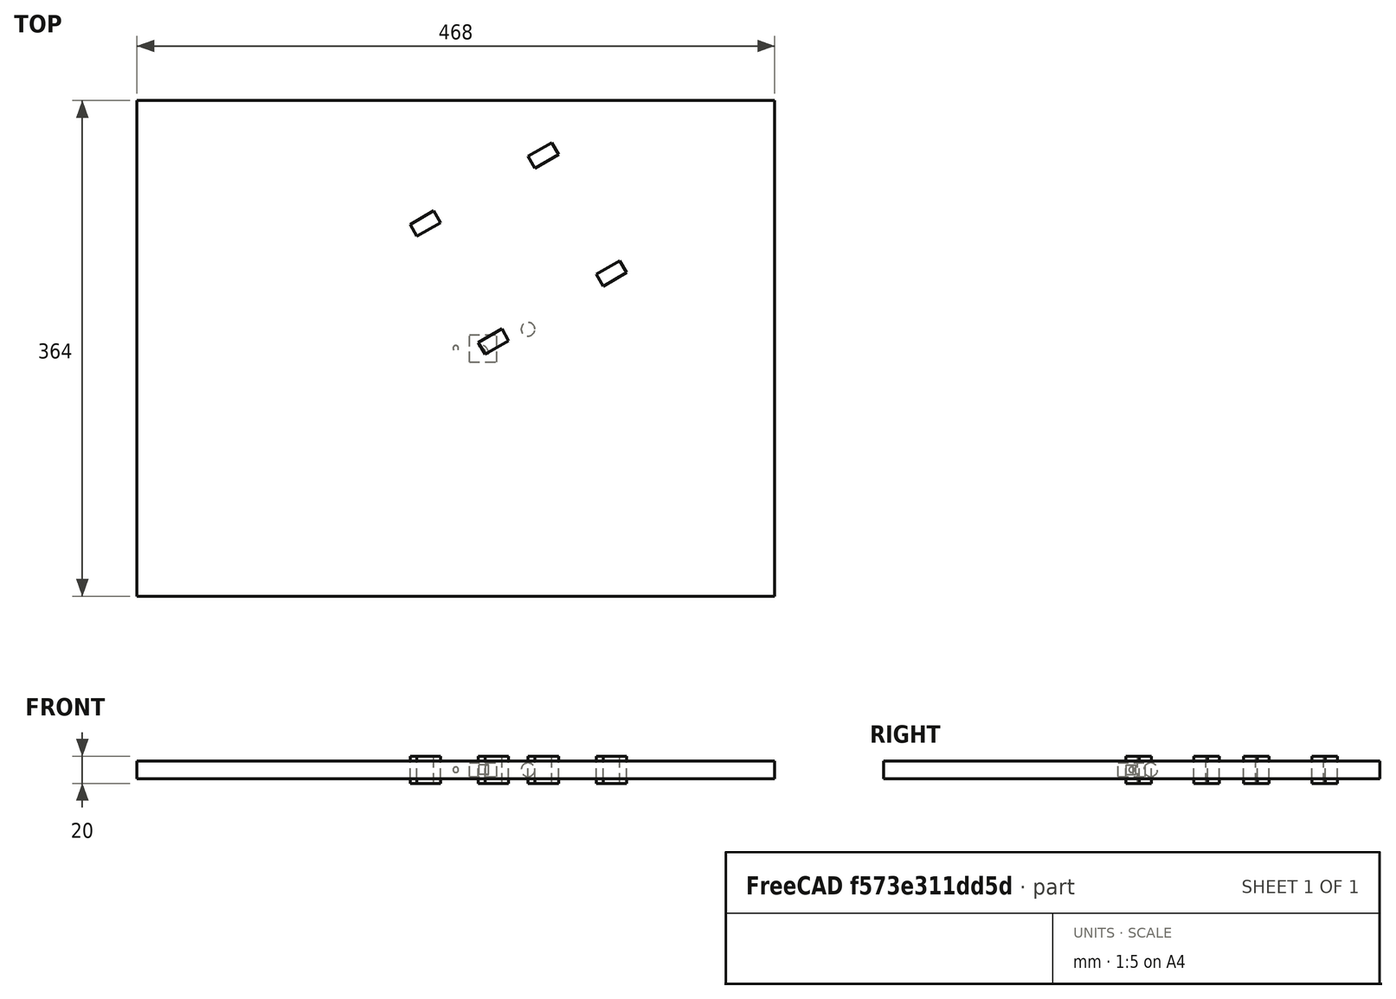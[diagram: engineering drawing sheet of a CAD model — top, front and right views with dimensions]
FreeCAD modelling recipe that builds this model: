
FCSTD DOCUMENT  (FreeCAD 0.21R33694 (Git))
Label: orthoArray-of-Container
License: All rights reserved
LicenseURL: http://en.wikipedia.org/wiki/All_rights_reserved
objects: App::DocumentObjectGroupPython×1251, App::Part×6, Part::FeaturePython×5, Part::Sphere×1
note: 6 computed .brp shape members not serialized (recipe doc carries the construction recipe); baked Part::Feature solids carry a one-line shape summary decoded from their .brp

FEATURE [App::DocumentObjectGroupPython] HALFPI  # scripted group (container) (typed FeaturePython)
  name = HALFPI
  value = pi/2.
FEATURE [App::DocumentObjectGroupPython] PI  # scripted group (container) (typed FeaturePython)
  name = PI
  value = 1.*pi
FEATURE [App::DocumentObjectGroupPython] TWOPI  # scripted group (container) (typed FeaturePython)
  name = TWOPI
  value = 2.*pi
FEATURE [App::DocumentObjectGroupPython] Constants  # scripted group (container) (typed FeaturePython)
  Group = -> [HALFPI,PI,TWOPI]
FEATURE [App::DocumentObjectGroupPython] Variables  # scripted group (container) (typed FeaturePython)
FEATURE [App::DocumentObjectGroupPython] Quantities  # scripted group (container) (typed FeaturePython)
FEATURE [App::DocumentObjectGroupPython] Isotopes  # scripted group (container) (typed FeaturePython)
FEATURE [App::DocumentObjectGroupPython] Elements  # scripted group (container) (typed FeaturePython)
FEATURE [App::DocumentObjectGroupPython] Matrix  # scripted group (container) (typed FeaturePython)
FEATURE [App::DocumentObjectGroupPython] Surfaces  # scripted group (container) (typed FeaturePython)
FEATURE [App::DocumentObjectGroupPython] Opticals  # scripted group (container) (typed FeaturePython)
  Group = -> [Matrix,Surfaces]
FEATURE [App::DocumentObjectGroupPython] G4Isotopes  # scripted group (container) (typed FeaturePython)
FEATURE [App::DocumentObjectGroupPython] H_element  # scripted group (container) (typed FeaturePython)
  Z = 1
  atom_value = 1.008
  formula = H
  name = H_element
FEATURE [App::DocumentObjectGroupPython] He_element  # scripted group (container) (typed FeaturePython)
  Z = 2
  atom_value = 4.0026
  formula = He
  name = He_element
FEATURE [App::DocumentObjectGroupPython] Li_element  # scripted group (container) (typed FeaturePython)
  Z = 3
  atom_value = 6.94
  formula = Li
  name = Li_element
FEATURE [App::DocumentObjectGroupPython] Be_element  # scripted group (container) (typed FeaturePython)
  Z = 4
  atom_value = 9.01218
  formula = Be
  name = Be_element
FEATURE [App::DocumentObjectGroupPython] B_element  # scripted group (container) (typed FeaturePython)
  Z = 5
  atom_value = 10.81
  formula = B
  name = B_element
FEATURE [App::DocumentObjectGroupPython] C_element  # scripted group (container) (typed FeaturePython)
  Z = 6
  atom_value = 12.011
  formula = C
  name = C_element
FEATURE [App::DocumentObjectGroupPython] N_element  # scripted group (container) (typed FeaturePython)
  Z = 7
  atom_value = 14.007
  formula = N
  name = N_element
FEATURE [App::DocumentObjectGroupPython] O_element  # scripted group (container) (typed FeaturePython)
  Z = 8
  atom_value = 15.999
  formula = O
  name = O_element
FEATURE [App::DocumentObjectGroupPython] F_element  # scripted group (container) (typed FeaturePython)
  Z = 9
  atom_value = 18.9984
  formula = F
  name = F_element
FEATURE [App::DocumentObjectGroupPython] Ne_element  # scripted group (container) (typed FeaturePython)
  Z = 10
  atom_value = 20.1797
  formula = Ne
  name = Ne_element
FEATURE [App::DocumentObjectGroupPython] Na_element  # scripted group (container) (typed FeaturePython)
  Z = 11
  atom_value = 22.9898
  formula = Na
  name = Na_element
FEATURE [App::DocumentObjectGroupPython] Mg_element  # scripted group (container) (typed FeaturePython)
  Z = 12
  atom_value = 24.305
  formula = Mg
  name = Mg_element
FEATURE [App::DocumentObjectGroupPython] Al_element  # scripted group (container) (typed FeaturePython)
  Z = 13
  atom_value = 26.9815
  formula = Al
  name = Al_element
FEATURE [App::DocumentObjectGroupPython] Si_element  # scripted group (container) (typed FeaturePython)
  Z = 14
  atom_value = 28.085
  formula = Si
  name = Si_element
FEATURE [App::DocumentObjectGroupPython] P_element  # scripted group (container) (typed FeaturePython)
  Z = 15
  atom_value = 30.9738
  formula = P
  name = P_element
FEATURE [App::DocumentObjectGroupPython] S_element  # scripted group (container) (typed FeaturePython)
  Z = 16
  atom_value = 32.06
  formula = S
  name = S_element
FEATURE [App::DocumentObjectGroupPython] Cl_element  # scripted group (container) (typed FeaturePython)
  Z = 17
  atom_value = 35.45
  formula = Cl
  name = Cl_element
FEATURE [App::DocumentObjectGroupPython] Ar_element  # scripted group (container) (typed FeaturePython)
  Z = 18
  atom_value = 39.95
  formula = Ar
  name = Ar_element
FEATURE [App::DocumentObjectGroupPython] K_element  # scripted group (container) (typed FeaturePython)
  Z = 19
  atom_value = 39.0983
  formula = K
  name = K_element
FEATURE [App::DocumentObjectGroupPython] Ca_element  # scripted group (container) (typed FeaturePython)
  Z = 20
  atom_value = 40.078
  formula = Ca
  name = Ca_element
FEATURE [App::DocumentObjectGroupPython] Sc_element  # scripted group (container) (typed FeaturePython)
  Z = 21
  atom_value = 44.9559
  formula = Sc
  name = Sc_element
FEATURE [App::DocumentObjectGroupPython] Ti_element  # scripted group (container) (typed FeaturePython)
  Z = 22
  atom_value = 47.867
  formula = Ti
  name = Ti_element
FEATURE [App::DocumentObjectGroupPython] V_element  # scripted group (container) (typed FeaturePython)
  Z = 23
  atom_value = 50.9415
  formula = V
  name = V_element
FEATURE [App::DocumentObjectGroupPython] Cr_element  # scripted group (container) (typed FeaturePython)
  Z = 24
  atom_value = 51.9961
  formula = Cr
  name = Cr_element
FEATURE [App::DocumentObjectGroupPython] Mn_element  # scripted group (container) (typed FeaturePython)
  Z = 25
  atom_value = 54.938
  formula = Mn
  name = Mn_element
FEATURE [App::DocumentObjectGroupPython] Fe_element  # scripted group (container) (typed FeaturePython)
  Z = 26
  atom_value = 55.845
  formula = Fe
  name = Fe_element
FEATURE [App::DocumentObjectGroupPython] Co_element  # scripted group (container) (typed FeaturePython)
  Z = 27
  atom_value = 58.9332
  formula = Co
  name = Co_element
FEATURE [App::DocumentObjectGroupPython] Ni_element  # scripted group (container) (typed FeaturePython)
  Z = 28
  atom_value = 58.6934
  formula = Ni
  name = Ni_element
FEATURE [App::DocumentObjectGroupPython] Cu_element  # scripted group (container) (typed FeaturePython)
  Z = 29
  atom_value = 63.546
  formula = Cu
  name = Cu_element
FEATURE [App::DocumentObjectGroupPython] Zn_element  # scripted group (container) (typed FeaturePython)
  Z = 30
  atom_value = 65.38
  formula = Zn
  name = Zn_element
FEATURE [App::DocumentObjectGroupPython] Ga_element  # scripted group (container) (typed FeaturePython)
  Z = 31
  atom_value = 69.723
  formula = Ga
  name = Ga_element
FEATURE [App::DocumentObjectGroupPython] Ge_element  # scripted group (container) (typed FeaturePython)
  Z = 32
  atom_value = 72.63
  formula = Ge
  name = Ge_element
FEATURE [App::DocumentObjectGroupPython] As_element  # scripted group (container) (typed FeaturePython)
  Z = 33
  atom_value = 74.9216
  formula = As
  name = As_element
FEATURE [App::DocumentObjectGroupPython] Se_element  # scripted group (container) (typed FeaturePython)
  Z = 34
  atom_value = 78.971
  formula = Se
  name = Se_element
FEATURE [App::DocumentObjectGroupPython] Br_element  # scripted group (container) (typed FeaturePython)
  Z = 35
  atom_value = 79.904
  formula = Br
  name = Br_element
FEATURE [App::DocumentObjectGroupPython] Kr_element  # scripted group (container) (typed FeaturePython)
  Z = 36
  atom_value = 83.798
  formula = Kr
  name = Kr_element
FEATURE [App::DocumentObjectGroupPython] Rb_element  # scripted group (container) (typed FeaturePython)
  Z = 37
  atom_value = 85.4678
  formula = Rb
  name = Rb_element
FEATURE [App::DocumentObjectGroupPython] Sr_element  # scripted group (container) (typed FeaturePython)
  Z = 38
  atom_value = 87.62
  formula = Sr
  name = Sr_element
FEATURE [App::DocumentObjectGroupPython] Y_element  # scripted group (container) (typed FeaturePython)
  Z = 39
  atom_value = 88.9058
  formula = Y
  name = Y_element
FEATURE [App::DocumentObjectGroupPython] Zr_element  # scripted group (container) (typed FeaturePython)
  Z = 40
  atom_value = 91.224
  formula = Zr
  name = Zr_element
FEATURE [App::DocumentObjectGroupPython] Nb_element  # scripted group (container) (typed FeaturePython)
  Z = 41
  atom_value = 92.9064
  formula = Nb
  name = Nb_element
FEATURE [App::DocumentObjectGroupPython] Mo_element  # scripted group (container) (typed FeaturePython)
  Z = 42
  atom_value = 95.95
  formula = Mo
  name = Mo_element
FEATURE [App::DocumentObjectGroupPython] Tc_element  # scripted group (container) (typed FeaturePython)
  Z = 43
  atom_value = 97
  formula = Tc
  name = Tc_element
FEATURE [App::DocumentObjectGroupPython] Ru_element  # scripted group (container) (typed FeaturePython)
  Z = 44
  atom_value = 101.07
  formula = Ru
  name = Ru_element
FEATURE [App::DocumentObjectGroupPython] Rh_element  # scripted group (container) (typed FeaturePython)
  Z = 45
  atom_value = 102.905
  formula = Rh
  name = Rh_element
FEATURE [App::DocumentObjectGroupPython] Pd_element  # scripted group (container) (typed FeaturePython)
  Z = 46
  atom_value = 106.42
  formula = Pd
  name = Pd_element
FEATURE [App::DocumentObjectGroupPython] Ag_element  # scripted group (container) (typed FeaturePython)
  Z = 47
  atom_value = 107.868
  formula = Ag
  name = Ag_element
FEATURE [App::DocumentObjectGroupPython] Cd_element  # scripted group (container) (typed FeaturePython)
  Z = 48
  atom_value = 112.414
  formula = Cd
  name = Cd_element
FEATURE [App::DocumentObjectGroupPython] In_element  # scripted group (container) (typed FeaturePython)
  Z = 49
  atom_value = 114.818
  formula = In
  name = In_element
FEATURE [App::DocumentObjectGroupPython] Sn_element  # scripted group (container) (typed FeaturePython)
  Z = 50
  atom_value = 118.71
  formula = Sn
  name = Sn_element
FEATURE [App::DocumentObjectGroupPython] Sb_element  # scripted group (container) (typed FeaturePython)
  Z = 51
  atom_value = 121.76
  formula = Sb
  name = Sb_element
FEATURE [App::DocumentObjectGroupPython] Te_element  # scripted group (container) (typed FeaturePython)
  Z = 52
  atom_value = 127.6
  formula = Te
  name = Te_element
FEATURE [App::DocumentObjectGroupPython] I_element  # scripted group (container) (typed FeaturePython)
  Z = 53
  atom_value = 126.904
  formula = I
  name = I_element
FEATURE [App::DocumentObjectGroupPython] Xe_element  # scripted group (container) (typed FeaturePython)
  Z = 54
  atom_value = 131.293
  formula = Xe
  name = Xe_element
FEATURE [App::DocumentObjectGroupPython] Cs_element  # scripted group (container) (typed FeaturePython)
  Z = 55
  atom_value = 132.905
  formula = Cs
  name = Cs_element
FEATURE [App::DocumentObjectGroupPython] Ba_element  # scripted group (container) (typed FeaturePython)
  Z = 56
  atom_value = 137.327
  formula = Ba
  name = Ba_element
FEATURE [App::DocumentObjectGroupPython] La_element  # scripted group (container) (typed FeaturePython)
  Z = 57
  atom_value = 138.905
  formula = La
  name = La_element
FEATURE [App::DocumentObjectGroupPython] Ce_element  # scripted group (container) (typed FeaturePython)
  Z = 58
  atom_value = 140.116
  formula = Ce
  name = Ce_element
FEATURE [App::DocumentObjectGroupPython] Pr_element  # scripted group (container) (typed FeaturePython)
  Z = 59
  atom_value = 140.908
  formula = Pr
  name = Pr_element
FEATURE [App::DocumentObjectGroupPython] Nd_element  # scripted group (container) (typed FeaturePython)
  Z = 60
  atom_value = 144.242
  formula = Nd
  name = Nd_element
FEATURE [App::DocumentObjectGroupPython] Pm_element  # scripted group (container) (typed FeaturePython)
  Z = 61
  atom_value = 145
  formula = Pm
  name = Pm_element
FEATURE [App::DocumentObjectGroupPython] Sm_element  # scripted group (container) (typed FeaturePython)
  Z = 62
  atom_value = 150.36
  formula = Sm
  name = Sm_element
FEATURE [App::DocumentObjectGroupPython] Eu_element  # scripted group (container) (typed FeaturePython)
  Z = 63
  atom_value = 151.964
  formula = Eu
  name = Eu_element
FEATURE [App::DocumentObjectGroupPython] Gd_element  # scripted group (container) (typed FeaturePython)
  Z = 64
  atom_value = 157.25
  formula = Gd
  name = Gd_element
FEATURE [App::DocumentObjectGroupPython] Tb_element  # scripted group (container) (typed FeaturePython)
  Z = 65
  atom_value = 158.925
  formula = Tb
  name = Tb_element
FEATURE [App::DocumentObjectGroupPython] Dy_element  # scripted group (container) (typed FeaturePython)
  Z = 66
  atom_value = 162.5
  formula = Dy
  name = Dy_element
FEATURE [App::DocumentObjectGroupPython] Ho_element  # scripted group (container) (typed FeaturePython)
  Z = 67
  atom_value = 164.93
  formula = Ho
  name = Ho_element
FEATURE [App::DocumentObjectGroupPython] Er_element  # scripted group (container) (typed FeaturePython)
  Z = 68
  atom_value = 167.259
  formula = Er
  name = Er_element
FEATURE [App::DocumentObjectGroupPython] Tm_element  # scripted group (container) (typed FeaturePython)
  Z = 69
  atom_value = 168.934
  formula = Tm
  name = Tm_element
FEATURE [App::DocumentObjectGroupPython] Yb_element  # scripted group (container) (typed FeaturePython)
  Z = 70
  atom_value = 173.045
  formula = Yb
  name = Yb_element
FEATURE [App::DocumentObjectGroupPython] Lu_element  # scripted group (container) (typed FeaturePython)
  Z = 71
  atom_value = 174.967
  formula = Lu
  name = Lu_element
FEATURE [App::DocumentObjectGroupPython] Hf_element  # scripted group (container) (typed FeaturePython)
  Z = 72
  atom_value = 178.49
  formula = Hf
  name = Hf_element
FEATURE [App::DocumentObjectGroupPython] Ta_element  # scripted group (container) (typed FeaturePython)
  Z = 73
  atom_value = 180.948
  formula = Ta
  name = Ta_element
FEATURE [App::DocumentObjectGroupPython] W_element  # scripted group (container) (typed FeaturePython)
  Z = 74
  atom_value = 183.84
  formula = W
  name = W_element
FEATURE [App::DocumentObjectGroupPython] Re_element  # scripted group (container) (typed FeaturePython)
  Z = 75
  atom_value = 186.207
  formula = Re
  name = Re_element
FEATURE [App::DocumentObjectGroupPython] Os_element  # scripted group (container) (typed FeaturePython)
  Z = 76
  atom_value = 190.23
  formula = Os
  name = Os_element
FEATURE [App::DocumentObjectGroupPython] Ir_element  # scripted group (container) (typed FeaturePython)
  Z = 77
  atom_value = 192.217
  formula = Ir
  name = Ir_element
FEATURE [App::DocumentObjectGroupPython] Pt_element  # scripted group (container) (typed FeaturePython)
  Z = 78
  atom_value = 195.084
  formula = Pt
  name = Pt_element
FEATURE [App::DocumentObjectGroupPython] Au_element  # scripted group (container) (typed FeaturePython)
  Z = 79
  atom_value = 196.967
  formula = Au
  name = Au_element
FEATURE [App::DocumentObjectGroupPython] Hg_element  # scripted group (container) (typed FeaturePython)
  Z = 80
  atom_value = 200.592
  formula = Hg
  name = Hg_element
FEATURE [App::DocumentObjectGroupPython] Tl_element  # scripted group (container) (typed FeaturePython)
  Z = 81
  atom_value = 204.38
  formula = Tl
  name = Tl_element
FEATURE [App::DocumentObjectGroupPython] Pb_element  # scripted group (container) (typed FeaturePython)
  Z = 82
  atom_value = 207.2
  formula = Pb
  name = Pb_element
FEATURE [App::DocumentObjectGroupPython] Bi_element  # scripted group (container) (typed FeaturePython)
  Z = 83
  atom_value = 208.98
  formula = Bi
  name = Bi_element
FEATURE [App::DocumentObjectGroupPython] Po_element  # scripted group (container) (typed FeaturePython)
  Z = 84
  atom_value = 209
  formula = Po
  name = Po_element
FEATURE [App::DocumentObjectGroupPython] At_element  # scripted group (container) (typed FeaturePython)
  Z = 85
  atom_value = 210
  formula = At
  name = At_element
FEATURE [App::DocumentObjectGroupPython] Rn_element  # scripted group (container) (typed FeaturePython)
  Z = 86
  atom_value = 222
  formula = Rn
  name = Rn_element
FEATURE [App::DocumentObjectGroupPython] Fr_element  # scripted group (container) (typed FeaturePython)
  Z = 87
  atom_value = 223
  formula = Fr
  name = Fr_element
FEATURE [App::DocumentObjectGroupPython] Ra_element  # scripted group (container) (typed FeaturePython)
  Z = 88
  atom_value = 226
  formula = Ra
  name = Ra_element
FEATURE [App::DocumentObjectGroupPython] Ac_element  # scripted group (container) (typed FeaturePython)
  Z = 89
  atom_value = 227
  formula = Ac
  name = Ac_element
FEATURE [App::DocumentObjectGroupPython] Th_element  # scripted group (container) (typed FeaturePython)
  Z = 90
  atom_value = 232.038
  formula = Th
  name = Th_element
FEATURE [App::DocumentObjectGroupPython] Pa_element  # scripted group (container) (typed FeaturePython)
  Z = 91
  atom_value = 231.036
  formula = Pa
  name = Pa_element
FEATURE [App::DocumentObjectGroupPython] U_element  # scripted group (container) (typed FeaturePython)
  Z = 92
  atom_value = 238.029
  formula = U
  name = U_element
FEATURE [App::DocumentObjectGroupPython] Np_element  # scripted group (container) (typed FeaturePython)
  Z = 93
  atom_value = 237
  formula = Np
  name = Np_element
FEATURE [App::DocumentObjectGroupPython] Pu_element  # scripted group (container) (typed FeaturePython)
  Z = 94
  atom_value = 244
  formula = Pu
  name = Pu_element
FEATURE [App::DocumentObjectGroupPython] Am_element  # scripted group (container) (typed FeaturePython)
  Z = 95
  atom_value = 243
  formula = Am
  name = Am_element
FEATURE [App::DocumentObjectGroupPython] Cm_element  # scripted group (container) (typed FeaturePython)
  Z = 96
  atom_value = 247
  formula = Cm
  name = Cm_element
FEATURE [App::DocumentObjectGroupPython] Bk_element  # scripted group (container) (typed FeaturePython)
  Z = 97
  atom_value = 247
  formula = Bk
  name = Bk_element
FEATURE [App::DocumentObjectGroupPython] Cf_element  # scripted group (container) (typed FeaturePython)
  Z = 98
  atom_value = 251
  formula = Cf
  name = Cf_element
FEATURE [App::DocumentObjectGroupPython] G4Elements  # scripted group (container) (typed FeaturePython)
  Group = -> [H_element,He_element,Li_element,Be_element,B_element,C_element,N_element,O_element,F_element,Ne_element,Na_element,Mg_element,Al_element,Si_element,P_element,S_element,Cl_element,Ar_element,K_element,Ca_element,Sc_element,Ti_element,V_element,Cr_element,Mn_element,Fe_element,Co_element,Ni_element,Cu_element,Zn_element,Ga_element,Ge_element,As_element,Se_element,Br_element,Kr_element,Rb_element,+61 more]
FEATURE [App::DocumentObjectGroupPython] H_element001  label="H_element : 0.101"  # scripted group (container) (typed FeaturePython)
  n = 0.101327
FEATURE [App::DocumentObjectGroupPython] C_element001  label="C_element : 0.775"  # scripted group (container) (typed FeaturePython)
  n = 0.7755
FEATURE [App::DocumentObjectGroupPython] N_element001  label="N_element : 0.035"  # scripted group (container) (typed FeaturePython)
  n = 0.035057
FEATURE [App::DocumentObjectGroupPython] O_element001  label="O_element : 0.052"  # scripted group (container) (typed FeaturePython)
  n = 0.0523159
FEATURE [App::DocumentObjectGroupPython] F_element001  label="F_element : 0.017"  # scripted group (container) (typed FeaturePython)
  n = 0.017422
FEATURE [App::DocumentObjectGroupPython] Ca_element001  label="Ca_element : 0.018"  # scripted group (container) (typed FeaturePython)
  n = 0.018378
FEATURE [App::DocumentObjectGroupPython] G4_A_150_TISSUE  label="G4_A-150_TISSUE"  # scripted group (container) (typed FeaturePython)
  Dunit = g/cm3
  Dvalue = 1.127
  Group = -> [H_element001,C_element001,N_element001,O_element001,F_element001,Ca_element001]
  conduct = 2
  density = 1
  expand = 3
  formula = G4_A-150_TISSUE
  name = G4_A-150_TISSUE
  specific = 4
FEATURE [App::DocumentObjectGroupPython] C_element002  label="C_element : 3"  # scripted group (container) (typed FeaturePython)
  n = 3
  ref = C_element
FEATURE [App::DocumentObjectGroupPython] H_element002  label="H_element : 6"  # scripted group (container) (typed FeaturePython)
  n = 6
  ref = H_element
FEATURE [App::DocumentObjectGroupPython] O_element002  label="O_element : 1"  # scripted group (container) (typed FeaturePython)
  n = 1
  ref = O_element
FEATURE [App::DocumentObjectGroupPython] G4_ACETONE  # scripted group (container) (typed FeaturePython)
  Dunit = g/cm3
  Dvalue = 0.7899
  Group = -> [C_element002,H_element002,O_element002]
  conduct = 2
  density = 1
  expand = 3
  formula = G4_ACETONE
  name = G4_ACETONE
  specific = 4
FEATURE [App::DocumentObjectGroupPython] C_element003  label="C_element : 2"  # scripted group (container) (typed FeaturePython)
  n = 2
  ref = C_element
FEATURE [App::DocumentObjectGroupPython] H_element003  label="H_element : 2"  # scripted group (container) (typed FeaturePython)
  n = 2
  ref = H_element
FEATURE [App::DocumentObjectGroupPython] G4_ACETYLENE  # scripted group (container) (typed FeaturePython)
  Dunit = g/cm3
  Dvalue = 0.0010967
  Group = -> [C_element003,H_element003]
  conduct = 2
  density = 1
  expand = 3
  formula = G4_ACETYLENE
  name = G4_ACETYLENE
  specific = 4
FEATURE [App::DocumentObjectGroupPython] C_element004  label="C_element : 5"  # scripted group (container) (typed FeaturePython)
  n = 5
  ref = C_element
FEATURE [App::DocumentObjectGroupPython] H_element004  label="H_element : 5"  # scripted group (container) (typed FeaturePython)
  n = 5
  ref = H_element
FEATURE [App::DocumentObjectGroupPython] N_element002  label="N_element : 5"  # scripted group (container) (typed FeaturePython)
  n = 5
  ref = N_element
FEATURE [App::DocumentObjectGroupPython] G4_ADENINE  # scripted group (container) (typed FeaturePython)
  Dunit = g/cm3
  Dvalue = 1.6
  Group = -> [C_element004,H_element004,N_element002]
  conduct = 2
  density = 1
  expand = 3
  formula = G4_ADENINE
  name = G4_ADENINE
  specific = 4
FEATURE [App::DocumentObjectGroupPython] H_element005  label="H_element : 0.114"  # scripted group (container) (typed FeaturePython)
  n = 0.114
FEATURE [App::DocumentObjectGroupPython] C_element005  label="C_element : 0.598"  # scripted group (container) (typed FeaturePython)
  n = 0.598
FEATURE [App::DocumentObjectGroupPython] N_element003  label="N_element : 0.007"  # scripted group (container) (typed FeaturePython)
  n = 0.007
FEATURE [App::DocumentObjectGroupPython] O_element003  label="O_element : 0.278"  # scripted group (container) (typed FeaturePython)
  n = 0.278
FEATURE [App::DocumentObjectGroupPython] Na_element001  label="Na_element : 0.001"  # scripted group (container) (typed FeaturePython)
  n = 0.001
FEATURE [App::DocumentObjectGroupPython] S_element001  label="S_element : 0.001"  # scripted group (container) (typed FeaturePython)
  n = 0.001
FEATURE [App::DocumentObjectGroupPython] Cl_element001  label="Cl_element : 0.001"  # scripted group (container) (typed FeaturePython)
  n = 0.001
FEATURE [App::DocumentObjectGroupPython] G4_ADIPOSE_TISSUE_ICRP  # scripted group (container) (typed FeaturePython)
  Dunit = g/cm3
  Dvalue = 0.95
  Group = -> [H_element005,C_element005,N_element003,O_element003,Na_element001,S_element001,Cl_element001]
  conduct = 2
  density = 1
  expand = 3
  formula = G4_ADIPOSE_TISSUE_ICRP
  name = G4_ADIPOSE_TISSUE_ICRP
  specific = 4
FEATURE [App::DocumentObjectGroupPython] C_element006  label="C_element : 0.000"  # scripted group (container) (typed FeaturePython)
  n = 0.000124
FEATURE [App::DocumentObjectGroupPython] N_element004  label="N_element : 0.755"  # scripted group (container) (typed FeaturePython)
  n = 0.755268
FEATURE [App::DocumentObjectGroupPython] O_element004  label="O_element : 0.232"  # scripted group (container) (typed FeaturePython)
  n = 0.231781
FEATURE [App::DocumentObjectGroupPython] Ar_element001  label="Ar_element : 0.013"  # scripted group (container) (typed FeaturePython)
  n = 0.012827
FEATURE [App::DocumentObjectGroupPython] G4_AIR  # scripted group (container) (typed FeaturePython)
  Dunit = g/cm3
  Dvalue = 0.00120479
  Group = -> [C_element006,N_element004,O_element004,Ar_element001]
  conduct = 2
  density = 1
  expand = 3
  formula = G4_AIR
  name = G4_AIR
  specific = 4
FEATURE [App::DocumentObjectGroupPython] C_element007  label="C_element : 006"  # scripted group (container) (typed FeaturePython)
  n = 3
  ref = C_element
FEATURE [App::DocumentObjectGroupPython] H_element006  label="H_element : 7"  # scripted group (container) (typed FeaturePython)
  n = 7
  ref = H_element
FEATURE [App::DocumentObjectGroupPython] N_element005  label="N_element : 1"  # scripted group (container) (typed FeaturePython)
  n = 1
  ref = N_element
FEATURE [App::DocumentObjectGroupPython] O_element005  label="O_element : 2"  # scripted group (container) (typed FeaturePython)
  n = 2
  ref = O_element
FEATURE [App::DocumentObjectGroupPython] G4_ALANINE  # scripted group (container) (typed FeaturePython)
  Dunit = g/cm3
  Dvalue = 1.42
  Group = -> [C_element007,H_element006,N_element005,O_element005]
  conduct = 2
  density = 1
  expand = 3
  formula = G4_ALANINE
  name = G4_ALANINE
  specific = 4
FEATURE [App::DocumentObjectGroupPython] Al_element001  label="Al_element : 2"  # scripted group (container) (typed FeaturePython)
  n = 2
  ref = Al_element
FEATURE [App::DocumentObjectGroupPython] O_element006  label="O_element : 3"  # scripted group (container) (typed FeaturePython)
  n = 3
  ref = O_element
FEATURE [App::DocumentObjectGroupPython] G4_ALUMINUM_OXIDE  # scripted group (container) (typed FeaturePython)
  Dunit = g/cm3
  Dvalue = 3.97
  Group = -> [Al_element001,O_element006]
  conduct = 2
  density = 1
  expand = 3
  formula = G4_ALUMINUM_OXIDE
  name = G4_ALUMINUM_OXIDE
  specific = 4
FEATURE [App::DocumentObjectGroupPython] H_element007  label="H_element : 0.106"  # scripted group (container) (typed FeaturePython)
  n = 0.10593
FEATURE [App::DocumentObjectGroupPython] C_element008  label="C_element : 0.789"  # scripted group (container) (typed FeaturePython)
  n = 0.788974
FEATURE [App::DocumentObjectGroupPython] O_element007  label="O_element : 0.105"  # scripted group (container) (typed FeaturePython)
  n = 0.105096
FEATURE [App::DocumentObjectGroupPython] G4_AMBER  # scripted group (container) (typed FeaturePython)
  Dunit = g/cm3
  Dvalue = 1.1
  Group = -> [H_element007,C_element008,O_element007]
  conduct = 2
  density = 1
  expand = 3
  formula = G4_AMBER
  name = G4_AMBER
  specific = 4
FEATURE [App::DocumentObjectGroupPython] N_element006  label="N_element : 006"  # scripted group (container) (typed FeaturePython)
  n = 1
  ref = N_element
FEATURE [App::DocumentObjectGroupPython] H_element008  label="H_element : 3"  # scripted group (container) (typed FeaturePython)
  n = 3
  ref = H_element
FEATURE [App::DocumentObjectGroupPython] G4_AMMONIA  # scripted group (container) (typed FeaturePython)
  Dunit = g/cm3
  Dvalue = 0.000826019
  Group = -> [N_element006,H_element008]
  conduct = 2
  density = 1
  expand = 3
  formula = G4_AMMONIA
  name = G4_AMMONIA
  specific = 4
FEATURE [App::DocumentObjectGroupPython] C_element009  label="C_element : 6"  # scripted group (container) (typed FeaturePython)
  n = 6
  ref = C_element
FEATURE [App::DocumentObjectGroupPython] H_element009  label="H_element : 008"  # scripted group (container) (typed FeaturePython)
  n = 7
  ref = H_element
FEATURE [App::DocumentObjectGroupPython] N_element007  label="N_element : 007"  # scripted group (container) (typed FeaturePython)
  n = 1
  ref = N_element
FEATURE [App::DocumentObjectGroupPython] G4_ANILINE  # scripted group (container) (typed FeaturePython)
  Dunit = g/cm3
  Dvalue = 1.0235
  Group = -> [C_element009,H_element009,N_element007]
  conduct = 2
  density = 1
  expand = 3
  formula = G4_ANILINE
  name = G4_ANILINE
  specific = 4
FEATURE [App::DocumentObjectGroupPython] C_element010  label="C_element : 14"  # scripted group (container) (typed FeaturePython)
  n = 14
  ref = C_element
FEATURE [App::DocumentObjectGroupPython] H_element010  label="H_element : 10"  # scripted group (container) (typed FeaturePython)
  n = 10
  ref = H_element
FEATURE [App::DocumentObjectGroupPython] G4_ANTHRACENE  # scripted group (container) (typed FeaturePython)
  Dunit = g/cm3
  Dvalue = 1.283
  Group = -> [C_element010,H_element010]
  conduct = 2
  density = 1
  expand = 3
  formula = G4_ANTHRACENE
  name = G4_ANTHRACENE
  specific = 4
FEATURE [App::DocumentObjectGroupPython] H_element011  label="H_element : 0.065"  # scripted group (container) (typed FeaturePython)
  n = 0.0654709
FEATURE [App::DocumentObjectGroupPython] C_element011  label="C_element : 0.537"  # scripted group (container) (typed FeaturePython)
  n = 0.536944
FEATURE [App::DocumentObjectGroupPython] N_element008  label="N_element : 0.021"  # scripted group (container) (typed FeaturePython)
  n = 0.0215
FEATURE [App::DocumentObjectGroupPython] O_element008  label="O_element : 0.032"  # scripted group (container) (typed FeaturePython)
  n = 0.032085
FEATURE [App::DocumentObjectGroupPython] F_element002  label="F_element : 0.167"  # scripted group (container) (typed FeaturePython)
  n = 0.167411
FEATURE [App::DocumentObjectGroupPython] Ca_element002  label="Ca_element : 0.177"  # scripted group (container) (typed FeaturePython)
  n = 0.176589
FEATURE [App::DocumentObjectGroupPython] G4_B_100_BONE  label="G4_B-100_BONE"  # scripted group (container) (typed FeaturePython)
  Dunit = g/cm3
  Dvalue = 1.45
  Group = -> [H_element011,C_element011,N_element008,O_element008,F_element002,Ca_element002]
  conduct = 2
  density = 1
  expand = 3
  formula = G4_B-100_BONE
  name = G4_B-100_BONE
  specific = 4
FEATURE [App::DocumentObjectGroupPython] H_element012  label="H_element : 0.057"  # scripted group (container) (typed FeaturePython)
  n = 0.057441
FEATURE [App::DocumentObjectGroupPython] C_element012  label="C_element : 0.790"  # scripted group (container) (typed FeaturePython)
  n = 0.774591
FEATURE [App::DocumentObjectGroupPython] O_element009  label="O_element : 0.168"  # scripted group (container) (typed FeaturePython)
  n = 0.167968
FEATURE [App::DocumentObjectGroupPython] G4_BAKELITE  # scripted group (container) (typed FeaturePython)
  Dunit = g/cm3
  Dvalue = 1.25
  Group = -> [H_element012,C_element012,O_element009]
  conduct = 2
  density = 1
  expand = 3
  formula = G4_BAKELITE
  name = G4_BAKELITE
  specific = 4
FEATURE [App::DocumentObjectGroupPython] Ba_element001  label="Ba_element : 1"  # scripted group (container) (typed FeaturePython)
  n = 1
  ref = Ba_element
FEATURE [App::DocumentObjectGroupPython] F_element003  label="F_element : 2"  # scripted group (container) (typed FeaturePython)
  n = 2
  ref = F_element
FEATURE [App::DocumentObjectGroupPython] G4_BARIUM_FLUORIDE  # scripted group (container) (typed FeaturePython)
  Dunit = g/cm3
  Dvalue = 4.89
  Group = -> [Ba_element001,F_element003]
  conduct = 2
  density = 1
  expand = 3
  formula = G4_BARIUM_FLUORIDE
  name = G4_BARIUM_FLUORIDE
  specific = 4
FEATURE [App::DocumentObjectGroupPython] Ba_element002  label="Ba_element : 002"  # scripted group (container) (typed FeaturePython)
  n = 1
  ref = Ba_element
FEATURE [App::DocumentObjectGroupPython] S_element002  label="S_element : 1"  # scripted group (container) (typed FeaturePython)
  n = 1
  ref = S_element
FEATURE [App::DocumentObjectGroupPython] O_element010  label="O_element : 4"  # scripted group (container) (typed FeaturePython)
  n = 4
  ref = O_element
FEATURE [App::DocumentObjectGroupPython] G4_BARIUM_SULFATE  # scripted group (container) (typed FeaturePython)
  Dunit = g/cm3
  Dvalue = 4.5
  Group = -> [Ba_element002,S_element002,O_element010]
  conduct = 2
  density = 1
  expand = 3
  formula = G4_BARIUM_SULFATE
  name = G4_BARIUM_SULFATE
  specific = 4
FEATURE [App::DocumentObjectGroupPython] C_element013  label="C_element : 007"  # scripted group (container) (typed FeaturePython)
  n = 6
  ref = C_element
FEATURE [App::DocumentObjectGroupPython] H_element013  label="H_element : 009"  # scripted group (container) (typed FeaturePython)
  n = 6
  ref = H_element
FEATURE [App::DocumentObjectGroupPython] G4_BENZENE  # scripted group (container) (typed FeaturePython)
  Dunit = g/cm3
  Dvalue = 0.87865
  Group = -> [C_element013,H_element013]
  conduct = 2
  density = 1
  expand = 3
  formula = G4_BENZENE
  name = G4_BENZENE
  specific = 4
FEATURE [App::DocumentObjectGroupPython] Be_element001  label="Be_element : 1"  # scripted group (container) (typed FeaturePython)
  n = 1
  ref = Be_element
FEATURE [App::DocumentObjectGroupPython] O_element011  label="O_element : 005"  # scripted group (container) (typed FeaturePython)
  n = 1
  ref = O_element
FEATURE [App::DocumentObjectGroupPython] G4_BERYLLIUM_OXIDE  # scripted group (container) (typed FeaturePython)
  Dunit = g/cm3
  Dvalue = 3.01
  Group = -> [Be_element001,O_element011]
  conduct = 2
  density = 1
  expand = 3
  formula = G4_BERYLLIUM_OXIDE
  name = G4_BERYLLIUM_OXIDE
  specific = 4
FEATURE [App::DocumentObjectGroupPython] Bi_element001  label="Bi_element : 4"  # scripted group (container) (typed FeaturePython)
  n = 4
  ref = Bi_element
FEATURE [App::DocumentObjectGroupPython] Ge_element001  label="Ge_element : 3"  # scripted group (container) (typed FeaturePython)
  n = 3
  ref = Ge_element
FEATURE [App::DocumentObjectGroupPython] O_element012  label="O_element : 12"  # scripted group (container) (typed FeaturePython)
  n = 12
  ref = O_element
FEATURE [App::DocumentObjectGroupPython] G4_BGO  # scripted group (container) (typed FeaturePython)
  Dunit = g/cm3
  Dvalue = 7.13
  Group = -> [Bi_element001,Ge_element001,O_element012]
  conduct = 2
  density = 1
  expand = 3
  formula = G4_BGO
  name = G4_BGO
  specific = 4
FEATURE [App::DocumentObjectGroupPython] H_element014  label="H_element : 0.102"  # scripted group (container) (typed FeaturePython)
  n = 0.102
FEATURE [App::DocumentObjectGroupPython] C_element014  label="C_element : 0.110"  # scripted group (container) (typed FeaturePython)
  n = 0.11
FEATURE [App::DocumentObjectGroupPython] N_element009  label="N_element : 0.033"  # scripted group (container) (typed FeaturePython)
  n = 0.033
FEATURE [App::DocumentObjectGroupPython] O_element013  label="O_element : 0.745"  # scripted group (container) (typed FeaturePython)
  n = 0.745
FEATURE [App::DocumentObjectGroupPython] Na_element002  label="Na_element : 0.002"  # scripted group (container) (typed FeaturePython)
  n = 0.001
FEATURE [App::DocumentObjectGroupPython] P_element001  label="P_element : 0.001"  # scripted group (container) (typed FeaturePython)
  n = 0.001
FEATURE [App::DocumentObjectGroupPython] S_element003  label="S_element : 0.002"  # scripted group (container) (typed FeaturePython)
  n = 0.002
FEATURE [App::DocumentObjectGroupPython] Cl_element002  label="Cl_element : 0.003"  # scripted group (container) (typed FeaturePython)
  n = 0.003
FEATURE [App::DocumentObjectGroupPython] K_element001  label="K_element : 0.002"  # scripted group (container) (typed FeaturePython)
  n = 0.002
FEATURE [App::DocumentObjectGroupPython] Fe_element001  label="Fe_element : 0.001"  # scripted group (container) (typed FeaturePython)
  n = 0.001
FEATURE [App::DocumentObjectGroupPython] G4_BLOOD_ICRP  # scripted group (container) (typed FeaturePython)
  Dunit = g/cm3
  Dvalue = 1.06
  Group = -> [H_element014,C_element014,N_element009,O_element013,Na_element002,P_element001,S_element003,Cl_element002,K_element001,Fe_element001]
  conduct = 2
  density = 1
  expand = 3
  formula = G4_BLOOD_ICRP
  name = G4_BLOOD_ICRP
  specific = 4
FEATURE [App::DocumentObjectGroupPython] H_element015  label="H_element : 0.064"  # scripted group (container) (typed FeaturePython)
  n = 0.064
FEATURE [App::DocumentObjectGroupPython] C_element015  label="C_element : 0.278"  # scripted group (container) (typed FeaturePython)
  n = 0.278
FEATURE [App::DocumentObjectGroupPython] N_element010  label="N_element : 0.027"  # scripted group (container) (typed FeaturePython)
  n = 0.027
FEATURE [App::DocumentObjectGroupPython] O_element014  label="O_element : 0.410"  # scripted group (container) (typed FeaturePython)
  n = 0.41
FEATURE [App::DocumentObjectGroupPython] Mg_element001  label="Mg_element : 0.002"  # scripted group (container) (typed FeaturePython)
  n = 0.002
FEATURE [App::DocumentObjectGroupPython] P_element002  label="P_element : 0.070"  # scripted group (container) (typed FeaturePython)
  n = 0.07
FEATURE [App::DocumentObjectGroupPython] S_element004  label="S_element : 0.003"  # scripted group (container) (typed FeaturePython)
  n = 0.002
FEATURE [App::DocumentObjectGroupPython] Ca_element003  label="Ca_element : 0.147"  # scripted group (container) (typed FeaturePython)
  n = 0.147
FEATURE [App::DocumentObjectGroupPython] G4_BONE_COMPACT_ICRU  # scripted group (container) (typed FeaturePython)
  Dunit = g/cm3
  Dvalue = 1.85
  Group = -> [H_element015,C_element015,N_element010,O_element014,Mg_element001,P_element002,S_element004,Ca_element003]
  conduct = 2
  density = 1
  expand = 3
  formula = G4_BONE_COMPACT_ICRU
  name = G4_BONE_COMPACT_ICRU
  specific = 4
FEATURE [App::DocumentObjectGroupPython] H_element016  label="H_element : 0.034"  # scripted group (container) (typed FeaturePython)
  n = 0.034
FEATURE [App::DocumentObjectGroupPython] C_element016  label="C_element : 0.155"  # scripted group (container) (typed FeaturePython)
  n = 0.155
FEATURE [App::DocumentObjectGroupPython] N_element011  label="N_element : 0.042"  # scripted group (container) (typed FeaturePython)
  n = 0.042
FEATURE [App::DocumentObjectGroupPython] O_element015  label="O_element : 0.435"  # scripted group (container) (typed FeaturePython)
  n = 0.435
FEATURE [App::DocumentObjectGroupPython] Na_element003  label="Na_element : 0.003"  # scripted group (container) (typed FeaturePython)
  n = 0.001
FEATURE [App::DocumentObjectGroupPython] Mg_element002  label="Mg_element : 0.003"  # scripted group (container) (typed FeaturePython)
  n = 0.002
FEATURE [App::DocumentObjectGroupPython] P_element003  label="P_element : 0.103"  # scripted group (container) (typed FeaturePython)
  n = 0.103
FEATURE [App::DocumentObjectGroupPython] S_element005  label="S_element : 0.004"  # scripted group (container) (typed FeaturePython)
  n = 0.003
FEATURE [App::DocumentObjectGroupPython] Ca_element004  label="Ca_element : 0.225"  # scripted group (container) (typed FeaturePython)
  n = 0.225
FEATURE [App::DocumentObjectGroupPython] G4_BONE_CORTICAL_ICRP  # scripted group (container) (typed FeaturePython)
  Dunit = g/cm3
  Dvalue = 1.92
  Group = -> [H_element016,C_element016,N_element011,O_element015,Na_element003,Mg_element002,P_element003,S_element005,Ca_element004]
  conduct = 2
  density = 1
  expand = 3
  formula = G4_BONE_CORTICAL_ICRP
  name = G4_BONE_CORTICAL_ICRP
  specific = 4
FEATURE [App::DocumentObjectGroupPython] B_element001  label="B_element : 4"  # scripted group (container) (typed FeaturePython)
  n = 4
  ref = B_element
FEATURE [App::DocumentObjectGroupPython] C_element017  label="C_element : 1"  # scripted group (container) (typed FeaturePython)
  n = 1
  ref = C_element
FEATURE [App::DocumentObjectGroupPython] G4_BORON_CARBIDE  # scripted group (container) (typed FeaturePython)
  Dunit = g/cm3
  Dvalue = 2.52
  Group = -> [B_element001,C_element017]
  conduct = 2
  density = 1
  expand = 3
  formula = G4_BORON_CARBIDE
  name = G4_BORON_CARBIDE
  specific = 4
FEATURE [App::DocumentObjectGroupPython] B_element002  label="B_element : 2"  # scripted group (container) (typed FeaturePython)
  n = 2
  ref = B_element
FEATURE [App::DocumentObjectGroupPython] O_element016  label="O_element : 006"  # scripted group (container) (typed FeaturePython)
  n = 3
  ref = O_element
FEATURE [App::DocumentObjectGroupPython] G4_BORON_OXIDE  # scripted group (container) (typed FeaturePython)
  Dunit = g/cm3
  Dvalue = 1.812
  Group = -> [B_element002,O_element016]
  conduct = 2
  density = 1
  expand = 3
  formula = G4_BORON_OXIDE
  name = G4_BORON_OXIDE
  specific = 4
FEATURE [App::DocumentObjectGroupPython] H_element017  label="H_element : 0.107"  # scripted group (container) (typed FeaturePython)
  n = 0.107
FEATURE [App::DocumentObjectGroupPython] C_element018  label="C_element : 0.145"  # scripted group (container) (typed FeaturePython)
  n = 0.145
FEATURE [App::DocumentObjectGroupPython] N_element012  label="N_element : 0.022"  # scripted group (container) (typed FeaturePython)
  n = 0.022
FEATURE [App::DocumentObjectGroupPython] O_element017  label="O_element : 0.712"  # scripted group (container) (typed FeaturePython)
  n = 0.712
FEATURE [App::DocumentObjectGroupPython] Na_element004  label="Na_element : 0.004"  # scripted group (container) (typed FeaturePython)
  n = 0.002
FEATURE [App::DocumentObjectGroupPython] P_element004  label="P_element : 0.004"  # scripted group (container) (typed FeaturePython)
  n = 0.004
FEATURE [App::DocumentObjectGroupPython] S_element006  label="S_element : 0.005"  # scripted group (container) (typed FeaturePython)
  n = 0.002
FEATURE [App::DocumentObjectGroupPython] Cl_element003  label="Cl_element : 0.004"  # scripted group (container) (typed FeaturePython)
  n = 0.003
FEATURE [App::DocumentObjectGroupPython] K_element002  label="K_element : 0.003"  # scripted group (container) (typed FeaturePython)
  n = 0.003
FEATURE [App::DocumentObjectGroupPython] G4_BRAIN_ICRP  # scripted group (container) (typed FeaturePython)
  Dunit = g/cm3
  Dvalue = 1.04
  Group = -> [H_element017,C_element018,N_element012,O_element017,Na_element004,P_element004,S_element006,Cl_element003,K_element002]
  conduct = 2
  density = 1
  expand = 3
  formula = G4_BRAIN_ICRP
  name = G4_BRAIN_ICRP
  specific = 4
FEATURE [App::DocumentObjectGroupPython] C_element019  label="C_element : 4"  # scripted group (container) (typed FeaturePython)
  n = 4
  ref = C_element
FEATURE [App::DocumentObjectGroupPython] H_element018  label="H_element : 010"  # scripted group (container) (typed FeaturePython)
  n = 10
  ref = H_element
FEATURE [App::DocumentObjectGroupPython] G4_BUTANE  # scripted group (container) (typed FeaturePython)
  Dunit = g/cm3
  Dvalue = 0.00249343
  Group = -> [C_element019,H_element018]
  conduct = 2
  density = 1
  expand = 3
  formula = G4_BUTANE
  name = G4_BUTANE
  specific = 4
FEATURE [App::DocumentObjectGroupPython] C_element020  label="C_element : 008"  # scripted group (container) (typed FeaturePython)
  n = 4
  ref = C_element
FEATURE [App::DocumentObjectGroupPython] H_element019  label="H_element : 011"  # scripted group (container) (typed FeaturePython)
  n = 10
  ref = H_element
FEATURE [App::DocumentObjectGroupPython] O_element018  label="O_element : 007"  # scripted group (container) (typed FeaturePython)
  n = 1
  ref = O_element
FEATURE [App::DocumentObjectGroupPython] G4_N_BUTYL_ALCOHOL  label="G4_N-BUTYL_ALCOHOL"  # scripted group (container) (typed FeaturePython)
  Dunit = g/cm3
  Dvalue = 0.8098
  Group = -> [C_element020,H_element019,O_element018]
  conduct = 2
  density = 1
  expand = 3
  formula = G4_N-BUTYL_ALCOHOL
  name = G4_N-BUTYL_ALCOHOL
  specific = 4
FEATURE [App::DocumentObjectGroupPython] H_element020  label="H_element : 0.025"  # scripted group (container) (typed FeaturePython)
  n = 0.02468
FEATURE [App::DocumentObjectGroupPython] C_element021  label="C_element : 0.502"  # scripted group (container) (typed FeaturePython)
  n = 0.501611
FEATURE [App::DocumentObjectGroupPython] O_element019  label="O_element : 0.005"  # scripted group (container) (typed FeaturePython)
  n = 0.004527
FEATURE [App::DocumentObjectGroupPython] F_element004  label="F_element : 0.465"  # scripted group (container) (typed FeaturePython)
  n = 0.465209
FEATURE [App::DocumentObjectGroupPython] Si_element001  label="Si_element : 0.004"  # scripted group (container) (typed FeaturePython)
  n = 0.003973
FEATURE [App::DocumentObjectGroupPython] G4_C_552  label="G4_C-552"  # scripted group (container) (typed FeaturePython)
  Dunit = g/cm3
  Dvalue = 1.76
  Group = -> [H_element020,C_element021,O_element019,F_element004,Si_element001]
  conduct = 2
  density = 1
  expand = 3
  formula = G4_C-552
  name = G4_C-552
  specific = 4
FEATURE [App::DocumentObjectGroupPython] Cd_element001  label="Cd_element : 1"  # scripted group (container) (typed FeaturePython)
  n = 1
  ref = Cd_element
FEATURE [App::DocumentObjectGroupPython] Te_element001  label="Te_element : 1"  # scripted group (container) (typed FeaturePython)
  n = 1
  ref = Te_element
FEATURE [App::DocumentObjectGroupPython] G4_CADMIUM_TELLURIDE  # scripted group (container) (typed FeaturePython)
  Dunit = g/cm3
  Dvalue = 6.2
  Group = -> [Cd_element001,Te_element001]
  conduct = 2
  density = 1
  expand = 3
  formula = G4_CADMIUM_TELLURIDE
  name = G4_CADMIUM_TELLURIDE
  specific = 4
FEATURE [App::DocumentObjectGroupPython] Cd_element002  label="Cd_element : 002"  # scripted group (container) (typed FeaturePython)
  n = 1
  ref = Cd_element
FEATURE [App::DocumentObjectGroupPython] W_element001  label="W_element : 1"  # scripted group (container) (typed FeaturePython)
  n = 1
  ref = W_element
FEATURE [App::DocumentObjectGroupPython] O_element020  label="O_element : 008"  # scripted group (container) (typed FeaturePython)
  n = 4
  ref = O_element
FEATURE [App::DocumentObjectGroupPython] G4_CADMIUM_TUNGSTATE  # scripted group (container) (typed FeaturePython)
  Dunit = g/cm3
  Dvalue = 7.9
  Group = -> [Cd_element002,W_element001,O_element020]
  conduct = 2
  density = 1
  expand = 3
  formula = G4_CADMIUM_TUNGSTATE
  name = G4_CADMIUM_TUNGSTATE
  specific = 4
FEATURE [App::DocumentObjectGroupPython] Ca_element005  label="Ca_element : 1"  # scripted group (container) (typed FeaturePython)
  n = 1
  ref = Ca_element
FEATURE [App::DocumentObjectGroupPython] C_element022  label="C_element : 009"  # scripted group (container) (typed FeaturePython)
  n = 1
  ref = C_element
FEATURE [App::DocumentObjectGroupPython] O_element021  label="O_element : 009"  # scripted group (container) (typed FeaturePython)
  n = 3
  ref = O_element
FEATURE [App::DocumentObjectGroupPython] G4_CALCIUM_CARBONATE  # scripted group (container) (typed FeaturePython)
  Dunit = g/cm3
  Dvalue = 2.8
  Group = -> [Ca_element005,C_element022,O_element021]
  conduct = 2
  density = 1
  expand = 3
  formula = G4_CALCIUM_CARBONATE
  name = G4_CALCIUM_CARBONATE
  specific = 4
FEATURE [App::DocumentObjectGroupPython] Ca_element006  label="Ca_element : 002"  # scripted group (container) (typed FeaturePython)
  n = 1
  ref = Ca_element
FEATURE [App::DocumentObjectGroupPython] F_element005  label="F_element : 003"  # scripted group (container) (typed FeaturePython)
  n = 2
  ref = F_element
FEATURE [App::DocumentObjectGroupPython] G4_CALCIUM_FLUORIDE  # scripted group (container) (typed FeaturePython)
  Dunit = g/cm3
  Dvalue = 3.18
  Group = -> [Ca_element006,F_element005]
  conduct = 2
  density = 1
  expand = 3
  formula = G4_CALCIUM_FLUORIDE
  name = G4_CALCIUM_FLUORIDE
  specific = 4
FEATURE [App::DocumentObjectGroupPython] Ca_element007  label="Ca_element : 003"  # scripted group (container) (typed FeaturePython)
  n = 1
  ref = Ca_element
FEATURE [App::DocumentObjectGroupPython] O_element022  label="O_element : 010"  # scripted group (container) (typed FeaturePython)
  n = 1
  ref = O_element
FEATURE [App::DocumentObjectGroupPython] G4_CALCIUM_OXIDE  # scripted group (container) (typed FeaturePython)
  Dunit = g/cm3
  Dvalue = 3.3
  Group = -> [Ca_element007,O_element022]
  conduct = 2
  density = 1
  expand = 3
  formula = G4_CALCIUM_OXIDE
  name = G4_CALCIUM_OXIDE
  specific = 4
FEATURE [App::DocumentObjectGroupPython] Ca_element008  label="Ca_element : 004"  # scripted group (container) (typed FeaturePython)
  n = 1
  ref = Ca_element
FEATURE [App::DocumentObjectGroupPython] S_element007  label="S_element : 002"  # scripted group (container) (typed FeaturePython)
  n = 1
  ref = S_element
FEATURE [App::DocumentObjectGroupPython] O_element023  label="O_element : 011"  # scripted group (container) (typed FeaturePython)
  n = 4
  ref = O_element
FEATURE [App::DocumentObjectGroupPython] G4_CALCIUM_SULFATE  # scripted group (container) (typed FeaturePython)
  Dunit = g/cm3
  Dvalue = 2.96
  Group = -> [Ca_element008,S_element007,O_element023]
  conduct = 2
  density = 1
  expand = 3
  formula = G4_CALCIUM_SULFATE
  name = G4_CALCIUM_SULFATE
  specific = 4
FEATURE [App::DocumentObjectGroupPython] Ca_element009  label="Ca_element : 005"  # scripted group (container) (typed FeaturePython)
  n = 1
  ref = Ca_element
FEATURE [App::DocumentObjectGroupPython] W_element002  label="W_element : 002"  # scripted group (container) (typed FeaturePython)
  n = 1
  ref = W_element
FEATURE [App::DocumentObjectGroupPython] O_element024  label="O_element : 012"  # scripted group (container) (typed FeaturePython)
  n = 4
  ref = O_element
FEATURE [App::DocumentObjectGroupPython] G4_CALCIUM_TUNGSTATE  # scripted group (container) (typed FeaturePython)
  Dunit = g/cm3
  Dvalue = 6.062
  Group = -> [Ca_element009,W_element002,O_element024]
  conduct = 2
  density = 1
  expand = 3
  formula = G4_CALCIUM_TUNGSTATE
  name = G4_CALCIUM_TUNGSTATE
  specific = 4
FEATURE [App::DocumentObjectGroupPython] C_element023  label="C_element : 010"  # scripted group (container) (typed FeaturePython)
  n = 1
  ref = C_element
FEATURE [App::DocumentObjectGroupPython] O_element025  label="O_element : 013"  # scripted group (container) (typed FeaturePython)
  n = 2
  ref = O_element
FEATURE [App::DocumentObjectGroupPython] G4_CARBON_DIOXIDE  # scripted group (container) (typed FeaturePython)
  Dunit = g/cm3
  Dvalue = 0.00184212
  Group = -> [C_element023,O_element025]
  conduct = 2
  density = 1
  expand = 3
  formula = G4_CARBON_DIOXIDE
  name = G4_CARBON_DIOXIDE
  specific = 4
FEATURE [App::DocumentObjectGroupPython] C_element024  label="C_element : 011"  # scripted group (container) (typed FeaturePython)
  n = 1
  ref = C_element
FEATURE [App::DocumentObjectGroupPython] Cl_element004  label="Cl_element : 4"  # scripted group (container) (typed FeaturePython)
  n = 4
  ref = Cl_element
FEATURE [App::DocumentObjectGroupPython] G4_CARBON_TETRACHLORIDE  # scripted group (container) (typed FeaturePython)
  Dunit = g/cm3
  Dvalue = 1.594
  Group = -> [C_element024,Cl_element004]
  conduct = 2
  density = 1
  expand = 3
  formula = G4_CARBON_TETRACHLORIDE
  name = G4_CARBON_TETRACHLORIDE
  specific = 4
FEATURE [App::DocumentObjectGroupPython] C_element025  label="C_element : 012"  # scripted group (container) (typed FeaturePython)
  n = 6
  ref = C_element
FEATURE [App::DocumentObjectGroupPython] H_element021  label="H_element : 012"  # scripted group (container) (typed FeaturePython)
  n = 10
  ref = H_element
FEATURE [App::DocumentObjectGroupPython] O_element026  label="O_element : 5"  # scripted group (container) (typed FeaturePython)
  n = 5
  ref = O_element
FEATURE [App::DocumentObjectGroupPython] G4_CELLULOSE_CELLOPHANE  # scripted group (container) (typed FeaturePython)
  Dunit = g/cm3
  Dvalue = 1.42
  Group = -> [C_element025,H_element021,O_element026]
  conduct = 2
  density = 1
  expand = 3
  formula = G4_CELLULOSE_CELLOPHANE
  name = G4_CELLULOSE_CELLOPHANE
  specific = 4
FEATURE [App::DocumentObjectGroupPython] H_element022  label="H_element : 0.067"  # scripted group (container) (typed FeaturePython)
  n = 0.067125
FEATURE [App::DocumentObjectGroupPython] C_element026  label="C_element : 0.545"  # scripted group (container) (typed FeaturePython)
  n = 0.545403
FEATURE [App::DocumentObjectGroupPython] O_element027  label="O_element : 0.387"  # scripted group (container) (typed FeaturePython)
  n = 0.387472
FEATURE [App::DocumentObjectGroupPython] G4_CELLULOSE_BUTYRATE  # scripted group (container) (typed FeaturePython)
  Dunit = g/cm3
  Dvalue = 1.2
  Group = -> [H_element022,C_element026,O_element027]
  conduct = 2
  density = 1
  expand = 3
  formula = G4_CELLULOSE_BUTYRATE
  name = G4_CELLULOSE_BUTYRATE
  specific = 4
FEATURE [App::DocumentObjectGroupPython] H_element023  label="H_element : 0.029"  # scripted group (container) (typed FeaturePython)
  n = 0.029216
FEATURE [App::DocumentObjectGroupPython] C_element027  label="C_element : 0.271"  # scripted group (container) (typed FeaturePython)
  n = 0.271296
FEATURE [App::DocumentObjectGroupPython] N_element013  label="N_element : 0.121"  # scripted group (container) (typed FeaturePython)
  n = 0.121276
FEATURE [App::DocumentObjectGroupPython] O_element028  label="O_element : 0.578"  # scripted group (container) (typed FeaturePython)
  n = 0.578212
FEATURE [App::DocumentObjectGroupPython] G4_CELLULOSE_NITRATE  # scripted group (container) (typed FeaturePython)
  Dunit = g/cm3
  Dvalue = 1.49
  Group = -> [H_element023,C_element027,N_element013,O_element028]
  conduct = 2
  density = 1
  expand = 3
  formula = G4_CELLULOSE_NITRATE
  name = G4_CELLULOSE_NITRATE
  specific = 4
FEATURE [App::DocumentObjectGroupPython] H_element024  label="H_element : 0.108"  # scripted group (container) (typed FeaturePython)
  n = 0.107596
FEATURE [App::DocumentObjectGroupPython] N_element014  label="N_element : 0.001"  # scripted group (container) (typed FeaturePython)
  n = 0.0008
FEATURE [App::DocumentObjectGroupPython] O_element029  label="O_element : 0.875"  # scripted group (container) (typed FeaturePython)
  n = 0.874976
FEATURE [App::DocumentObjectGroupPython] S_element008  label="S_element : 0.015"  # scripted group (container) (typed FeaturePython)
  n = 0.014627
FEATURE [App::DocumentObjectGroupPython] Ce_element001  label="Ce_element : 0.002"  # scripted group (container) (typed FeaturePython)
  n = 0.002001
FEATURE [App::DocumentObjectGroupPython] G4_CERIC_SULFATE  # scripted group (container) (typed FeaturePython)
  Dunit = g/cm3
  Dvalue = 1.03
  Group = -> [H_element024,N_element014,O_element029,S_element008,Ce_element001]
  conduct = 2
  density = 1
  expand = 3
  formula = G4_CERIC_SULFATE
  name = G4_CERIC_SULFATE
  specific = 4
FEATURE [App::DocumentObjectGroupPython] Cs_element001  label="Cs_element : 1"  # scripted group (container) (typed FeaturePython)
  n = 1
  ref = Cs_element
FEATURE [App::DocumentObjectGroupPython] F_element006  label="F_element : 1"  # scripted group (container) (typed FeaturePython)
  n = 1
  ref = F_element
FEATURE [App::DocumentObjectGroupPython] G4_CESIUM_FLUORIDE  # scripted group (container) (typed FeaturePython)
  Dunit = g/cm3
  Dvalue = 4.115
  Group = -> [Cs_element001,F_element006]
  conduct = 2
  density = 1
  expand = 3
  formula = G4_CESIUM_FLUORIDE
  name = G4_CESIUM_FLUORIDE
  specific = 4
FEATURE [App::DocumentObjectGroupPython] Cs_element002  label="Cs_element : 002"  # scripted group (container) (typed FeaturePython)
  n = 1
  ref = Cs_element
FEATURE [App::DocumentObjectGroupPython] I_element001  label="I_element : 1"  # scripted group (container) (typed FeaturePython)
  n = 1
  ref = I_element
FEATURE [App::DocumentObjectGroupPython] G4_CESIUM_IODIDE  # scripted group (container) (typed FeaturePython)
  Dunit = g/cm3
  Dvalue = 4.51
  Group = -> [Cs_element002,I_element001]
  conduct = 2
  density = 1
  expand = 3
  formula = G4_CESIUM_IODIDE
  name = G4_CESIUM_IODIDE
  specific = 4
FEATURE [App::DocumentObjectGroupPython] C_element028  label="C_element : 013"  # scripted group (container) (typed FeaturePython)
  n = 6
  ref = C_element
FEATURE [App::DocumentObjectGroupPython] H_element025  label="H_element : 013"  # scripted group (container) (typed FeaturePython)
  n = 5
  ref = H_element
FEATURE [App::DocumentObjectGroupPython] Cl_element005  label="Cl_element : 1"  # scripted group (container) (typed FeaturePython)
  n = 1
  ref = Cl_element
FEATURE [App::DocumentObjectGroupPython] G4_CHLOROBENZENE  # scripted group (container) (typed FeaturePython)
  Dunit = g/cm3
  Dvalue = 1.1058
  Group = -> [C_element028,H_element025,Cl_element005]
  conduct = 2
  density = 1
  expand = 3
  formula = G4_CHLOROBENZENE
  name = G4_CHLOROBENZENE
  specific = 4
FEATURE [App::DocumentObjectGroupPython] C_element029  label="C_element : 014"  # scripted group (container) (typed FeaturePython)
  n = 1
  ref = C_element
FEATURE [App::DocumentObjectGroupPython] H_element026  label="H_element : 1"  # scripted group (container) (typed FeaturePython)
  n = 1
  ref = H_element
FEATURE [App::DocumentObjectGroupPython] Cl_element006  label="Cl_element : 3"  # scripted group (container) (typed FeaturePython)
  n = 3
  ref = Cl_element
FEATURE [App::DocumentObjectGroupPython] G4_CHLOROFORM  # scripted group (container) (typed FeaturePython)
  Dunit = g/cm3
  Dvalue = 1.4832
  Group = -> [C_element029,H_element026,Cl_element006]
  conduct = 2
  density = 1
  expand = 3
  formula = G4_CHLOROFORM
  name = G4_CHLOROFORM
  specific = 4
FEATURE [App::DocumentObjectGroupPython] H_element027  label="H_element : 0.010"  # scripted group (container) (typed FeaturePython)
  n = 0.01
FEATURE [App::DocumentObjectGroupPython] C_element030  label="C_element : 0.001"  # scripted group (container) (typed FeaturePython)
  n = 0.001
FEATURE [App::DocumentObjectGroupPython] O_element030  label="O_element : 0.529"  # scripted group (container) (typed FeaturePython)
  n = 0.529107
FEATURE [App::DocumentObjectGroupPython] Na_element005  label="Na_element : 0.016"  # scripted group (container) (typed FeaturePython)
  n = 0.016
FEATURE [App::DocumentObjectGroupPython] Mg_element003  label="Mg_element : 0.004"  # scripted group (container) (typed FeaturePython)
  n = 0.002
FEATURE [App::DocumentObjectGroupPython] Al_element002  label="Al_element : 0.034"  # scripted group (container) (typed FeaturePython)
  n = 0.033872
FEATURE [App::DocumentObjectGroupPython] Si_element002  label="Si_element : 0.337"  # scripted group (container) (typed FeaturePython)
  n = 0.337021
FEATURE [App::DocumentObjectGroupPython] K_element003  label="K_element : 0.013"  # scripted group (container) (typed FeaturePython)
  n = 0.013
FEATURE [App::DocumentObjectGroupPython] Ca_element010  label="Ca_element : 0.044"  # scripted group (container) (typed FeaturePython)
  n = 0.044
FEATURE [App::DocumentObjectGroupPython] Fe_element002  label="Fe_element : 0.014"  # scripted group (container) (typed FeaturePython)
  n = 0.014
FEATURE [App::DocumentObjectGroupPython] G4_CONCRETE  # scripted group (container) (typed FeaturePython)
  Dunit = g/cm3
  Dvalue = 2.3
  Group = -> [H_element027,C_element030,O_element030,Na_element005,Mg_element003,Al_element002,Si_element002,K_element003,Ca_element010,Fe_element002]
  conduct = 2
  density = 1
  expand = 3
  formula = G4_CONCRETE
  name = G4_CONCRETE
  specific = 4
FEATURE [App::DocumentObjectGroupPython] C_element031  label="C_element : 015"  # scripted group (container) (typed FeaturePython)
  n = 6
  ref = C_element
FEATURE [App::DocumentObjectGroupPython] H_element028  label="H_element : 12"  # scripted group (container) (typed FeaturePython)
  n = 12
  ref = H_element
FEATURE [App::DocumentObjectGroupPython] G4_CYCLOHEXANE  # scripted group (container) (typed FeaturePython)
  Dunit = g/cm3
  Dvalue = 0.779
  Group = -> [C_element031,H_element028]
  conduct = 2
  density = 1
  expand = 3
  formula = G4_CYCLOHEXANE
  name = G4_CYCLOHEXANE
  specific = 4
FEATURE [App::DocumentObjectGroupPython] C_element032  label="C_element : 016"  # scripted group (container) (typed FeaturePython)
  n = 6
  ref = C_element
FEATURE [App::DocumentObjectGroupPython] H_element029  label="H_element : 4"  # scripted group (container) (typed FeaturePython)
  n = 4
  ref = H_element
FEATURE [App::DocumentObjectGroupPython] Cl_element007  label="Cl_element : 2"  # scripted group (container) (typed FeaturePython)
  n = 2
  ref = Cl_element
FEATURE [App::DocumentObjectGroupPython] G4_1_2_DICHLOROBENZENE  label="G4_1.2-DICHLOROBENZENE"  # scripted group (container) (typed FeaturePython)
  Dunit = g/cm3
  Dvalue = 1.3048
  Group = -> [C_element032,H_element029,Cl_element007]
  conduct = 2
  density = 1
  expand = 3
  formula = G4_1.2-DICHLOROBENZENE
  name = G4_1.2-DICHLOROBENZENE
  specific = 4
FEATURE [App::DocumentObjectGroupPython] C_element033  label="C_element : 017"  # scripted group (container) (typed FeaturePython)
  n = 4
  ref = C_element
FEATURE [App::DocumentObjectGroupPython] H_element030  label="H_element : 8"  # scripted group (container) (typed FeaturePython)
  n = 8
  ref = H_element
FEATURE [App::DocumentObjectGroupPython] O_element031  label="O_element : 014"  # scripted group (container) (typed FeaturePython)
  n = 1
  ref = O_element
FEATURE [App::DocumentObjectGroupPython] Cl_element008  label="Cl_element : 005"  # scripted group (container) (typed FeaturePython)
  n = 2
  ref = Cl_element
FEATURE [App::DocumentObjectGroupPython] G4_DICHLORODIETHYL_ETHER  # scripted group (container) (typed FeaturePython)
  Dunit = g/cm3
  Dvalue = 1.2199
  Group = -> [C_element033,H_element030,O_element031,Cl_element008]
  conduct = 2
  density = 1
  expand = 3
  formula = G4_DICHLORODIETHYL_ETHER
  name = G4_DICHLORODIETHYL_ETHER
  specific = 4
FEATURE [App::DocumentObjectGroupPython] C_element034  label="C_element : 018"  # scripted group (container) (typed FeaturePython)
  n = 2
  ref = C_element
FEATURE [App::DocumentObjectGroupPython] H_element031  label="H_element : 014"  # scripted group (container) (typed FeaturePython)
  n = 4
  ref = H_element
FEATURE [App::DocumentObjectGroupPython] Cl_element009  label="Cl_element : 006"  # scripted group (container) (typed FeaturePython)
  n = 2
  ref = Cl_element
FEATURE [App::DocumentObjectGroupPython] G4_1_2_DICHLOROETHANE  label="G4_1.2-DICHLOROETHANE"  # scripted group (container) (typed FeaturePython)
  Dunit = g/cm3
  Dvalue = 1.2351
  Group = -> [C_element034,H_element031,Cl_element009]
  conduct = 2
  density = 1
  expand = 3
  formula = G4_1.2-DICHLOROETHANE
  name = G4_1.2-DICHLOROETHANE
  specific = 4
FEATURE [App::DocumentObjectGroupPython] C_element035  label="C_element : 019"  # scripted group (container) (typed FeaturePython)
  n = 4
  ref = C_element
FEATURE [App::DocumentObjectGroupPython] H_element032  label="H_element : 015"  # scripted group (container) (typed FeaturePython)
  n = 10
  ref = H_element
FEATURE [App::DocumentObjectGroupPython] O_element032  label="O_element : 015"  # scripted group (container) (typed FeaturePython)
  n = 1
  ref = O_element
FEATURE [App::DocumentObjectGroupPython] G4_DIETHYL_ETHER  # scripted group (container) (typed FeaturePython)
  Dunit = g/cm3
  Dvalue = 0.71378
  Group = -> [C_element035,H_element032,O_element032]
  conduct = 2
  density = 1
  expand = 3
  formula = G4_DIETHYL_ETHER
  name = G4_DIETHYL_ETHER
  specific = 4
FEATURE [App::DocumentObjectGroupPython] C_element036  label="C_element : 020"  # scripted group (container) (typed FeaturePython)
  n = 3
  ref = C_element
FEATURE [App::DocumentObjectGroupPython] H_element033  label="H_element : 016"  # scripted group (container) (typed FeaturePython)
  n = 7
  ref = H_element
FEATURE [App::DocumentObjectGroupPython] N_element015  label="N_element : 008"  # scripted group (container) (typed FeaturePython)
  n = 1
  ref = N_element
FEATURE [App::DocumentObjectGroupPython] O_element033  label="O_element : 016"  # scripted group (container) (typed FeaturePython)
  n = 1
  ref = O_element
FEATURE [App::DocumentObjectGroupPython] G4_N_N_DIMETHYL_FORMAMIDE  label="G4_N.N-DIMETHYL_FORMAMIDE"  # scripted group (container) (typed FeaturePython)
  Dunit = g/cm3
  Dvalue = 0.9487
  Group = -> [C_element036,H_element033,N_element015,O_element033]
  conduct = 2
  density = 1
  expand = 3
  formula = G4_N.N-DIMETHYL_FORMAMIDE
  name = G4_N.N-DIMETHYL_FORMAMIDE
  specific = 4
FEATURE [App::DocumentObjectGroupPython] C_element037  label="C_element : 021"  # scripted group (container) (typed FeaturePython)
  n = 2
  ref = C_element
FEATURE [App::DocumentObjectGroupPython] H_element034  label="H_element : 017"  # scripted group (container) (typed FeaturePython)
  n = 6
  ref = H_element
FEATURE [App::DocumentObjectGroupPython] O_element034  label="O_element : 017"  # scripted group (container) (typed FeaturePython)
  n = 1
  ref = O_element
FEATURE [App::DocumentObjectGroupPython] S_element009  label="S_element : 003"  # scripted group (container) (typed FeaturePython)
  n = 1
  ref = S_element
FEATURE [App::DocumentObjectGroupPython] G4_DIMETHYL_SULFOXIDE  # scripted group (container) (typed FeaturePython)
  Dunit = g/cm3
  Dvalue = 1.1014
  Group = -> [C_element037,H_element034,O_element034,S_element009]
  conduct = 2
  density = 1
  expand = 3
  formula = G4_DIMETHYL_SULFOXIDE
  name = G4_DIMETHYL_SULFOXIDE
  specific = 4
FEATURE [App::DocumentObjectGroupPython] C_element038  label="C_element : 022"  # scripted group (container) (typed FeaturePython)
  n = 2
  ref = C_element
FEATURE [App::DocumentObjectGroupPython] H_element035  label="H_element : 018"  # scripted group (container) (typed FeaturePython)
  n = 6
  ref = H_element
FEATURE [App::DocumentObjectGroupPython] G4_ETHANE  # scripted group (container) (typed FeaturePython)
  Dunit = g/cm3
  Dvalue = 0.00125324
  Group = -> [C_element038,H_element035]
  conduct = 2
  density = 1
  expand = 3
  formula = G4_ETHANE
  name = G4_ETHANE
  specific = 4
FEATURE [App::DocumentObjectGroupPython] C_element039  label="C_element : 023"  # scripted group (container) (typed FeaturePython)
  n = 2
  ref = C_element
FEATURE [App::DocumentObjectGroupPython] H_element036  label="H_element : 019"  # scripted group (container) (typed FeaturePython)
  n = 6
  ref = H_element
FEATURE [App::DocumentObjectGroupPython] O_element035  label="O_element : 018"  # scripted group (container) (typed FeaturePython)
  n = 1
  ref = O_element
FEATURE [App::DocumentObjectGroupPython] G4_ETHYL_ALCOHOL  # scripted group (container) (typed FeaturePython)
  Dunit = g/cm3
  Dvalue = 0.7893
  Group = -> [C_element039,H_element036,O_element035]
  conduct = 2
  density = 1
  expand = 3
  formula = G4_ETHYL_ALCOHOL
  name = G4_ETHYL_ALCOHOL
  specific = 4
FEATURE [App::DocumentObjectGroupPython] H_element037  label="H_element : 0.090"  # scripted group (container) (typed FeaturePython)
  n = 0.090027
FEATURE [App::DocumentObjectGroupPython] C_element040  label="C_element : 0.585"  # scripted group (container) (typed FeaturePython)
  n = 0.585182
FEATURE [App::DocumentObjectGroupPython] O_element036  label="O_element : 0.325"  # scripted group (container) (typed FeaturePython)
  n = 0.324791
FEATURE [App::DocumentObjectGroupPython] G4_ETHYL_CELLULOSE  # scripted group (container) (typed FeaturePython)
  Dunit = g/cm3
  Dvalue = 1.13
  Group = -> [H_element037,C_element040,O_element036]
  conduct = 2
  density = 1
  expand = 3
  formula = G4_ETHYL_CELLULOSE
  name = G4_ETHYL_CELLULOSE
  specific = 4
FEATURE [App::DocumentObjectGroupPython] C_element041  label="C_element : 024"  # scripted group (container) (typed FeaturePython)
  n = 2
  ref = C_element
FEATURE [App::DocumentObjectGroupPython] H_element038  label="H_element : 020"  # scripted group (container) (typed FeaturePython)
  n = 4
  ref = H_element
FEATURE [App::DocumentObjectGroupPython] G4_ETHYLENE  # scripted group (container) (typed FeaturePython)
  Dunit = g/cm3
  Dvalue = 0.00117497
  Group = -> [C_element041,H_element038]
  conduct = 2
  density = 1
  expand = 3
  formula = G4_ETHYLENE
  name = G4_ETHYLENE
  specific = 4
FEATURE [App::DocumentObjectGroupPython] H_element039  label="H_element : 0.096"  # scripted group (container) (typed FeaturePython)
  n = 0.096
FEATURE [App::DocumentObjectGroupPython] C_element042  label="C_element : 0.195"  # scripted group (container) (typed FeaturePython)
  n = 0.195
FEATURE [App::DocumentObjectGroupPython] N_element016  label="N_element : 0.057"  # scripted group (container) (typed FeaturePython)
  n = 0.057
FEATURE [App::DocumentObjectGroupPython] O_element037  label="O_element : 0.646"  # scripted group (container) (typed FeaturePython)
  n = 0.646
FEATURE [App::DocumentObjectGroupPython] Na_element006  label="Na_element : 0.017"  # scripted group (container) (typed FeaturePython)
  n = 0.001
FEATURE [App::DocumentObjectGroupPython] P_element005  label="P_element : 0.104"  # scripted group (container) (typed FeaturePython)
  n = 0.001
FEATURE [App::DocumentObjectGroupPython] S_element010  label="S_element : 0.016"  # scripted group (container) (typed FeaturePython)
  n = 0.003
FEATURE [App::DocumentObjectGroupPython] Cl_element010  label="Cl_element : 0.005"  # scripted group (container) (typed FeaturePython)
  n = 0.001
FEATURE [App::DocumentObjectGroupPython] G4_EYE_LENS_ICRP  # scripted group (container) (typed FeaturePython)
  Dunit = g/cm3
  Dvalue = 1.07
  Group = -> [H_element039,C_element042,N_element016,O_element037,Na_element006,P_element005,S_element010,Cl_element010]
  conduct = 2
  density = 1
  expand = 3
  formula = G4_EYE_LENS_ICRP
  name = G4_EYE_LENS_ICRP
  specific = 4
FEATURE [App::DocumentObjectGroupPython] Fe_element003  label="Fe_element : 2"  # scripted group (container) (typed FeaturePython)
  n = 2
  ref = Fe_element
FEATURE [App::DocumentObjectGroupPython] O_element038  label="O_element : 019"  # scripted group (container) (typed FeaturePython)
  n = 3
  ref = O_element
FEATURE [App::DocumentObjectGroupPython] G4_FERRIC_OXIDE  # scripted group (container) (typed FeaturePython)
  Dunit = g/cm3
  Dvalue = 5.2
  Group = -> [Fe_element003,O_element038]
  conduct = 2
  density = 1
  expand = 3
  formula = G4_FERRIC_OXIDE
  name = G4_FERRIC_OXIDE
  specific = 4
FEATURE [App::DocumentObjectGroupPython] Fe_element004  label="Fe_element : 1"  # scripted group (container) (typed FeaturePython)
  n = 1
  ref = Fe_element
FEATURE [App::DocumentObjectGroupPython] B_element003  label="B_element : 1"  # scripted group (container) (typed FeaturePython)
  n = 1
  ref = B_element
FEATURE [App::DocumentObjectGroupPython] G4_FERROBORIDE  # scripted group (container) (typed FeaturePython)
  Dunit = g/cm3
  Dvalue = 7.15
  Group = -> [Fe_element004,B_element003]
  conduct = 2
  density = 1
  expand = 3
  formula = G4_FERROBORIDE
  name = G4_FERROBORIDE
  specific = 4
FEATURE [App::DocumentObjectGroupPython] Fe_element005  label="Fe_element : 003"  # scripted group (container) (typed FeaturePython)
  n = 1
  ref = Fe_element
FEATURE [App::DocumentObjectGroupPython] O_element039  label="O_element : 020"  # scripted group (container) (typed FeaturePython)
  n = 1
  ref = O_element
FEATURE [App::DocumentObjectGroupPython] G4_FERROUS_OXIDE  # scripted group (container) (typed FeaturePython)
  Dunit = g/cm3
  Dvalue = 5.7
  Group = -> [Fe_element005,O_element039]
  conduct = 2
  density = 1
  expand = 3
  formula = G4_FERROUS_OXIDE
  name = G4_FERROUS_OXIDE
  specific = 4
FEATURE [App::DocumentObjectGroupPython] H_element040  label="H_element : 0.115"  # scripted group (container) (typed FeaturePython)
  n = 0.108259
FEATURE [App::DocumentObjectGroupPython] N_element017  label="N_element : 0.000"  # scripted group (container) (typed FeaturePython)
  n = 2.7e-05
FEATURE [App::DocumentObjectGroupPython] O_element040  label="O_element : 0.879"  # scripted group (container) (typed FeaturePython)
  n = 0.878636
FEATURE [App::DocumentObjectGroupPython] Na_element007  label="Na_element : 0.000"  # scripted group (container) (typed FeaturePython)
  n = 2.2e-05
FEATURE [App::DocumentObjectGroupPython] S_element011  label="S_element : 0.013"  # scripted group (container) (typed FeaturePython)
  n = 0.012968
FEATURE [App::DocumentObjectGroupPython] Cl_element011  label="Cl_element : 0.000"  # scripted group (container) (typed FeaturePython)
  n = 3.4e-05
FEATURE [App::DocumentObjectGroupPython] Fe_element006  label="Fe_element : 0.000"  # scripted group (container) (typed FeaturePython)
  n = 5.4e-05
FEATURE [App::DocumentObjectGroupPython] G4_FERROUS_SULFATE  # scripted group (container) (typed FeaturePython)
  Dunit = g/cm3
  Dvalue = 1.024
  Group = -> [H_element040,N_element017,O_element040,Na_element007,S_element011,Cl_element011,Fe_element006]
  conduct = 2
  density = 1
  expand = 3
  formula = G4_FERROUS_SULFATE
  name = G4_FERROUS_SULFATE
  specific = 4
FEATURE [App::DocumentObjectGroupPython] C_element043  label="C_element : 0.099"  # scripted group (container) (typed FeaturePython)
  n = 0.099335
FEATURE [App::DocumentObjectGroupPython] F_element007  label="F_element : 0.314"  # scripted group (container) (typed FeaturePython)
  n = 0.314247
FEATURE [App::DocumentObjectGroupPython] Cl_element012  label="Cl_element : 0.586"  # scripted group (container) (typed FeaturePython)
  n = 0.586418
FEATURE [App::DocumentObjectGroupPython] G4_FREON_12  label="G4_FREON-12"  # scripted group (container) (typed FeaturePython)
  Dunit = g/cm3
  Dvalue = 1.12
  Group = -> [C_element043,F_element007,Cl_element012]
  conduct = 2
  density = 1
  expand = 3
  formula = G4_FREON-12
  name = G4_FREON-12
  specific = 4
FEATURE [App::DocumentObjectGroupPython] C_element044  label="C_element : 0.057"  # scripted group (container) (typed FeaturePython)
  n = 0.057245
FEATURE [App::DocumentObjectGroupPython] F_element008  label="F_element : 0.181"  # scripted group (container) (typed FeaturePython)
  n = 0.181096
FEATURE [App::DocumentObjectGroupPython] Br_element001  label="Br_element : 0.762"  # scripted group (container) (typed FeaturePython)
  n = 0.761659
FEATURE [App::DocumentObjectGroupPython] G4_FREON_12B2  label="G4_FREON-12B2"  # scripted group (container) (typed FeaturePython)
  Dunit = g/cm3
  Dvalue = 1.8
  Group = -> [C_element044,F_element008,Br_element001]
  conduct = 2
  density = 1
  expand = 3
  formula = G4_FREON-12B2
  name = G4_FREON-12B2
  specific = 4
FEATURE [App::DocumentObjectGroupPython] C_element045  label="C_element : 0.115"  # scripted group (container) (typed FeaturePython)
  n = 0.114983
FEATURE [App::DocumentObjectGroupPython] F_element009  label="F_element : 0.546"  # scripted group (container) (typed FeaturePython)
  n = 0.545621
FEATURE [App::DocumentObjectGroupPython] Cl_element013  label="Cl_element : 0.339"  # scripted group (container) (typed FeaturePython)
  n = 0.339396
FEATURE [App::DocumentObjectGroupPython] G4_FREON_13  label="G4_FREON-13"  # scripted group (container) (typed FeaturePython)
  Dunit = g/cm3
  Dvalue = 0.95
  Group = -> [C_element045,F_element009,Cl_element013]
  conduct = 2
  density = 1
  expand = 3
  formula = G4_FREON-13
  name = G4_FREON-13
  specific = 4
FEATURE [App::DocumentObjectGroupPython] C_element046  label="C_element : 025"  # scripted group (container) (typed FeaturePython)
  n = 1
  ref = C_element
FEATURE [App::DocumentObjectGroupPython] F_element010  label="F_element : 3"  # scripted group (container) (typed FeaturePython)
  n = 3
  ref = F_element
FEATURE [App::DocumentObjectGroupPython] Br_element002  label="Br_element : 1"  # scripted group (container) (typed FeaturePython)
  n = 1
  ref = Br_element
FEATURE [App::DocumentObjectGroupPython] G4_FREON_13B1  label="G4_FREON-13B1"  # scripted group (container) (typed FeaturePython)
  Dunit = g/cm3
  Dvalue = 1.5
  Group = -> [C_element046,F_element010,Br_element002]
  conduct = 2
  density = 1
  expand = 3
  formula = G4_FREON-13B1
  name = G4_FREON-13B1
  specific = 4
FEATURE [App::DocumentObjectGroupPython] C_element047  label="C_element : 0.061"  # scripted group (container) (typed FeaturePython)
  n = 0.061309
FEATURE [App::DocumentObjectGroupPython] F_element011  label="F_element : 0.291"  # scripted group (container) (typed FeaturePython)
  n = 0.290924
FEATURE [App::DocumentObjectGroupPython] I_element002  label="I_element : 0.648"  # scripted group (container) (typed FeaturePython)
  n = 0.647767
FEATURE [App::DocumentObjectGroupPython] G4_FREON_13I1  label="G4_FREON-13I1"  # scripted group (container) (typed FeaturePython)
  Dunit = g/cm3
  Dvalue = 1.8
  Group = -> [C_element047,F_element011,I_element002]
  conduct = 2
  density = 1
  expand = 3
  formula = G4_FREON-13I1
  name = G4_FREON-13I1
  specific = 4
FEATURE [App::DocumentObjectGroupPython] Gd_element001  label="Gd_element : 2"  # scripted group (container) (typed FeaturePython)
  n = 2
  ref = Gd_element
FEATURE [App::DocumentObjectGroupPython] O_element041  label="O_element : 021"  # scripted group (container) (typed FeaturePython)
  n = 2
  ref = O_element
FEATURE [App::DocumentObjectGroupPython] S_element012  label="S_element : 004"  # scripted group (container) (typed FeaturePython)
  n = 1
  ref = S_element
FEATURE [App::DocumentObjectGroupPython] G4_GADOLINIUM_OXYSULFIDE  # scripted group (container) (typed FeaturePython)
  Dunit = g/cm3
  Dvalue = 7.44
  Group = -> [Gd_element001,O_element041,S_element012]
  conduct = 2
  density = 1
  expand = 3
  formula = G4_GADOLINIUM_OXYSULFIDE
  name = G4_GADOLINIUM_OXYSULFIDE
  specific = 4
FEATURE [App::DocumentObjectGroupPython] Ga_element001  label="Ga_element : 1"  # scripted group (container) (typed FeaturePython)
  n = 1
  ref = Ga_element
FEATURE [App::DocumentObjectGroupPython] As_element001  label="As_element : 1"  # scripted group (container) (typed FeaturePython)
  n = 1
  ref = As_element
FEATURE [App::DocumentObjectGroupPython] G4_GALLIUM_ARSENIDE  # scripted group (container) (typed FeaturePython)
  Dunit = g/cm3
  Dvalue = 5.31
  Group = -> [Ga_element001,As_element001]
  conduct = 2
  density = 1
  expand = 3
  formula = G4_GALLIUM_ARSENIDE
  name = G4_GALLIUM_ARSENIDE
  specific = 4
FEATURE [App::DocumentObjectGroupPython] H_element041  label="H_element : 0.081"  # scripted group (container) (typed FeaturePython)
  n = 0.08118
FEATURE [App::DocumentObjectGroupPython] C_element048  label="C_element : 0.416"  # scripted group (container) (typed FeaturePython)
  n = 0.41606
FEATURE [App::DocumentObjectGroupPython] N_element018  label="N_element : 0.111"  # scripted group (container) (typed FeaturePython)
  n = 0.11124
FEATURE [App::DocumentObjectGroupPython] O_element042  label="O_element : 0.381"  # scripted group (container) (typed FeaturePython)
  n = 0.38064
FEATURE [App::DocumentObjectGroupPython] S_element013  label="S_element : 0.011"  # scripted group (container) (typed FeaturePython)
  n = 0.01088
FEATURE [App::DocumentObjectGroupPython] G4_GEL_PHOTO_EMULSION  # scripted group (container) (typed FeaturePython)
  Dunit = g/cm3
  Dvalue = 1.2914
  Group = -> [H_element041,C_element048,N_element018,O_element042,S_element013]
  conduct = 2
  density = 1
  expand = 3
  formula = G4_GEL_PHOTO_EMULSION
  name = G4_GEL_PHOTO_EMULSION
  specific = 4
FEATURE [App::DocumentObjectGroupPython] B_element004  label="B_element : 0.040"  # scripted group (container) (typed FeaturePython)
  n = 0.0400639
FEATURE [App::DocumentObjectGroupPython] O_element043  label="O_element : 0.540"  # scripted group (container) (typed FeaturePython)
  n = 0.539561
FEATURE [App::DocumentObjectGroupPython] Na_element008  label="Na_element : 0.028"  # scripted group (container) (typed FeaturePython)
  n = 0.0281909
FEATURE [App::DocumentObjectGroupPython] Al_element003  label="Al_element : 0.012"  # scripted group (container) (typed FeaturePython)
  n = 0.011644
FEATURE [App::DocumentObjectGroupPython] Si_element003  label="Si_element : 0.377"  # scripted group (container) (typed FeaturePython)
  n = 0.377219
FEATURE [App::DocumentObjectGroupPython] K_element004  label="K_element : 0.014"  # scripted group (container) (typed FeaturePython)
  n = 0.00332099
FEATURE [App::DocumentObjectGroupPython] G4_Pyrex_Glass  # scripted group (container) (typed FeaturePython)
  Dunit = g/cm3
  Dvalue = 2.23
  Group = -> [B_element004,O_element043,Na_element008,Al_element003,Si_element003,K_element004]
  conduct = 2
  density = 1
  expand = 3
  formula = G4_Pyrex_Glass
  name = G4_Pyrex_Glass
  specific = 4
FEATURE [App::DocumentObjectGroupPython] O_element044  label="O_element : 0.156"  # scripted group (container) (typed FeaturePython)
  n = 0.156453
FEATURE [App::DocumentObjectGroupPython] Si_element004  label="Si_element : 0.081"  # scripted group (container) (typed FeaturePython)
  n = 0.080866
FEATURE [App::DocumentObjectGroupPython] Ti_element001  label="Ti_element : 0.008"  # scripted group (container) (typed FeaturePython)
  n = 0.008092
FEATURE [App::DocumentObjectGroupPython] As_element002  label="As_element : 0.003"  # scripted group (container) (typed FeaturePython)
  n = 0.002651
FEATURE [App::DocumentObjectGroupPython] Pb_element001  label="Pb_element : 0.752"  # scripted group (container) (typed FeaturePython)
  n = 0.751938
FEATURE [App::DocumentObjectGroupPython] G4_GLASS_LEAD  # scripted group (container) (typed FeaturePython)
  Dunit = g/cm3
  Dvalue = 6.22
  Group = -> [O_element044,Si_element004,Ti_element001,As_element002,Pb_element001]
  conduct = 2
  density = 1
  expand = 3
  formula = G4_GLASS_LEAD
  name = G4_GLASS_LEAD
  specific = 4
FEATURE [App::DocumentObjectGroupPython] O_element045  label="O_element : 0.460"  # scripted group (container) (typed FeaturePython)
  n = 0.4598
FEATURE [App::DocumentObjectGroupPython] Na_element009  label="Na_element : 0.096"  # scripted group (container) (typed FeaturePython)
  n = 0.0964411
FEATURE [App::DocumentObjectGroupPython] Si_element005  label="Si_element : 0.378"  # scripted group (container) (typed FeaturePython)
  n = 0.336553
FEATURE [App::DocumentObjectGroupPython] Ca_element011  label="Ca_element : 0.107"  # scripted group (container) (typed FeaturePython)
  n = 0.107205
FEATURE [App::DocumentObjectGroupPython] G4_GLASS_PLATE  # scripted group (container) (typed FeaturePython)
  Dunit = g/cm3
  Dvalue = 2.4
  Group = -> [O_element045,Na_element009,Si_element005,Ca_element011]
  conduct = 2
  density = 1
  expand = 3
  formula = G4_GLASS_PLATE
  name = G4_GLASS_PLATE
  specific = 4
FEATURE [App::DocumentObjectGroupPython] C_element049  label="C_element : 026"  # scripted group (container) (typed FeaturePython)
  n = 5
  ref = C_element
FEATURE [App::DocumentObjectGroupPython] H_element042  label="H_element : 021"  # scripted group (container) (typed FeaturePython)
  n = 10
  ref = H_element
FEATURE [App::DocumentObjectGroupPython] N_element019  label="N_element : 2"  # scripted group (container) (typed FeaturePython)
  n = 2
  ref = N_element
FEATURE [App::DocumentObjectGroupPython] O_element046  label="O_element : 022"  # scripted group (container) (typed FeaturePython)
  n = 3
  ref = O_element
FEATURE [App::DocumentObjectGroupPython] G4_GLUTAMINE  # scripted group (container) (typed FeaturePython)
  Dunit = g/cm3
  Dvalue = 1.46
  Group = -> [C_element049,H_element042,N_element019,O_element046]
  conduct = 2
  density = 1
  expand = 3
  formula = G4_GLUTAMINE
  name = G4_GLUTAMINE
  specific = 4
FEATURE [App::DocumentObjectGroupPython] C_element050  label="C_element : 027"  # scripted group (container) (typed FeaturePython)
  n = 3
  ref = C_element
FEATURE [App::DocumentObjectGroupPython] H_element043  label="H_element : 022"  # scripted group (container) (typed FeaturePython)
  n = 8
  ref = H_element
FEATURE [App::DocumentObjectGroupPython] O_element047  label="O_element : 023"  # scripted group (container) (typed FeaturePython)
  n = 3
  ref = O_element
FEATURE [App::DocumentObjectGroupPython] G4_GLYCEROL  # scripted group (container) (typed FeaturePython)
  Dunit = g/cm3
  Dvalue = 1.2613
  Group = -> [C_element050,H_element043,O_element047]
  conduct = 2
  density = 1
  expand = 3
  formula = G4_GLYCEROL
  name = G4_GLYCEROL
  specific = 4
FEATURE [App::DocumentObjectGroupPython] C_element051  label="C_element : 028"  # scripted group (container) (typed FeaturePython)
  n = 5
  ref = C_element
FEATURE [App::DocumentObjectGroupPython] H_element044  label="H_element : 023"  # scripted group (container) (typed FeaturePython)
  n = 5
  ref = H_element
FEATURE [App::DocumentObjectGroupPython] N_element020  label="N_element : 009"  # scripted group (container) (typed FeaturePython)
  n = 5
  ref = N_element
FEATURE [App::DocumentObjectGroupPython] O_element048  label="O_element : 024"  # scripted group (container) (typed FeaturePython)
  n = 1
  ref = O_element
FEATURE [App::DocumentObjectGroupPython] G4_GUANINE  # scripted group (container) (typed FeaturePython)
  Dunit = g/cm3
  Dvalue = 2.2
  Group = -> [C_element051,H_element044,N_element020,O_element048]
  conduct = 2
  density = 1
  expand = 3
  formula = G4_GUANINE
  name = G4_GUANINE
  specific = 4
FEATURE [App::DocumentObjectGroupPython] Ca_element012  label="Ca_element : 006"  # scripted group (container) (typed FeaturePython)
  n = 1
  ref = Ca_element
FEATURE [App::DocumentObjectGroupPython] S_element014  label="S_element : 005"  # scripted group (container) (typed FeaturePython)
  n = 1
  ref = S_element
FEATURE [App::DocumentObjectGroupPython] O_element049  label="O_element : 6"  # scripted group (container) (typed FeaturePython)
  n = 6
  ref = O_element
FEATURE [App::DocumentObjectGroupPython] H_element045  label="H_element : 024"  # scripted group (container) (typed FeaturePython)
  n = 4
  ref = H_element
FEATURE [App::DocumentObjectGroupPython] G4_GYPSUM  # scripted group (container) (typed FeaturePython)
  Dunit = g/cm3
  Dvalue = 2.32
  Group = -> [Ca_element012,S_element014,O_element049,H_element045]
  conduct = 2
  density = 1
  expand = 3
  formula = G4_GYPSUM
  name = G4_GYPSUM
  specific = 4
FEATURE [App::DocumentObjectGroupPython] C_element052  label="C_element : 7"  # scripted group (container) (typed FeaturePython)
  n = 7
  ref = C_element
FEATURE [App::DocumentObjectGroupPython] H_element046  label="H_element : 16"  # scripted group (container) (typed FeaturePython)
  n = 16
  ref = H_element
FEATURE [App::DocumentObjectGroupPython] G4_N_HEPTANE  label="G4_N-HEPTANE"  # scripted group (container) (typed FeaturePython)
  Dunit = g/cm3
  Dvalue = 0.68376
  Group = -> [C_element052,H_element046]
  conduct = 2
  density = 1
  expand = 3
  formula = G4_N-HEPTANE
  name = G4_N-HEPTANE
  specific = 4
FEATURE [App::DocumentObjectGroupPython] C_element053  label="C_element : 029"  # scripted group (container) (typed FeaturePython)
  n = 6
  ref = C_element
FEATURE [App::DocumentObjectGroupPython] H_element047  label="H_element : 14"  # scripted group (container) (typed FeaturePython)
  n = 14
  ref = H_element
FEATURE [App::DocumentObjectGroupPython] G4_N_HEXANE  label="G4_N-HEXANE"  # scripted group (container) (typed FeaturePython)
  Dunit = g/cm3
  Dvalue = 0.6603
  Group = -> [C_element053,H_element047]
  conduct = 2
  density = 1
  expand = 3
  formula = G4_N-HEXANE
  name = G4_N-HEXANE
  specific = 4
FEATURE [App::DocumentObjectGroupPython] C_element054  label="C_element : 22"  # scripted group (container) (typed FeaturePython)
  n = 22
  ref = C_element
FEATURE [App::DocumentObjectGroupPython] H_element048  label="H_element : 025"  # scripted group (container) (typed FeaturePython)
  n = 10
  ref = H_element
FEATURE [App::DocumentObjectGroupPython] N_element021  label="N_element : 010"  # scripted group (container) (typed FeaturePython)
  n = 2
  ref = N_element
FEATURE [App::DocumentObjectGroupPython] O_element050  label="O_element : 025"  # scripted group (container) (typed FeaturePython)
  n = 5
  ref = O_element
FEATURE [App::DocumentObjectGroupPython] G4_KAPTON  # scripted group (container) (typed FeaturePython)
  Dunit = g/cm3
  Dvalue = 1.42
  Group = -> [C_element054,H_element048,N_element021,O_element050]
  conduct = 2
  density = 1
  expand = 3
  formula = G4_KAPTON
  name = G4_KAPTON
  specific = 4
FEATURE [App::DocumentObjectGroupPython] La_element001  label="La_element : 1"  # scripted group (container) (typed FeaturePython)
  n = 1
  ref = La_element
FEATURE [App::DocumentObjectGroupPython] Br_element003  label="Br_element : 002"  # scripted group (container) (typed FeaturePython)
  n = 1
  ref = Br_element
FEATURE [App::DocumentObjectGroupPython] O_element051  label="O_element : 026"  # scripted group (container) (typed FeaturePython)
  n = 1
  ref = O_element
FEATURE [App::DocumentObjectGroupPython] G4_LANTHANUM_OXYBROMIDE  # scripted group (container) (typed FeaturePython)
  Dunit = g/cm3
  Dvalue = 6.28
  Group = -> [La_element001,Br_element003,O_element051]
  conduct = 2
  density = 1
  expand = 3
  formula = G4_LANTHANUM_OXYBROMIDE
  name = G4_LANTHANUM_OXYBROMIDE
  specific = 4
FEATURE [App::DocumentObjectGroupPython] La_element002  label="La_element : 2"  # scripted group (container) (typed FeaturePython)
  n = 2
  ref = La_element
FEATURE [App::DocumentObjectGroupPython] O_element052  label="O_element : 027"  # scripted group (container) (typed FeaturePython)
  n = 2
  ref = O_element
FEATURE [App::DocumentObjectGroupPython] S_element015  label="S_element : 006"  # scripted group (container) (typed FeaturePython)
  n = 1
  ref = S_element
FEATURE [App::DocumentObjectGroupPython] G4_LANTHANUM_OXYSULFIDE  # scripted group (container) (typed FeaturePython)
  Dunit = g/cm3
  Dvalue = 5.86
  Group = -> [La_element002,O_element052,S_element015]
  conduct = 2
  density = 1
  expand = 3
  formula = G4_LANTHANUM_OXYSULFIDE
  name = G4_LANTHANUM_OXYSULFIDE
  specific = 4
FEATURE [App::DocumentObjectGroupPython] O_element053  label="O_element : 0.072"  # scripted group (container) (typed FeaturePython)
  n = 0.071682
FEATURE [App::DocumentObjectGroupPython] Pb_element002  label="Pb_element : 0.928"  # scripted group (container) (typed FeaturePython)
  n = 0.928318
FEATURE [App::DocumentObjectGroupPython] G4_LEAD_OXIDE  # scripted group (container) (typed FeaturePython)
  Dunit = g/cm3
  Dvalue = 9.53
  Group = -> [O_element053,Pb_element002]
  conduct = 2
  density = 1
  expand = 3
  formula = G4_LEAD_OXIDE
  name = G4_LEAD_OXIDE
  specific = 4
FEATURE [App::DocumentObjectGroupPython] Li_element001  label="Li_element : 1"  # scripted group (container) (typed FeaturePython)
  n = 1
  ref = Li_element
FEATURE [App::DocumentObjectGroupPython] N_element022  label="N_element : 011"  # scripted group (container) (typed FeaturePython)
  n = 1
  ref = N_element
FEATURE [App::DocumentObjectGroupPython] H_element049  label="H_element : 026"  # scripted group (container) (typed FeaturePython)
  n = 2
  ref = H_element
FEATURE [App::DocumentObjectGroupPython] G4_LITHIUM_AMIDE  # scripted group (container) (typed FeaturePython)
  Dunit = g/cm3
  Dvalue = 1.178
  Group = -> [Li_element001,N_element022,H_element049]
  conduct = 2
  density = 1
  expand = 3
  formula = G4_LITHIUM_AMIDE
  name = G4_LITHIUM_AMIDE
  specific = 4
FEATURE [App::DocumentObjectGroupPython] Li_element002  label="Li_element : 2"  # scripted group (container) (typed FeaturePython)
  n = 2
  ref = Li_element
FEATURE [App::DocumentObjectGroupPython] C_element055  label="C_element : 030"  # scripted group (container) (typed FeaturePython)
  n = 1
  ref = C_element
FEATURE [App::DocumentObjectGroupPython] O_element054  label="O_element : 028"  # scripted group (container) (typed FeaturePython)
  n = 3
  ref = O_element
FEATURE [App::DocumentObjectGroupPython] G4_LITHIUM_CARBONATE  # scripted group (container) (typed FeaturePython)
  Dunit = g/cm3
  Dvalue = 2.11
  Group = -> [Li_element002,C_element055,O_element054]
  conduct = 2
  density = 1
  expand = 3
  formula = G4_LITHIUM_CARBONATE
  name = G4_LITHIUM_CARBONATE
  specific = 4
FEATURE [App::DocumentObjectGroupPython] Li_element003  label="Li_element : 003"  # scripted group (container) (typed FeaturePython)
  n = 1
  ref = Li_element
FEATURE [App::DocumentObjectGroupPython] F_element012  label="F_element : 004"  # scripted group (container) (typed FeaturePython)
  n = 1
  ref = F_element
FEATURE [App::DocumentObjectGroupPython] G4_LITHIUM_FLUORIDE  # scripted group (container) (typed FeaturePython)
  Dunit = g/cm3
  Dvalue = 2.635
  Group = -> [Li_element003,F_element012]
  conduct = 2
  density = 1
  expand = 3
  formula = G4_LITHIUM_FLUORIDE
  name = G4_LITHIUM_FLUORIDE
  specific = 4
FEATURE [App::DocumentObjectGroupPython] Li_element004  label="Li_element : 004"  # scripted group (container) (typed FeaturePython)
  n = 1
  ref = Li_element
FEATURE [App::DocumentObjectGroupPython] H_element050  label="H_element : 027"  # scripted group (container) (typed FeaturePython)
  n = 1
  ref = H_element
FEATURE [App::DocumentObjectGroupPython] G4_LITHIUM_HYDRIDE  # scripted group (container) (typed FeaturePython)
  Dunit = g/cm3
  Dvalue = 0.82
  Group = -> [Li_element004,H_element050]
  conduct = 2
  density = 1
  expand = 3
  formula = G4_LITHIUM_HYDRIDE
  name = G4_LITHIUM_HYDRIDE
  specific = 4
FEATURE [App::DocumentObjectGroupPython] Li_element005  label="Li_element : 005"  # scripted group (container) (typed FeaturePython)
  n = 1
  ref = Li_element
FEATURE [App::DocumentObjectGroupPython] I_element003  label="I_element : 002"  # scripted group (container) (typed FeaturePython)
  n = 1
  ref = I_element
FEATURE [App::DocumentObjectGroupPython] G4_LITHIUM_IODIDE  # scripted group (container) (typed FeaturePython)
  Dunit = g/cm3
  Dvalue = 3.494
  Group = -> [Li_element005,I_element003]
  conduct = 2
  density = 1
  expand = 3
  formula = G4_LITHIUM_IODIDE
  name = G4_LITHIUM_IODIDE
  specific = 4
FEATURE [App::DocumentObjectGroupPython] Li_element006  label="Li_element : 006"  # scripted group (container) (typed FeaturePython)
  n = 2
  ref = Li_element
FEATURE [App::DocumentObjectGroupPython] O_element055  label="O_element : 029"  # scripted group (container) (typed FeaturePython)
  n = 1
  ref = O_element
FEATURE [App::DocumentObjectGroupPython] G4_LITHIUM_OXIDE  # scripted group (container) (typed FeaturePython)
  Dunit = g/cm3
  Dvalue = 2.013
  Group = -> [Li_element006,O_element055]
  conduct = 2
  density = 1
  expand = 3
  formula = G4_LITHIUM_OXIDE
  name = G4_LITHIUM_OXIDE
  specific = 4
FEATURE [App::DocumentObjectGroupPython] Li_element007  label="Li_element : 007"  # scripted group (container) (typed FeaturePython)
  n = 2
  ref = Li_element
FEATURE [App::DocumentObjectGroupPython] B_element005  label="B_element : 005"  # scripted group (container) (typed FeaturePython)
  n = 4
  ref = B_element
FEATURE [App::DocumentObjectGroupPython] O_element056  label="O_element : 7"  # scripted group (container) (typed FeaturePython)
  n = 7
  ref = O_element
FEATURE [App::DocumentObjectGroupPython] G4_LITHIUM_TETRABORATE  # scripted group (container) (typed FeaturePython)
  Dunit = g/cm3
  Dvalue = 2.44
  Group = -> [Li_element007,B_element005,O_element056]
  conduct = 2
  density = 1
  expand = 3
  formula = G4_LITHIUM_TETRABORATE
  name = G4_LITHIUM_TETRABORATE
  specific = 4
FEATURE [App::DocumentObjectGroupPython] H_element051  label="H_element : 0.105"  # scripted group (container) (typed FeaturePython)
  n = 0.105
FEATURE [App::DocumentObjectGroupPython] C_element056  label="C_element : 0.083"  # scripted group (container) (typed FeaturePython)
  n = 0.083
FEATURE [App::DocumentObjectGroupPython] N_element023  label="N_element : 0.023"  # scripted group (container) (typed FeaturePython)
  n = 0.023
FEATURE [App::DocumentObjectGroupPython] O_element057  label="O_element : 0.779"  # scripted group (container) (typed FeaturePython)
  n = 0.779
FEATURE [App::DocumentObjectGroupPython] Na_element010  label="Na_element : 0.097"  # scripted group (container) (typed FeaturePython)
  n = 0.002
FEATURE [App::DocumentObjectGroupPython] P_element006  label="P_element : 0.105"  # scripted group (container) (typed FeaturePython)
  n = 0.001
FEATURE [App::DocumentObjectGroupPython] S_element016  label="S_element : 0.017"  # scripted group (container) (typed FeaturePython)
  n = 0.002
FEATURE [App::DocumentObjectGroupPython] Cl_element014  label="Cl_element : 0.587"  # scripted group (container) (typed FeaturePython)
  n = 0.003
FEATURE [App::DocumentObjectGroupPython] K_element005  label="K_element : 0.015"  # scripted group (container) (typed FeaturePython)
  n = 0.002
FEATURE [App::DocumentObjectGroupPython] G4_LUNG_ICRP  # scripted group (container) (typed FeaturePython)
  Dunit = g/cm3
  Dvalue = 1.04
  Group = -> [H_element051,C_element056,N_element023,O_element057,Na_element010,P_element006,S_element016,Cl_element014,K_element005]
  conduct = 2
  density = 1
  expand = 3
  formula = G4_LUNG_ICRP
  name = G4_LUNG_ICRP
  specific = 4
FEATURE [App::DocumentObjectGroupPython] H_element052  label="H_element : 0.116"  # scripted group (container) (typed FeaturePython)
  n = 0.114318
FEATURE [App::DocumentObjectGroupPython] C_element057  label="C_element : 0.656"  # scripted group (container) (typed FeaturePython)
  n = 0.655824
FEATURE [App::DocumentObjectGroupPython] O_element058  label="O_element : 0.092"  # scripted group (container) (typed FeaturePython)
  n = 0.0921831
FEATURE [App::DocumentObjectGroupPython] Mg_element004  label="Mg_element : 0.135"  # scripted group (container) (typed FeaturePython)
  n = 0.134792
FEATURE [App::DocumentObjectGroupPython] Ca_element013  label="Ca_element : 0.003"  # scripted group (container) (typed FeaturePython)
  n = 0.002883
FEATURE [App::DocumentObjectGroupPython] G4_M3_WAX  # scripted group (container) (typed FeaturePython)
  Dunit = g/cm3
  Dvalue = 1.05
  Group = -> [H_element052,C_element057,O_element058,Mg_element004,Ca_element013]
  conduct = 2
  density = 1
  expand = 3
  formula = G4_M3_WAX
  name = G4_M3_WAX
  specific = 4
FEATURE [App::DocumentObjectGroupPython] Mg_element005  label="Mg_element : 1"  # scripted group (container) (typed FeaturePython)
  n = 1
  ref = Mg_element
FEATURE [App::DocumentObjectGroupPython] C_element058  label="C_element : 031"  # scripted group (container) (typed FeaturePython)
  n = 1
  ref = C_element
FEATURE [App::DocumentObjectGroupPython] O_element059  label="O_element : 030"  # scripted group (container) (typed FeaturePython)
  n = 3
  ref = O_element
FEATURE [App::DocumentObjectGroupPython] G4_MAGNESIUM_CARBONATE  # scripted group (container) (typed FeaturePython)
  Dunit = g/cm3
  Dvalue = 2.958
  Group = -> [Mg_element005,C_element058,O_element059]
  conduct = 2
  density = 1
  expand = 3
  formula = G4_MAGNESIUM_CARBONATE
  name = G4_MAGNESIUM_CARBONATE
  specific = 4
FEATURE [App::DocumentObjectGroupPython] Mg_element006  label="Mg_element : 002"  # scripted group (container) (typed FeaturePython)
  n = 1
  ref = Mg_element
FEATURE [App::DocumentObjectGroupPython] F_element013  label="F_element : 005"  # scripted group (container) (typed FeaturePython)
  n = 2
  ref = F_element
FEATURE [App::DocumentObjectGroupPython] G4_MAGNESIUM_FLUORIDE  # scripted group (container) (typed FeaturePython)
  Dunit = g/cm3
  Dvalue = 3
  Group = -> [Mg_element006,F_element013]
  conduct = 2
  density = 1
  expand = 3
  formula = G4_MAGNESIUM_FLUORIDE
  name = G4_MAGNESIUM_FLUORIDE
  specific = 4
FEATURE [App::DocumentObjectGroupPython] Mg_element007  label="Mg_element : 003"  # scripted group (container) (typed FeaturePython)
  n = 1
  ref = Mg_element
FEATURE [App::DocumentObjectGroupPython] O_element060  label="O_element : 031"  # scripted group (container) (typed FeaturePython)
  n = 1
  ref = O_element
FEATURE [App::DocumentObjectGroupPython] G4_MAGNESIUM_OXIDE  # scripted group (container) (typed FeaturePython)
  Dunit = g/cm3
  Dvalue = 3.58
  Group = -> [Mg_element007,O_element060]
  conduct = 2
  density = 1
  expand = 3
  formula = G4_MAGNESIUM_OXIDE
  name = G4_MAGNESIUM_OXIDE
  specific = 4
FEATURE [App::DocumentObjectGroupPython] Mg_element008  label="Mg_element : 004"  # scripted group (container) (typed FeaturePython)
  n = 1
  ref = Mg_element
FEATURE [App::DocumentObjectGroupPython] B_element006  label="B_element : 006"  # scripted group (container) (typed FeaturePython)
  n = 4
  ref = B_element
FEATURE [App::DocumentObjectGroupPython] O_element061  label="O_element : 032"  # scripted group (container) (typed FeaturePython)
  n = 7
  ref = O_element
FEATURE [App::DocumentObjectGroupPython] G4_MAGNESIUM_TETRABORATE  # scripted group (container) (typed FeaturePython)
  Dunit = g/cm3
  Dvalue = 2.53
  Group = -> [Mg_element008,B_element006,O_element061]
  conduct = 2
  density = 1
  expand = 3
  formula = G4_MAGNESIUM_TETRABORATE
  name = G4_MAGNESIUM_TETRABORATE
  specific = 4
FEATURE [App::DocumentObjectGroupPython] Hg_element001  label="Hg_element : 1"  # scripted group (container) (typed FeaturePython)
  n = 1
  ref = Hg_element
FEATURE [App::DocumentObjectGroupPython] I_element004  label="I_element : 2"  # scripted group (container) (typed FeaturePython)
  n = 2
  ref = I_element
FEATURE [App::DocumentObjectGroupPython] G4_MERCURIC_IODIDE  # scripted group (container) (typed FeaturePython)
  Dunit = g/cm3
  Dvalue = 6.36
  Group = -> [Hg_element001,I_element004]
  conduct = 2
  density = 1
  expand = 3
  formula = G4_MERCURIC_IODIDE
  name = G4_MERCURIC_IODIDE
  specific = 4
FEATURE [App::DocumentObjectGroupPython] C_element059  label="C_element : 032"  # scripted group (container) (typed FeaturePython)
  n = 1
  ref = C_element
FEATURE [App::DocumentObjectGroupPython] H_element053  label="H_element : 028"  # scripted group (container) (typed FeaturePython)
  n = 4
  ref = H_element
FEATURE [App::DocumentObjectGroupPython] G4_METHANE  # scripted group (container) (typed FeaturePython)
  Dunit = g/cm3
  Dvalue = 0.000667151
  Group = -> [C_element059,H_element053]
  conduct = 2
  density = 1
  expand = 3
  formula = G4_METHANE
  name = G4_METHANE
  specific = 4
FEATURE [App::DocumentObjectGroupPython] C_element060  label="C_element : 033"  # scripted group (container) (typed FeaturePython)
  n = 1
  ref = C_element
FEATURE [App::DocumentObjectGroupPython] H_element054  label="H_element : 029"  # scripted group (container) (typed FeaturePython)
  n = 4
  ref = H_element
FEATURE [App::DocumentObjectGroupPython] O_element062  label="O_element : 033"  # scripted group (container) (typed FeaturePython)
  n = 1
  ref = O_element
FEATURE [App::DocumentObjectGroupPython] G4_METHANOL  # scripted group (container) (typed FeaturePython)
  Dunit = g/cm3
  Dvalue = 0.7914
  Group = -> [C_element060,H_element054,O_element062]
  conduct = 2
  density = 1
  expand = 3
  formula = G4_METHANOL
  name = G4_METHANOL
  specific = 4
FEATURE [App::DocumentObjectGroupPython] H_element055  label="H_element : 0.134"  # scripted group (container) (typed FeaturePython)
  n = 0.13404
FEATURE [App::DocumentObjectGroupPython] C_element061  label="C_element : 0.778"  # scripted group (container) (typed FeaturePython)
  n = 0.77796
FEATURE [App::DocumentObjectGroupPython] O_element063  label="O_element : 0.035"  # scripted group (container) (typed FeaturePython)
  n = 0.03502
FEATURE [App::DocumentObjectGroupPython] Mg_element009  label="Mg_element : 0.039"  # scripted group (container) (typed FeaturePython)
  n = 0.038594
FEATURE [App::DocumentObjectGroupPython] Ti_element002  label="Ti_element : 0.014"  # scripted group (container) (typed FeaturePython)
  n = 0.014386
FEATURE [App::DocumentObjectGroupPython] G4_MIX_D_WAX  # scripted group (container) (typed FeaturePython)
  Dunit = g/cm3
  Dvalue = 0.99
  Group = -> [H_element055,C_element061,O_element063,Mg_element009,Ti_element002]
  conduct = 2
  density = 1
  expand = 3
  formula = G4_MIX_D_WAX
  name = G4_MIX_D_WAX
  specific = 4
FEATURE [App::DocumentObjectGroupPython] H_element056  label="H_element : 0.135"  # scripted group (container) (typed FeaturePython)
  n = 0.081192
FEATURE [App::DocumentObjectGroupPython] C_element062  label="C_element : 0.583"  # scripted group (container) (typed FeaturePython)
  n = 0.583442
FEATURE [App::DocumentObjectGroupPython] N_element024  label="N_element : 0.018"  # scripted group (container) (typed FeaturePython)
  n = 0.017798
FEATURE [App::DocumentObjectGroupPython] O_element064  label="O_element : 0.186"  # scripted group (container) (typed FeaturePython)
  n = 0.186381
FEATURE [App::DocumentObjectGroupPython] Mg_element010  label="Mg_element : 0.130"  # scripted group (container) (typed FeaturePython)
  n = 0.130287
FEATURE [App::DocumentObjectGroupPython] Cl_element015  label="Cl_element : 0.588"  # scripted group (container) (typed FeaturePython)
  n = 0.0009
FEATURE [App::DocumentObjectGroupPython] G4_MS20_TISSUE  # scripted group (container) (typed FeaturePython)
  Dunit = g/cm3
  Dvalue = 1
  Group = -> [H_element056,C_element062,N_element024,O_element064,Mg_element010,Cl_element015]
  conduct = 2
  density = 1
  expand = 3
  formula = G4_MS20_TISSUE
  name = G4_MS20_TISSUE
  specific = 4
FEATURE [App::DocumentObjectGroupPython] H_element057  label="H_element : 0.136"  # scripted group (container) (typed FeaturePython)
  n = 0.102
FEATURE [App::DocumentObjectGroupPython] C_element063  label="C_element : 0.143"  # scripted group (container) (typed FeaturePython)
  n = 0.143
FEATURE [App::DocumentObjectGroupPython] N_element025  label="N_element : 0.034"  # scripted group (container) (typed FeaturePython)
  n = 0.034
FEATURE [App::DocumentObjectGroupPython] O_element065  label="O_element : 0.710"  # scripted group (container) (typed FeaturePython)
  n = 0.71
FEATURE [App::DocumentObjectGroupPython] Na_element011  label="Na_element : 0.098"  # scripted group (container) (typed FeaturePython)
  n = 0.001
FEATURE [App::DocumentObjectGroupPython] P_element007  label="P_element : 0.002"  # scripted group (container) (typed FeaturePython)
  n = 0.002
FEATURE [App::DocumentObjectGroupPython] S_element017  label="S_element : 0.018"  # scripted group (container) (typed FeaturePython)
  n = 0.003
FEATURE [App::DocumentObjectGroupPython] Cl_element016  label="Cl_element : 0.589"  # scripted group (container) (typed FeaturePython)
  n = 0.001
FEATURE [App::DocumentObjectGroupPython] K_element006  label="K_element : 0.004"  # scripted group (container) (typed FeaturePython)
  n = 0.004
FEATURE [App::DocumentObjectGroupPython] G4_MUSCLE_SKELETAL_ICRP  # scripted group (container) (typed FeaturePython)
  Dunit = g/cm3
  Dvalue = 1.05
  Group = -> [H_element057,C_element063,N_element025,O_element065,Na_element011,P_element007,S_element017,Cl_element016,K_element006]
  conduct = 2
  density = 1
  expand = 3
  formula = G4_MUSCLE_SKELETAL_ICRP
  name = G4_MUSCLE_SKELETAL_ICRP
  specific = 4
FEATURE [App::DocumentObjectGroupPython] H_element058  label="H_element : 0.137"  # scripted group (container) (typed FeaturePython)
  n = 0.102102
FEATURE [App::DocumentObjectGroupPython] C_element064  label="C_element : 0.123"  # scripted group (container) (typed FeaturePython)
  n = 0.123123
FEATURE [App::DocumentObjectGroupPython] N_element026  label="N_element : 0.756"  # scripted group (container) (typed FeaturePython)
  n = 0.035035
FEATURE [App::DocumentObjectGroupPython] O_element066  label="O_element : 0.730"  # scripted group (container) (typed FeaturePython)
  n = 0.72973
FEATURE [App::DocumentObjectGroupPython] Na_element012  label="Na_element : 0.099"  # scripted group (container) (typed FeaturePython)
  n = 0.001001
FEATURE [App::DocumentObjectGroupPython] P_element008  label="P_element : 0.106"  # scripted group (container) (typed FeaturePython)
  n = 0.002002
FEATURE [App::DocumentObjectGroupPython] S_element018  label="S_element : 0.019"  # scripted group (container) (typed FeaturePython)
  n = 0.004004
FEATURE [App::DocumentObjectGroupPython] K_element007  label="K_element : 0.016"  # scripted group (container) (typed FeaturePython)
  n = 0.003003
FEATURE [App::DocumentObjectGroupPython] G4_MUSCLE_STRIATED_ICRU  # scripted group (container) (typed FeaturePython)
  Dunit = g/cm3
  Dvalue = 1.04
  Group = -> [H_element058,C_element064,N_element026,O_element066,Na_element012,P_element008,S_element018,K_element007]
  conduct = 2
  density = 1
  expand = 3
  formula = G4_MUSCLE_STRIATED_ICRU
  name = G4_MUSCLE_STRIATED_ICRU
  specific = 4
FEATURE [App::DocumentObjectGroupPython] H_element059  label="H_element : 0.098"  # scripted group (container) (typed FeaturePython)
  n = 0.0982341
FEATURE [App::DocumentObjectGroupPython] C_element065  label="C_element : 0.156"  # scripted group (container) (typed FeaturePython)
  n = 0.156214
FEATURE [App::DocumentObjectGroupPython] N_element027  label="N_element : 0.757"  # scripted group (container) (typed FeaturePython)
  n = 0.035451
FEATURE [App::DocumentObjectGroupPython] O_element067  label="O_element : 0.880"  # scripted group (container) (typed FeaturePython)
  n = 0.710101
FEATURE [App::DocumentObjectGroupPython] G4_MUSCLE_WITH_SUCROSE  # scripted group (container) (typed FeaturePython)
  Dunit = g/cm3
  Dvalue = 1.11
  Group = -> [H_element059,C_element065,N_element027,O_element067]
  conduct = 2
  density = 1
  expand = 3
  formula = G4_MUSCLE_WITH_SUCROSE
  name = G4_MUSCLE_WITH_SUCROSE
  specific = 4
FEATURE [App::DocumentObjectGroupPython] H_element060  label="H_element : 0.138"  # scripted group (container) (typed FeaturePython)
  n = 0.101969
FEATURE [App::DocumentObjectGroupPython] C_element066  label="C_element : 0.120"  # scripted group (container) (typed FeaturePython)
  n = 0.120058
FEATURE [App::DocumentObjectGroupPython] N_element028  label="N_element : 0.758"  # scripted group (container) (typed FeaturePython)
  n = 0.035451
FEATURE [App::DocumentObjectGroupPython] O_element068  label="O_element : 0.743"  # scripted group (container) (typed FeaturePython)
  n = 0.742522
FEATURE [App::DocumentObjectGroupPython] G4_MUSCLE_WITHOUT_SUCROSE  # scripted group (container) (typed FeaturePython)
  Dunit = g/cm3
  Dvalue = 1.07
  Group = -> [H_element060,C_element066,N_element028,O_element068]
  conduct = 2
  density = 1
  expand = 3
  formula = G4_MUSCLE_WITHOUT_SUCROSE
  name = G4_MUSCLE_WITHOUT_SUCROSE
  specific = 4
FEATURE [App::DocumentObjectGroupPython] C_element067  label="C_element : 10"  # scripted group (container) (typed FeaturePython)
  n = 10
  ref = C_element
FEATURE [App::DocumentObjectGroupPython] H_element061  label="H_element : 030"  # scripted group (container) (typed FeaturePython)
  n = 8
  ref = H_element
FEATURE [App::DocumentObjectGroupPython] G4_NAPHTHALENE  # scripted group (container) (typed FeaturePython)
  Dunit = g/cm3
  Dvalue = 1.145
  Group = -> [C_element067,H_element061]
  conduct = 2
  density = 1
  expand = 3
  formula = G4_NAPHTHALENE
  name = G4_NAPHTHALENE
  specific = 4
FEATURE [App::DocumentObjectGroupPython] C_element068  label="C_element : 034"  # scripted group (container) (typed FeaturePython)
  n = 6
  ref = C_element
FEATURE [App::DocumentObjectGroupPython] H_element062  label="H_element : 031"  # scripted group (container) (typed FeaturePython)
  n = 5
  ref = H_element
FEATURE [App::DocumentObjectGroupPython] N_element029  label="N_element : 012"  # scripted group (container) (typed FeaturePython)
  n = 1
  ref = N_element
FEATURE [App::DocumentObjectGroupPython] O_element069  label="O_element : 034"  # scripted group (container) (typed FeaturePython)
  n = 2
  ref = O_element
FEATURE [App::DocumentObjectGroupPython] G4_NITROBENZENE  # scripted group (container) (typed FeaturePython)
  Dunit = g/cm3
  Dvalue = 1.19867
  Group = -> [C_element068,H_element062,N_element029,O_element069]
  conduct = 2
  density = 1
  expand = 3
  formula = G4_NITROBENZENE
  name = G4_NITROBENZENE
  specific = 4
FEATURE [App::DocumentObjectGroupPython] N_element030  label="N_element : 013"  # scripted group (container) (typed FeaturePython)
  n = 2
  ref = N_element
FEATURE [App::DocumentObjectGroupPython] O_element070  label="O_element : 035"  # scripted group (container) (typed FeaturePython)
  n = 1
  ref = O_element
FEATURE [App::DocumentObjectGroupPython] G4_NITROUS_OXIDE  # scripted group (container) (typed FeaturePython)
  Dunit = g/cm3
  Dvalue = 0.00183094
  Group = -> [N_element030,O_element070]
  conduct = 2
  density = 1
  expand = 3
  formula = G4_NITROUS_OXIDE
  name = G4_NITROUS_OXIDE
  specific = 4
FEATURE [App::DocumentObjectGroupPython] H_element063  label="H_element : 0.104"  # scripted group (container) (typed FeaturePython)
  n = 0.103509
FEATURE [App::DocumentObjectGroupPython] C_element069  label="C_element : 0.648"  # scripted group (container) (typed FeaturePython)
  n = 0.648416
FEATURE [App::DocumentObjectGroupPython] N_element031  label="N_element : 0.100"  # scripted group (container) (typed FeaturePython)
  n = 0.0995361
FEATURE [App::DocumentObjectGroupPython] O_element071  label="O_element : 0.149"  # scripted group (container) (typed FeaturePython)
  n = 0.148539
FEATURE [App::DocumentObjectGroupPython] G4_NYLON_8062  label="G4_NYLON-8062"  # scripted group (container) (typed FeaturePython)
  Dunit = g/cm3
  Dvalue = 1.08
  Group = -> [H_element063,C_element069,N_element031,O_element071]
  conduct = 2
  density = 1
  expand = 3
  formula = G4_NYLON-8062
  name = G4_NYLON-8062
  specific = 4
FEATURE [App::DocumentObjectGroupPython] C_element070  label="C_element : 035"  # scripted group (container) (typed FeaturePython)
  n = 6
  ref = C_element
FEATURE [App::DocumentObjectGroupPython] H_element064  label="H_element : 11"  # scripted group (container) (typed FeaturePython)
  n = 11
  ref = H_element
FEATURE [App::DocumentObjectGroupPython] N_element032  label="N_element : 014"  # scripted group (container) (typed FeaturePython)
  n = 1
  ref = N_element
FEATURE [App::DocumentObjectGroupPython] O_element072  label="O_element : 036"  # scripted group (container) (typed FeaturePython)
  n = 1
  ref = O_element
FEATURE [App::DocumentObjectGroupPython] G4_NYLON_6_6  label="G4_NYLON-6-6"  # scripted group (container) (typed FeaturePython)
  Dunit = g/cm3
  Dvalue = 1.14
  Group = -> [C_element070,H_element064,N_element032,O_element072]
  conduct = 2
  density = 1
  expand = 3
  formula = G4_NYLON-6-6
  name = G4_NYLON-6-6
  specific = 4
FEATURE [App::DocumentObjectGroupPython] H_element065  label="H_element : 0.139"  # scripted group (container) (typed FeaturePython)
  n = 0.107062
FEATURE [App::DocumentObjectGroupPython] C_element071  label="C_element : 0.680"  # scripted group (container) (typed FeaturePython)
  n = 0.680449
FEATURE [App::DocumentObjectGroupPython] N_element033  label="N_element : 0.099"  # scripted group (container) (typed FeaturePython)
  n = 0.099189
FEATURE [App::DocumentObjectGroupPython] O_element073  label="O_element : 0.113"  # scripted group (container) (typed FeaturePython)
  n = 0.1133
FEATURE [App::DocumentObjectGroupPython] G4_NYLON_6_10  label="G4_NYLON-6-10"  # scripted group (container) (typed FeaturePython)
  Dunit = g/cm3
  Dvalue = 1.14
  Group = -> [H_element065,C_element071,N_element033,O_element073]
  conduct = 2
  density = 1
  expand = 3
  formula = G4_NYLON-6-10
  name = G4_NYLON-6-10
  specific = 4
FEATURE [App::DocumentObjectGroupPython] H_element066  label="H_element : 0.140"  # scripted group (container) (typed FeaturePython)
  n = 0.115476
FEATURE [App::DocumentObjectGroupPython] C_element072  label="C_element : 0.721"  # scripted group (container) (typed FeaturePython)
  n = 0.720818
FEATURE [App::DocumentObjectGroupPython] N_element034  label="N_element : 0.076"  # scripted group (container) (typed FeaturePython)
  n = 0.0764169
FEATURE [App::DocumentObjectGroupPython] O_element074  label="O_element : 0.087"  # scripted group (container) (typed FeaturePython)
  n = 0.0872889
FEATURE [App::DocumentObjectGroupPython] G4_NYLON_11_RILSAN  label="G4_NYLON-11_RILSAN"  # scripted group (container) (typed FeaturePython)
  Dunit = g/cm3
  Dvalue = 1.425
  Group = -> [H_element066,C_element072,N_element034,O_element074]
  conduct = 2
  density = 1
  expand = 3
  formula = G4_NYLON-11_RILSAN
  name = G4_NYLON-11_RILSAN
  specific = 4
FEATURE [App::DocumentObjectGroupPython] C_element073  label="C_element : 8"  # scripted group (container) (typed FeaturePython)
  n = 8
  ref = C_element
FEATURE [App::DocumentObjectGroupPython] H_element067  label="H_element : 18"  # scripted group (container) (typed FeaturePython)
  n = 18
  ref = H_element
FEATURE [App::DocumentObjectGroupPython] G4_OCTANE  # scripted group (container) (typed FeaturePython)
  Dunit = g/cm3
  Dvalue = 0.7026
  Group = -> [C_element073,H_element067]
  conduct = 2
  density = 1
  expand = 3
  formula = G4_OCTANE
  name = G4_OCTANE
  specific = 4
FEATURE [App::DocumentObjectGroupPython] C_element074  label="C_element : 25"  # scripted group (container) (typed FeaturePython)
  n = 25
  ref = C_element
FEATURE [App::DocumentObjectGroupPython] H_element068  label="H_element : 52"  # scripted group (container) (typed FeaturePython)
  n = 52
  ref = H_element
FEATURE [App::DocumentObjectGroupPython] G4_PARAFFIN  # scripted group (container) (typed FeaturePython)
  Dunit = g/cm3
  Dvalue = 0.93
  Group = -> [C_element074,H_element068]
  conduct = 2
  density = 1
  expand = 3
  formula = G4_PARAFFIN
  name = G4_PARAFFIN
  specific = 4
FEATURE [App::DocumentObjectGroupPython] C_element075  label="C_element : 036"  # scripted group (container) (typed FeaturePython)
  n = 5
  ref = C_element
FEATURE [App::DocumentObjectGroupPython] H_element069  label="H_element : 032"  # scripted group (container) (typed FeaturePython)
  n = 12
  ref = H_element
FEATURE [App::DocumentObjectGroupPython] G4_N_PENTANE  label="G4_N-PENTANE"  # scripted group (container) (typed FeaturePython)
  Dunit = g/cm3
  Dvalue = 0.6262
  Group = -> [C_element075,H_element069]
  conduct = 2
  density = 1
  expand = 3
  formula = G4_N-PENTANE
  name = G4_N-PENTANE
  specific = 4
FEATURE [App::DocumentObjectGroupPython] H_element070  label="H_element : 0.014"  # scripted group (container) (typed FeaturePython)
  n = 0.0141
FEATURE [App::DocumentObjectGroupPython] C_element076  label="C_element : 0.072"  # scripted group (container) (typed FeaturePython)
  n = 0.072261
FEATURE [App::DocumentObjectGroupPython] N_element035  label="N_element : 0.019"  # scripted group (container) (typed FeaturePython)
  n = 0.01932
FEATURE [App::DocumentObjectGroupPython] O_element075  label="O_element : 0.066"  # scripted group (container) (typed FeaturePython)
  n = 0.066101
FEATURE [App::DocumentObjectGroupPython] S_element019  label="S_element : 0.020"  # scripted group (container) (typed FeaturePython)
  n = 0.00189
FEATURE [App::DocumentObjectGroupPython] Br_element004  label="Br_element : 0.349"  # scripted group (container) (typed FeaturePython)
  n = 0.349103
FEATURE [App::DocumentObjectGroupPython] Ag_element001  label="Ag_element : 0.474"  # scripted group (container) (typed FeaturePython)
  n = 0.474105
FEATURE [App::DocumentObjectGroupPython] I_element005  label="I_element : 0.003"  # scripted group (container) (typed FeaturePython)
  n = 0.00312
FEATURE [App::DocumentObjectGroupPython] G4_PHOTO_EMULSION  # scripted group (container) (typed FeaturePython)
  Dunit = g/cm3
  Dvalue = 3.815
  Group = -> [H_element070,C_element076,N_element035,O_element075,S_element019,Br_element004,Ag_element001,I_element005]
  conduct = 2
  density = 1
  expand = 3
  formula = G4_PHOTO_EMULSION
  name = G4_PHOTO_EMULSION
  specific = 4
FEATURE [App::DocumentObjectGroupPython] C_element077  label="C_element : 9"  # scripted group (container) (typed FeaturePython)
  n = 9
  ref = C_element
FEATURE [App::DocumentObjectGroupPython] H_element071  label="H_element : 033"  # scripted group (container) (typed FeaturePython)
  n = 10
  ref = H_element
FEATURE [App::DocumentObjectGroupPython] G4_PLASTIC_SC_VINYLTOLUENE  # scripted group (container) (typed FeaturePython)
  Dunit = g/cm3
  Dvalue = 1.032
  Group = -> [C_element077,H_element071]
  conduct = 2
  density = 1
  expand = 3
  formula = G4_PLASTIC_SC_VINYLTOLUENE
  name = G4_PLASTIC_SC_VINYLTOLUENE
  specific = 4
FEATURE [App::DocumentObjectGroupPython] Pu_element001  label="Pu_element : 1"  # scripted group (container) (typed FeaturePython)
  n = 1
  ref = Pu_element
FEATURE [App::DocumentObjectGroupPython] O_element076  label="O_element : 037"  # scripted group (container) (typed FeaturePython)
  n = 2
  ref = O_element
FEATURE [App::DocumentObjectGroupPython] G4_PLUTONIUM_DIOXIDE  # scripted group (container) (typed FeaturePython)
  Dunit = g/cm3
  Dvalue = 11.46
  Group = -> [Pu_element001,O_element076]
  conduct = 2
  density = 1
  expand = 3
  formula = G4_PLUTONIUM_DIOXIDE
  name = G4_PLUTONIUM_DIOXIDE
  specific = 4
FEATURE [App::DocumentObjectGroupPython] C_element078  label="C_element : 037"  # scripted group (container) (typed FeaturePython)
  n = 3
  ref = C_element
FEATURE [App::DocumentObjectGroupPython] H_element072  label="H_element : 034"  # scripted group (container) (typed FeaturePython)
  n = 3
  ref = H_element
FEATURE [App::DocumentObjectGroupPython] N_element036  label="N_element : 015"  # scripted group (container) (typed FeaturePython)
  n = 1
  ref = N_element
FEATURE [App::DocumentObjectGroupPython] G4_POLYACRYLONITRILE  # scripted group (container) (typed FeaturePython)
  Dunit = g/cm3
  Dvalue = 1.17
  Group = -> [C_element078,H_element072,N_element036]
  conduct = 2
  density = 1
  expand = 3
  formula = G4_POLYACRYLONITRILE
  name = G4_POLYACRYLONITRILE
  specific = 4
FEATURE [App::DocumentObjectGroupPython] C_element079  label="C_element : 16"  # scripted group (container) (typed FeaturePython)
  n = 16
  ref = C_element
FEATURE [App::DocumentObjectGroupPython] H_element073  label="H_element : 035"  # scripted group (container) (typed FeaturePython)
  n = 14
  ref = H_element
FEATURE [App::DocumentObjectGroupPython] O_element077  label="O_element : 038"  # scripted group (container) (typed FeaturePython)
  n = 3
  ref = O_element
FEATURE [App::DocumentObjectGroupPython] G4_POLYCARBONATE  # scripted group (container) (typed FeaturePython)
  Dunit = g/cm3
  Dvalue = 1.2
  Group = -> [C_element079,H_element073,O_element077]
  conduct = 2
  density = 1
  expand = 3
  formula = G4_POLYCARBONATE
  name = G4_POLYCARBONATE
  specific = 4
FEATURE [App::DocumentObjectGroupPython] C_element080  label="C_element : 038"  # scripted group (container) (typed FeaturePython)
  n = 8
  ref = C_element
FEATURE [App::DocumentObjectGroupPython] H_element074  label="H_element : 036"  # scripted group (container) (typed FeaturePython)
  n = 7
  ref = H_element
FEATURE [App::DocumentObjectGroupPython] Cl_element017  label="Cl_element : 007"  # scripted group (container) (typed FeaturePython)
  n = 1
  ref = Cl_element
FEATURE [App::DocumentObjectGroupPython] G4_POLYCHLOROSTYRENE  # scripted group (container) (typed FeaturePython)
  Dunit = g/cm3
  Dvalue = 1.3
  Group = -> [C_element080,H_element074,Cl_element017]
  conduct = 2
  density = 1
  expand = 3
  formula = G4_POLYCHLOROSTYRENE
  name = G4_POLYCHLOROSTYRENE
  specific = 4
FEATURE [App::DocumentObjectGroupPython] C_element081  label="C_element : 039"  # scripted group (container) (typed FeaturePython)
  n = 1
  ref = C_element
FEATURE [App::DocumentObjectGroupPython] H_element075  label="H_element : 037"  # scripted group (container) (typed FeaturePython)
  n = 2
  ref = H_element
FEATURE [App::DocumentObjectGroupPython] G4_POLYETHYLENE  # scripted group (container) (typed FeaturePython)
  Dunit = g/cm3
  Dvalue = 0.94
  Group = -> [C_element081,H_element075]
  conduct = 2
  density = 1
  expand = 3
  formula = G4_POLYETHYLENE
  name = G4_POLYETHYLENE
  specific = 4
FEATURE [App::DocumentObjectGroupPython] C_element082  label="C_element : 040"  # scripted group (container) (typed FeaturePython)
  n = 10
  ref = C_element
FEATURE [App::DocumentObjectGroupPython] H_element076  label="H_element : 038"  # scripted group (container) (typed FeaturePython)
  n = 8
  ref = H_element
FEATURE [App::DocumentObjectGroupPython] O_element078  label="O_element : 039"  # scripted group (container) (typed FeaturePython)
  n = 4
  ref = O_element
FEATURE [App::DocumentObjectGroupPython] G4_MYLAR  # scripted group (container) (typed FeaturePython)
  Dunit = g/cm3
  Dvalue = 1.4
  Group = -> [C_element082,H_element076,O_element078]
  conduct = 2
  density = 1
  expand = 3
  formula = G4_MYLAR
  name = G4_MYLAR
  specific = 4
FEATURE [App::DocumentObjectGroupPython] C_element083  label="C_element : 041"  # scripted group (container) (typed FeaturePython)
  n = 5
  ref = C_element
FEATURE [App::DocumentObjectGroupPython] H_element077  label="H_element : 039"  # scripted group (container) (typed FeaturePython)
  n = 8
  ref = H_element
FEATURE [App::DocumentObjectGroupPython] O_element079  label="O_element : 040"  # scripted group (container) (typed FeaturePython)
  n = 2
  ref = O_element
FEATURE [App::DocumentObjectGroupPython] G4_PLEXIGLASS  # scripted group (container) (typed FeaturePython)
  Dunit = g/cm3
  Dvalue = 1.19
  Group = -> [C_element083,H_element077,O_element079]
  conduct = 2
  density = 1
  expand = 3
  formula = G4_PLEXIGLASS
  name = G4_PLEXIGLASS
  specific = 4
FEATURE [App::DocumentObjectGroupPython] C_element084  label="C_element : 042"  # scripted group (container) (typed FeaturePython)
  n = 1
  ref = C_element
FEATURE [App::DocumentObjectGroupPython] H_element078  label="H_element : 040"  # scripted group (container) (typed FeaturePython)
  n = 2
  ref = H_element
FEATURE [App::DocumentObjectGroupPython] O_element080  label="O_element : 041"  # scripted group (container) (typed FeaturePython)
  n = 1
  ref = O_element
FEATURE [App::DocumentObjectGroupPython] G4_POLYOXYMETHYLENE  # scripted group (container) (typed FeaturePython)
  Dunit = g/cm3
  Dvalue = 1.425
  Group = -> [C_element084,H_element078,O_element080]
  conduct = 2
  density = 1
  expand = 3
  formula = G4_POLYOXYMETHYLENE
  name = G4_POLYOXYMETHYLENE
  specific = 4
FEATURE [App::DocumentObjectGroupPython] C_element085  label="C_element : 043"  # scripted group (container) (typed FeaturePython)
  n = 2
  ref = C_element
FEATURE [App::DocumentObjectGroupPython] H_element079  label="H_element : 041"  # scripted group (container) (typed FeaturePython)
  n = 4
  ref = H_element
FEATURE [App::DocumentObjectGroupPython] G4_POLYPROPYLENE  # scripted group (container) (typed FeaturePython)
  Dunit = g/cm3
  Dvalue = 0.9
  Group = -> [C_element085,H_element079]
  conduct = 2
  density = 1
  expand = 3
  formula = G4_POLYPROPYLENE
  name = G4_POLYPROPYLENE
  specific = 4
FEATURE [App::DocumentObjectGroupPython] C_element086  label="C_element : 044"  # scripted group (container) (typed FeaturePython)
  n = 8
  ref = C_element
FEATURE [App::DocumentObjectGroupPython] H_element080  label="H_element : 042"  # scripted group (container) (typed FeaturePython)
  n = 8
  ref = H_element
FEATURE [App::DocumentObjectGroupPython] G4_POLYSTYRENE  # scripted group (container) (typed FeaturePython)
  Dunit = g/cm3
  Dvalue = 1.06
  Group = -> [C_element086,H_element080]
  conduct = 2
  density = 1
  expand = 3
  formula = G4_POLYSTYRENE
  name = G4_POLYSTYRENE
  specific = 4
FEATURE [App::DocumentObjectGroupPython] C_element087  label="C_element : 045"  # scripted group (container) (typed FeaturePython)
  n = 2
  ref = C_element
FEATURE [App::DocumentObjectGroupPython] F_element014  label="F_element : 4"  # scripted group (container) (typed FeaturePython)
  n = 4
  ref = F_element
FEATURE [App::DocumentObjectGroupPython] G4_TEFLON  # scripted group (container) (typed FeaturePython)
  Dunit = g/cm3
  Dvalue = 2.2
  Group = -> [C_element087,F_element014]
  conduct = 2
  density = 1
  expand = 3
  formula = G4_TEFLON
  name = G4_TEFLON
  specific = 4
FEATURE [App::DocumentObjectGroupPython] C_element088  label="C_element : 046"  # scripted group (container) (typed FeaturePython)
  n = 2
  ref = C_element
FEATURE [App::DocumentObjectGroupPython] F_element015  label="F_element : 006"  # scripted group (container) (typed FeaturePython)
  n = 3
  ref = F_element
FEATURE [App::DocumentObjectGroupPython] Cl_element018  label="Cl_element : 008"  # scripted group (container) (typed FeaturePython)
  n = 1
  ref = Cl_element
FEATURE [App::DocumentObjectGroupPython] G4_POLYTRIFLUOROCHLOROETHYLENE  # scripted group (container) (typed FeaturePython)
  Dunit = g/cm3
  Dvalue = 2.1
  Group = -> [C_element088,F_element015,Cl_element018]
  conduct = 2
  density = 1
  expand = 3
  formula = G4_POLYTRIFLUOROCHLOROETHYLENE
  name = G4_POLYTRIFLUOROCHLOROETHYLENE
  specific = 4
FEATURE [App::DocumentObjectGroupPython] C_element089  label="C_element : 047"  # scripted group (container) (typed FeaturePython)
  n = 4
  ref = C_element
FEATURE [App::DocumentObjectGroupPython] H_element081  label="H_element : 043"  # scripted group (container) (typed FeaturePython)
  n = 6
  ref = H_element
FEATURE [App::DocumentObjectGroupPython] O_element081  label="O_element : 042"  # scripted group (container) (typed FeaturePython)
  n = 2
  ref = O_element
FEATURE [App::DocumentObjectGroupPython] G4_POLYVINYL_ACETATE  # scripted group (container) (typed FeaturePython)
  Dunit = g/cm3
  Dvalue = 1.19
  Group = -> [C_element089,H_element081,O_element081]
  conduct = 2
  density = 1
  expand = 3
  formula = G4_POLYVINYL_ACETATE
  name = G4_POLYVINYL_ACETATE
  specific = 4
FEATURE [App::DocumentObjectGroupPython] C_element090  label="C_element : 048"  # scripted group (container) (typed FeaturePython)
  n = 2
  ref = C_element
FEATURE [App::DocumentObjectGroupPython] H_element082  label="H_element : 044"  # scripted group (container) (typed FeaturePython)
  n = 4
  ref = H_element
FEATURE [App::DocumentObjectGroupPython] O_element082  label="O_element : 043"  # scripted group (container) (typed FeaturePython)
  n = 1
  ref = O_element
FEATURE [App::DocumentObjectGroupPython] G4_POLYVINYL_ALCOHOL  # scripted group (container) (typed FeaturePython)
  Dunit = g/cm3
  Dvalue = 1.3
  Group = -> [C_element090,H_element082,O_element082]
  conduct = 2
  density = 1
  expand = 3
  formula = G4_POLYVINYL_ALCOHOL
  name = G4_POLYVINYL_ALCOHOL
  specific = 4
FEATURE [App::DocumentObjectGroupPython] C_element091  label="C_element : 049"  # scripted group (container) (typed FeaturePython)
  n = 8
  ref = C_element
FEATURE [App::DocumentObjectGroupPython] H_element083  label="H_element : 045"  # scripted group (container) (typed FeaturePython)
  n = 14
  ref = H_element
FEATURE [App::DocumentObjectGroupPython] O_element083  label="O_element : 044"  # scripted group (container) (typed FeaturePython)
  n = 2
  ref = O_element
FEATURE [App::DocumentObjectGroupPython] G4_POLYVINYL_BUTYRAL  # scripted group (container) (typed FeaturePython)
  Dunit = g/cm3
  Dvalue = 1.12
  Group = -> [C_element091,H_element083,O_element083]
  conduct = 2
  density = 1
  expand = 3
  formula = G4_POLYVINYL_BUTYRAL
  name = G4_POLYVINYL_BUTYRAL
  specific = 4
FEATURE [App::DocumentObjectGroupPython] C_element092  label="C_element : 050"  # scripted group (container) (typed FeaturePython)
  n = 2
  ref = C_element
FEATURE [App::DocumentObjectGroupPython] H_element084  label="H_element : 046"  # scripted group (container) (typed FeaturePython)
  n = 3
  ref = H_element
FEATURE [App::DocumentObjectGroupPython] Cl_element019  label="Cl_element : 009"  # scripted group (container) (typed FeaturePython)
  n = 1
  ref = Cl_element
FEATURE [App::DocumentObjectGroupPython] G4_POLYVINYL_CHLORIDE  # scripted group (container) (typed FeaturePython)
  Dunit = g/cm3
  Dvalue = 1.3
  Group = -> [C_element092,H_element084,Cl_element019]
  conduct = 2
  density = 1
  expand = 3
  formula = G4_POLYVINYL_CHLORIDE
  name = G4_POLYVINYL_CHLORIDE
  specific = 4
FEATURE [App::DocumentObjectGroupPython] C_element093  label="C_element : 051"  # scripted group (container) (typed FeaturePython)
  n = 2
  ref = C_element
FEATURE [App::DocumentObjectGroupPython] H_element085  label="H_element : 047"  # scripted group (container) (typed FeaturePython)
  n = 2
  ref = H_element
FEATURE [App::DocumentObjectGroupPython] Cl_element020  label="Cl_element : 010"  # scripted group (container) (typed FeaturePython)
  n = 2
  ref = Cl_element
FEATURE [App::DocumentObjectGroupPython] G4_POLYVINYLIDENE_CHLORIDE  # scripted group (container) (typed FeaturePython)
  Dunit = g/cm3
  Dvalue = 1.7
  Group = -> [C_element093,H_element085,Cl_element020]
  conduct = 2
  density = 1
  expand = 3
  formula = G4_POLYVINYLIDENE_CHLORIDE
  name = G4_POLYVINYLIDENE_CHLORIDE
  specific = 4
FEATURE [App::DocumentObjectGroupPython] C_element094  label="C_element : 052"  # scripted group (container) (typed FeaturePython)
  n = 2
  ref = C_element
FEATURE [App::DocumentObjectGroupPython] H_element086  label="H_element : 048"  # scripted group (container) (typed FeaturePython)
  n = 2
  ref = H_element
FEATURE [App::DocumentObjectGroupPython] F_element016  label="F_element : 007"  # scripted group (container) (typed FeaturePython)
  n = 2
  ref = F_element
FEATURE [App::DocumentObjectGroupPython] G4_POLYVINYLIDENE_FLUORIDE  # scripted group (container) (typed FeaturePython)
  Dunit = g/cm3
  Dvalue = 1.76
  Group = -> [C_element094,H_element086,F_element016]
  conduct = 2
  density = 1
  expand = 3
  formula = G4_POLYVINYLIDENE_FLUORIDE
  name = G4_POLYVINYLIDENE_FLUORIDE
  specific = 4
FEATURE [App::DocumentObjectGroupPython] C_element095  label="C_element : 053"  # scripted group (container) (typed FeaturePython)
  n = 6
  ref = C_element
FEATURE [App::DocumentObjectGroupPython] H_element087  label="H_element : 9"  # scripted group (container) (typed FeaturePython)
  n = 9
  ref = H_element
FEATURE [App::DocumentObjectGroupPython] N_element037  label="N_element : 016"  # scripted group (container) (typed FeaturePython)
  n = 1
  ref = N_element
FEATURE [App::DocumentObjectGroupPython] O_element084  label="O_element : 045"  # scripted group (container) (typed FeaturePython)
  n = 1
  ref = O_element
FEATURE [App::DocumentObjectGroupPython] G4_POLYVINYL_PYRROLIDONE  # scripted group (container) (typed FeaturePython)
  Dunit = g/cm3
  Dvalue = 1.25
  Group = -> [C_element095,H_element087,N_element037,O_element084]
  conduct = 2
  density = 1
  expand = 3
  formula = G4_POLYVINYL_PYRROLIDONE
  name = G4_POLYVINYL_PYRROLIDONE
  specific = 4
FEATURE [App::DocumentObjectGroupPython] K_element008  label="K_element : 1"  # scripted group (container) (typed FeaturePython)
  n = 1
  ref = K_element
FEATURE [App::DocumentObjectGroupPython] I_element006  label="I_element : 003"  # scripted group (container) (typed FeaturePython)
  n = 1
  ref = I_element
FEATURE [App::DocumentObjectGroupPython] G4_POTASSIUM_IODIDE  # scripted group (container) (typed FeaturePython)
  Dunit = g/cm3
  Dvalue = 3.13
  Group = -> [K_element008,I_element006]
  conduct = 2
  density = 1
  expand = 3
  formula = G4_POTASSIUM_IODIDE
  name = G4_POTASSIUM_IODIDE
  specific = 4
FEATURE [App::DocumentObjectGroupPython] K_element009  label="K_element : 2"  # scripted group (container) (typed FeaturePython)
  n = 2
  ref = K_element
FEATURE [App::DocumentObjectGroupPython] O_element085  label="O_element : 046"  # scripted group (container) (typed FeaturePython)
  n = 1
  ref = O_element
FEATURE [App::DocumentObjectGroupPython] G4_POTASSIUM_OXIDE  # scripted group (container) (typed FeaturePython)
  Dunit = g/cm3
  Dvalue = 2.32
  Group = -> [K_element009,O_element085]
  conduct = 2
  density = 1
  expand = 3
  formula = G4_POTASSIUM_OXIDE
  name = G4_POTASSIUM_OXIDE
  specific = 4
FEATURE [App::DocumentObjectGroupPython] C_element096  label="C_element : 054"  # scripted group (container) (typed FeaturePython)
  n = 3
  ref = C_element
FEATURE [App::DocumentObjectGroupPython] H_element088  label="H_element : 049"  # scripted group (container) (typed FeaturePython)
  n = 8
  ref = H_element
FEATURE [App::DocumentObjectGroupPython] G4_PROPANE  # scripted group (container) (typed FeaturePython)
  Dunit = g/cm3
  Dvalue = 0.00187939
  Group = -> [C_element096,H_element088]
  conduct = 2
  density = 1
  expand = 3
  formula = G4_PROPANE
  name = G4_PROPANE
  specific = 4
FEATURE [App::DocumentObjectGroupPython] C_element097  label="C_element : 055"  # scripted group (container) (typed FeaturePython)
  n = 3
  ref = C_element
FEATURE [App::DocumentObjectGroupPython] H_element089  label="H_element : 050"  # scripted group (container) (typed FeaturePython)
  n = 8
  ref = H_element
FEATURE [App::DocumentObjectGroupPython] G4_lPROPANE  # scripted group (container) (typed FeaturePython)
  Dunit = g/cm3
  Dvalue = 0.43
  Group = -> [C_element097,H_element089]
  conduct = 2
  density = 1
  expand = 3
  formula = G4_lPROPANE
  name = G4_lPROPANE
  specific = 4
FEATURE [App::DocumentObjectGroupPython] C_element098  label="C_element : 056"  # scripted group (container) (typed FeaturePython)
  n = 3
  ref = C_element
FEATURE [App::DocumentObjectGroupPython] H_element090  label="H_element : 051"  # scripted group (container) (typed FeaturePython)
  n = 8
  ref = H_element
FEATURE [App::DocumentObjectGroupPython] O_element086  label="O_element : 047"  # scripted group (container) (typed FeaturePython)
  n = 1
  ref = O_element
FEATURE [App::DocumentObjectGroupPython] G4_N_PROPYL_ALCOHOL  label="G4_N-PROPYL_ALCOHOL"  # scripted group (container) (typed FeaturePython)
  Dunit = g/cm3
  Dvalue = 0.8035
  Group = -> [C_element098,H_element090,O_element086]
  conduct = 2
  density = 1
  expand = 3
  formula = G4_N-PROPYL_ALCOHOL
  name = G4_N-PROPYL_ALCOHOL
  specific = 4
FEATURE [App::DocumentObjectGroupPython] C_element099  label="C_element : 057"  # scripted group (container) (typed FeaturePython)
  n = 5
  ref = C_element
FEATURE [App::DocumentObjectGroupPython] H_element091  label="H_element : 052"  # scripted group (container) (typed FeaturePython)
  n = 5
  ref = H_element
FEATURE [App::DocumentObjectGroupPython] N_element038  label="N_element : 017"  # scripted group (container) (typed FeaturePython)
  n = 1
  ref = N_element
FEATURE [App::DocumentObjectGroupPython] G4_PYRIDINE  # scripted group (container) (typed FeaturePython)
  Dunit = g/cm3
  Dvalue = 0.9819
  Group = -> [C_element099,H_element091,N_element038]
  conduct = 2
  density = 1
  expand = 3
  formula = G4_PYRIDINE
  name = G4_PYRIDINE
  specific = 4
FEATURE [App::DocumentObjectGroupPython] H_element092  label="H_element : 0.144"  # scripted group (container) (typed FeaturePython)
  n = 0.143711
FEATURE [App::DocumentObjectGroupPython] C_element100  label="C_element : 0.856"  # scripted group (container) (typed FeaturePython)
  n = 0.856289
FEATURE [App::DocumentObjectGroupPython] G4_RUBBER_BUTYL  # scripted group (container) (typed FeaturePython)
  Dunit = g/cm3
  Dvalue = 0.92
  Group = -> [H_element092,C_element100]
  conduct = 2
  density = 1
  expand = 3
  formula = G4_RUBBER_BUTYL
  name = G4_RUBBER_BUTYL
  specific = 4
FEATURE [App::DocumentObjectGroupPython] H_element093  label="H_element : 0.118"  # scripted group (container) (typed FeaturePython)
  n = 0.118371
FEATURE [App::DocumentObjectGroupPython] C_element101  label="C_element : 0.882"  # scripted group (container) (typed FeaturePython)
  n = 0.881629
FEATURE [App::DocumentObjectGroupPython] G4_RUBBER_NATURAL  # scripted group (container) (typed FeaturePython)
  Dunit = g/cm3
  Dvalue = 0.92
  Group = -> [H_element093,C_element101]
  conduct = 2
  density = 1
  expand = 3
  formula = G4_RUBBER_NATURAL
  name = G4_RUBBER_NATURAL
  specific = 4
FEATURE [App::DocumentObjectGroupPython] H_element094  label="H_element : 0.145"  # scripted group (container) (typed FeaturePython)
  n = 0.05692
FEATURE [App::DocumentObjectGroupPython] C_element102  label="C_element : 0.543"  # scripted group (container) (typed FeaturePython)
  n = 0.542646
FEATURE [App::DocumentObjectGroupPython] Cl_element021  label="Cl_element : 0.400"  # scripted group (container) (typed FeaturePython)
  n = 0.400434
FEATURE [App::DocumentObjectGroupPython] G4_RUBBER_NEOPRENE  # scripted group (container) (typed FeaturePython)
  Dunit = g/cm3
  Dvalue = 1.23
  Group = -> [H_element094,C_element102,Cl_element021]
  conduct = 2
  density = 1
  expand = 3
  formula = G4_RUBBER_NEOPRENE
  name = G4_RUBBER_NEOPRENE
  specific = 4
FEATURE [App::DocumentObjectGroupPython] Si_element006  label="Si_element : 1"  # scripted group (container) (typed FeaturePython)
  n = 1
  ref = Si_element
FEATURE [App::DocumentObjectGroupPython] O_element087  label="O_element : 048"  # scripted group (container) (typed FeaturePython)
  n = 2
  ref = O_element
FEATURE [App::DocumentObjectGroupPython] G4_SILICON_DIOXIDE  # scripted group (container) (typed FeaturePython)
  Dunit = g/cm3
  Dvalue = 2.32
  Group = -> [Si_element006,O_element087]
  conduct = 2
  density = 1
  expand = 3
  formula = G4_SILICON_DIOXIDE
  name = G4_SILICON_DIOXIDE
  specific = 4
FEATURE [App::DocumentObjectGroupPython] Ag_element002  label="Ag_element : 1"  # scripted group (container) (typed FeaturePython)
  n = 1
  ref = Ag_element
FEATURE [App::DocumentObjectGroupPython] Br_element005  label="Br_element : 003"  # scripted group (container) (typed FeaturePython)
  n = 1
  ref = Br_element
FEATURE [App::DocumentObjectGroupPython] G4_SILVER_BROMIDE  # scripted group (container) (typed FeaturePython)
  Dunit = g/cm3
  Dvalue = 6.473
  Group = -> [Ag_element002,Br_element005]
  conduct = 2
  density = 1
  expand = 3
  formula = G4_SILVER_BROMIDE
  name = G4_SILVER_BROMIDE
  specific = 4
FEATURE [App::DocumentObjectGroupPython] Ag_element003  label="Ag_element : 002"  # scripted group (container) (typed FeaturePython)
  n = 1
  ref = Ag_element
FEATURE [App::DocumentObjectGroupPython] Cl_element022  label="Cl_element : 011"  # scripted group (container) (typed FeaturePython)
  n = 1
  ref = Cl_element
FEATURE [App::DocumentObjectGroupPython] G4_SILVER_CHLORIDE  # scripted group (container) (typed FeaturePython)
  Dunit = g/cm3
  Dvalue = 5.56
  Group = -> [Ag_element003,Cl_element022]
  conduct = 2
  density = 1
  expand = 3
  formula = G4_SILVER_CHLORIDE
  name = G4_SILVER_CHLORIDE
  specific = 4
FEATURE [App::DocumentObjectGroupPython] Br_element006  label="Br_element : 0.423"  # scripted group (container) (typed FeaturePython)
  n = 0.422895
FEATURE [App::DocumentObjectGroupPython] Ag_element004  label="Ag_element : 0.574"  # scripted group (container) (typed FeaturePython)
  n = 0.573748
FEATURE [App::DocumentObjectGroupPython] I_element007  label="I_element : 0.649"  # scripted group (container) (typed FeaturePython)
  n = 0.003357
FEATURE [App::DocumentObjectGroupPython] G4_SILVER_HALIDES  # scripted group (container) (typed FeaturePython)
  Dunit = g/cm3
  Dvalue = 6.47
  Group = -> [Br_element006,Ag_element004,I_element007]
  conduct = 2
  density = 1
  expand = 3
  formula = G4_SILVER_HALIDES
  name = G4_SILVER_HALIDES
  specific = 4
FEATURE [App::DocumentObjectGroupPython] Ag_element005  label="Ag_element : 003"  # scripted group (container) (typed FeaturePython)
  n = 1
  ref = Ag_element
FEATURE [App::DocumentObjectGroupPython] I_element008  label="I_element : 004"  # scripted group (container) (typed FeaturePython)
  n = 1
  ref = I_element
FEATURE [App::DocumentObjectGroupPython] G4_SILVER_IODIDE  # scripted group (container) (typed FeaturePython)
  Dunit = g/cm3
  Dvalue = 6.01
  Group = -> [Ag_element005,I_element008]
  conduct = 2
  density = 1
  expand = 3
  formula = G4_SILVER_IODIDE
  name = G4_SILVER_IODIDE
  specific = 4
FEATURE [App::DocumentObjectGroupPython] H_element095  label="H_element : 0.100"  # scripted group (container) (typed FeaturePython)
  n = 0.1
FEATURE [App::DocumentObjectGroupPython] C_element103  label="C_element : 0.204"  # scripted group (container) (typed FeaturePython)
  n = 0.204
FEATURE [App::DocumentObjectGroupPython] N_element039  label="N_element : 0.759"  # scripted group (container) (typed FeaturePython)
  n = 0.042
FEATURE [App::DocumentObjectGroupPython] O_element088  label="O_element : 0.645"  # scripted group (container) (typed FeaturePython)
  n = 0.645
FEATURE [App::DocumentObjectGroupPython] Na_element013  label="Na_element : 0.100"  # scripted group (container) (typed FeaturePython)
  n = 0.002
FEATURE [App::DocumentObjectGroupPython] P_element009  label="P_element : 0.107"  # scripted group (container) (typed FeaturePython)
  n = 0.001
FEATURE [App::DocumentObjectGroupPython] S_element020  label="S_element : 0.021"  # scripted group (container) (typed FeaturePython)
  n = 0.002
FEATURE [App::DocumentObjectGroupPython] Cl_element023  label="Cl_element : 0.590"  # scripted group (container) (typed FeaturePython)
  n = 0.003
FEATURE [App::DocumentObjectGroupPython] K_element010  label="K_element : 0.001"  # scripted group (container) (typed FeaturePython)
  n = 0.001
FEATURE [App::DocumentObjectGroupPython] G4_SKIN_ICRP  # scripted group (container) (typed FeaturePython)
  Dunit = g/cm3
  Dvalue = 1.09
  Group = -> [H_element095,C_element103,N_element039,O_element088,Na_element013,P_element009,S_element020,Cl_element023,K_element010]
  conduct = 2
  density = 1
  expand = 3
  formula = G4_SKIN_ICRP
  name = G4_SKIN_ICRP
  specific = 4
FEATURE [App::DocumentObjectGroupPython] Na_element014  label="Na_element : 2"  # scripted group (container) (typed FeaturePython)
  n = 2
  ref = Na_element
FEATURE [App::DocumentObjectGroupPython] C_element104  label="C_element : 058"  # scripted group (container) (typed FeaturePython)
  n = 1
  ref = C_element
FEATURE [App::DocumentObjectGroupPython] O_element089  label="O_element : 049"  # scripted group (container) (typed FeaturePython)
  n = 3
  ref = O_element
FEATURE [App::DocumentObjectGroupPython] G4_SODIUM_CARBONATE  # scripted group (container) (typed FeaturePython)
  Dunit = g/cm3
  Dvalue = 2.532
  Group = -> [Na_element014,C_element104,O_element089]
  conduct = 2
  density = 1
  expand = 3
  formula = G4_SODIUM_CARBONATE
  name = G4_SODIUM_CARBONATE
  specific = 4
FEATURE [App::DocumentObjectGroupPython] Na_element015  label="Na_element : 1"  # scripted group (container) (typed FeaturePython)
  n = 1
  ref = Na_element
FEATURE [App::DocumentObjectGroupPython] I_element009  label="I_element : 005"  # scripted group (container) (typed FeaturePython)
  n = 1
  ref = I_element
FEATURE [App::DocumentObjectGroupPython] G4_SODIUM_IODIDE  # scripted group (container) (typed FeaturePython)
  Dunit = g/cm3
  Dvalue = 3.667
  Group = -> [Na_element015,I_element009]
  conduct = 2
  density = 1
  expand = 3
  formula = G4_SODIUM_IODIDE
  name = G4_SODIUM_IODIDE
  specific = 4
FEATURE [App::DocumentObjectGroupPython] Na_element016  label="Na_element : 003"  # scripted group (container) (typed FeaturePython)
  n = 2
  ref = Na_element
FEATURE [App::DocumentObjectGroupPython] O_element090  label="O_element : 050"  # scripted group (container) (typed FeaturePython)
  n = 1
  ref = O_element
FEATURE [App::DocumentObjectGroupPython] G4_SODIUM_MONOXIDE  # scripted group (container) (typed FeaturePython)
  Dunit = g/cm3
  Dvalue = 2.27
  Group = -> [Na_element016,O_element090]
  conduct = 2
  density = 1
  expand = 3
  formula = G4_SODIUM_MONOXIDE
  name = G4_SODIUM_MONOXIDE
  specific = 4
FEATURE [App::DocumentObjectGroupPython] Na_element017  label="Na_element : 004"  # scripted group (container) (typed FeaturePython)
  n = 1
  ref = Na_element
FEATURE [App::DocumentObjectGroupPython] N_element040  label="N_element : 018"  # scripted group (container) (typed FeaturePython)
  n = 1
  ref = N_element
FEATURE [App::DocumentObjectGroupPython] O_element091  label="O_element : 051"  # scripted group (container) (typed FeaturePython)
  n = 3
  ref = O_element
FEATURE [App::DocumentObjectGroupPython] G4_SODIUM_NITRATE  # scripted group (container) (typed FeaturePython)
  Dunit = g/cm3
  Dvalue = 2.261
  Group = -> [Na_element017,N_element040,O_element091]
  conduct = 2
  density = 1
  expand = 3
  formula = G4_SODIUM_NITRATE
  name = G4_SODIUM_NITRATE
  specific = 4
FEATURE [App::DocumentObjectGroupPython] C_element105  label="C_element : 059"  # scripted group (container) (typed FeaturePython)
  n = 14
  ref = C_element
FEATURE [App::DocumentObjectGroupPython] H_element096  label="H_element : 053"  # scripted group (container) (typed FeaturePython)
  n = 12
  ref = H_element
FEATURE [App::DocumentObjectGroupPython] G4_STILBENE  # scripted group (container) (typed FeaturePython)
  Dunit = g/cm3
  Dvalue = 0.9707
  Group = -> [C_element105,H_element096]
  conduct = 2
  density = 1
  expand = 3
  formula = G4_STILBENE
  name = G4_STILBENE
  specific = 4
FEATURE [App::DocumentObjectGroupPython] C_element106  label="C_element : 12"  # scripted group (container) (typed FeaturePython)
  n = 12
  ref = C_element
FEATURE [App::DocumentObjectGroupPython] H_element097  label="H_element : 22"  # scripted group (container) (typed FeaturePython)
  n = 22
  ref = H_element
FEATURE [App::DocumentObjectGroupPython] O_element092  label="O_element : 11"  # scripted group (container) (typed FeaturePython)
  n = 11
  ref = O_element
FEATURE [App::DocumentObjectGroupPython] G4_SUCROSE  # scripted group (container) (typed FeaturePython)
  Dunit = g/cm3
  Dvalue = 1.5805
  Group = -> [C_element106,H_element097,O_element092]
  conduct = 2
  density = 1
  expand = 3
  formula = G4_SUCROSE
  name = G4_SUCROSE
  specific = 4
FEATURE [App::DocumentObjectGroupPython] C_element107  label="C_element : 18"  # scripted group (container) (typed FeaturePython)
  n = 18
  ref = C_element
FEATURE [App::DocumentObjectGroupPython] H_element098  label="H_element : 054"  # scripted group (container) (typed FeaturePython)
  n = 14
  ref = H_element
FEATURE [App::DocumentObjectGroupPython] G4_TERPHENYL  # scripted group (container) (typed FeaturePython)
  Dunit = g/cm3
  Dvalue = 1.24
  Group = -> [C_element107,H_element098]
  conduct = 2
  density = 1
  expand = 3
  formula = G4_TERPHENYL
  name = G4_TERPHENYL
  specific = 4
FEATURE [App::DocumentObjectGroupPython] H_element099  label="H_element : 0.146"  # scripted group (container) (typed FeaturePython)
  n = 0.106
FEATURE [App::DocumentObjectGroupPython] C_element108  label="C_element : 0.883"  # scripted group (container) (typed FeaturePython)
  n = 0.099
FEATURE [App::DocumentObjectGroupPython] N_element041  label="N_element : 0.020"  # scripted group (container) (typed FeaturePython)
  n = 0.02
FEATURE [App::DocumentObjectGroupPython] O_element093  label="O_element : 0.766"  # scripted group (container) (typed FeaturePython)
  n = 0.766
FEATURE [App::DocumentObjectGroupPython] Na_element018  label="Na_element : 0.101"  # scripted group (container) (typed FeaturePython)
  n = 0.002
FEATURE [App::DocumentObjectGroupPython] P_element010  label="P_element : 0.108"  # scripted group (container) (typed FeaturePython)
  n = 0.001
FEATURE [App::DocumentObjectGroupPython] S_element021  label="S_element : 0.022"  # scripted group (container) (typed FeaturePython)
  n = 0.002
FEATURE [App::DocumentObjectGroupPython] Cl_element024  label="Cl_element : 0.002"  # scripted group (container) (typed FeaturePython)
  n = 0.002
FEATURE [App::DocumentObjectGroupPython] K_element011  label="K_element : 0.017"  # scripted group (container) (typed FeaturePython)
  n = 0.002
FEATURE [App::DocumentObjectGroupPython] G4_TESTIS_ICRP  # scripted group (container) (typed FeaturePython)
  Dunit = g/cm3
  Dvalue = 1.04
  Group = -> [H_element099,C_element108,N_element041,O_element093,Na_element018,P_element010,S_element021,Cl_element024,K_element011]
  conduct = 2
  density = 1
  expand = 3
  formula = G4_TESTIS_ICRP
  name = G4_TESTIS_ICRP
  specific = 4
FEATURE [App::DocumentObjectGroupPython] C_element109  label="C_element : 060"  # scripted group (container) (typed FeaturePython)
  n = 2
  ref = C_element
FEATURE [App::DocumentObjectGroupPython] Cl_element025  label="Cl_element : 012"  # scripted group (container) (typed FeaturePython)
  n = 4
  ref = Cl_element
FEATURE [App::DocumentObjectGroupPython] G4_TETRACHLOROETHYLENE  # scripted group (container) (typed FeaturePython)
  Dunit = g/cm3
  Dvalue = 1.625
  Group = -> [C_element109,Cl_element025]
  conduct = 2
  density = 1
  expand = 3
  formula = G4_TETRACHLOROETHYLENE
  name = G4_TETRACHLOROETHYLENE
  specific = 4
FEATURE [App::DocumentObjectGroupPython] Tl_element001  label="Tl_element : 1"  # scripted group (container) (typed FeaturePython)
  n = 1
  ref = Tl_element
FEATURE [App::DocumentObjectGroupPython] Cl_element026  label="Cl_element : 013"  # scripted group (container) (typed FeaturePython)
  n = 1
  ref = Cl_element
FEATURE [App::DocumentObjectGroupPython] G4_THALLIUM_CHLORIDE  # scripted group (container) (typed FeaturePython)
  Dunit = g/cm3
  Dvalue = 7.004
  Group = -> [Tl_element001,Cl_element026]
  conduct = 2
  density = 1
  expand = 3
  formula = G4_THALLIUM_CHLORIDE
  name = G4_THALLIUM_CHLORIDE
  specific = 4
FEATURE [App::DocumentObjectGroupPython] H_element100  label="H_element : 0.147"  # scripted group (container) (typed FeaturePython)
  n = 0.105
FEATURE [App::DocumentObjectGroupPython] C_element110  label="C_element : 0.256"  # scripted group (container) (typed FeaturePython)
  n = 0.256
FEATURE [App::DocumentObjectGroupPython] N_element042  label="N_element : 0.760"  # scripted group (container) (typed FeaturePython)
  n = 0.027
FEATURE [App::DocumentObjectGroupPython] O_element094  label="O_element : 0.602"  # scripted group (container) (typed FeaturePython)
  n = 0.602
FEATURE [App::DocumentObjectGroupPython] Na_element019  label="Na_element : 0.102"  # scripted group (container) (typed FeaturePython)
  n = 0.001
FEATURE [App::DocumentObjectGroupPython] P_element011  label="P_element : 0.109"  # scripted group (container) (typed FeaturePython)
  n = 0.002
FEATURE [App::DocumentObjectGroupPython] S_element022  label="S_element : 0.023"  # scripted group (container) (typed FeaturePython)
  n = 0.003
FEATURE [App::DocumentObjectGroupPython] Cl_element027  label="Cl_element : 0.591"  # scripted group (container) (typed FeaturePython)
  n = 0.002
FEATURE [App::DocumentObjectGroupPython] K_element012  label="K_element : 0.018"  # scripted group (container) (typed FeaturePython)
  n = 0.002
FEATURE [App::DocumentObjectGroupPython] G4_TISSUE_SOFT_ICRP  # scripted group (container) (typed FeaturePython)
  Dunit = g/cm3
  Dvalue = 1.03
  Group = -> [H_element100,C_element110,N_element042,O_element094,Na_element019,P_element011,S_element022,Cl_element027,K_element012]
  conduct = 2
  density = 1
  expand = 3
  formula = G4_TISSUE_SOFT_ICRP
  name = G4_TISSUE_SOFT_ICRP
  specific = 4
FEATURE [App::DocumentObjectGroupPython] H_element101  label="H_element : 0.148"  # scripted group (container) (typed FeaturePython)
  n = 0.101
FEATURE [App::DocumentObjectGroupPython] C_element111  label="C_element : 0.111"  # scripted group (container) (typed FeaturePython)
  n = 0.111
FEATURE [App::DocumentObjectGroupPython] N_element043  label="N_element : 0.026"  # scripted group (container) (typed FeaturePython)
  n = 0.026
FEATURE [App::DocumentObjectGroupPython] O_element095  label="O_element : 0.762"  # scripted group (container) (typed FeaturePython)
  n = 0.762
FEATURE [App::DocumentObjectGroupPython] G4_TISSUE_SOFT_ICRU_4  label="G4_TISSUE_SOFT_ICRU-4"  # scripted group (container) (typed FeaturePython)
  Dunit = g/cm3
  Dvalue = 1
  Group = -> [H_element101,C_element111,N_element043,O_element095]
  conduct = 2
  density = 1
  expand = 3
  formula = G4_TISSUE_SOFT_ICRU-4
  name = G4_TISSUE_SOFT_ICRU-4
  specific = 4
FEATURE [App::DocumentObjectGroupPython] H_element102  label="H_element : 0.149"  # scripted group (container) (typed FeaturePython)
  n = 0.101869
FEATURE [App::DocumentObjectGroupPython] C_element112  label="C_element : 0.456"  # scripted group (container) (typed FeaturePython)
  n = 0.456179
FEATURE [App::DocumentObjectGroupPython] N_element044  label="N_element : 0.761"  # scripted group (container) (typed FeaturePython)
  n = 0.035172
FEATURE [App::DocumentObjectGroupPython] O_element096  label="O_element : 0.407"  # scripted group (container) (typed FeaturePython)
  n = 0.40678
FEATURE [App::DocumentObjectGroupPython] G4_TISSUE_METHANE  label="G4_TISSUE-METHANE"  # scripted group (container) (typed FeaturePython)
  Dunit = g/cm3
  Dvalue = 0.00106409
  Group = -> [H_element102,C_element112,N_element044,O_element096]
  conduct = 2
  density = 1
  expand = 3
  formula = G4_TISSUE-METHANE
  name = G4_TISSUE-METHANE
  specific = 4
FEATURE [App::DocumentObjectGroupPython] H_element103  label="H_element : 0.103"  # scripted group (container) (typed FeaturePython)
  n = 0.102672
FEATURE [App::DocumentObjectGroupPython] C_element113  label="C_element : 0.569"  # scripted group (container) (typed FeaturePython)
  n = 0.56894
FEATURE [App::DocumentObjectGroupPython] N_element045  label="N_element : 0.762"  # scripted group (container) (typed FeaturePython)
  n = 0.035022
FEATURE [App::DocumentObjectGroupPython] O_element097  label="O_element : 0.293"  # scripted group (container) (typed FeaturePython)
  n = 0.293366
FEATURE [App::DocumentObjectGroupPython] G4_TISSUE_PROPANE  label="G4_TISSUE-PROPANE"  # scripted group (container) (typed FeaturePython)
  Dunit = g/cm3
  Dvalue = 0.00182628
  Group = -> [H_element103,C_element113,N_element045,O_element097]
  conduct = 2
  density = 1
  expand = 3
  formula = G4_TISSUE-PROPANE
  name = G4_TISSUE-PROPANE
  specific = 4
FEATURE [App::DocumentObjectGroupPython] Ti_element003  label="Ti_element : 1"  # scripted group (container) (typed FeaturePython)
  n = 1
  ref = Ti_element
FEATURE [App::DocumentObjectGroupPython] O_element098  label="O_element : 052"  # scripted group (container) (typed FeaturePython)
  n = 2
  ref = O_element
FEATURE [App::DocumentObjectGroupPython] G4_TITANIUM_DIOXIDE  # scripted group (container) (typed FeaturePython)
  Dunit = g/cm3
  Dvalue = 4.26
  Group = -> [Ti_element003,O_element098]
  conduct = 2
  density = 1
  expand = 3
  formula = G4_TITANIUM_DIOXIDE
  name = G4_TITANIUM_DIOXIDE
  specific = 4
FEATURE [App::DocumentObjectGroupPython] C_element114  label="C_element : 061"  # scripted group (container) (typed FeaturePython)
  n = 7
  ref = C_element
FEATURE [App::DocumentObjectGroupPython] H_element104  label="H_element : 055"  # scripted group (container) (typed FeaturePython)
  n = 8
  ref = H_element
FEATURE [App::DocumentObjectGroupPython] G4_TOLUENE  # scripted group (container) (typed FeaturePython)
  Dunit = g/cm3
  Dvalue = 0.8669
  Group = -> [C_element114,H_element104]
  conduct = 2
  density = 1
  expand = 3
  formula = G4_TOLUENE
  name = G4_TOLUENE
  specific = 4
FEATURE [App::DocumentObjectGroupPython] C_element115  label="C_element : 062"  # scripted group (container) (typed FeaturePython)
  n = 2
  ref = C_element
FEATURE [App::DocumentObjectGroupPython] H_element105  label="H_element : 056"  # scripted group (container) (typed FeaturePython)
  n = 1
  ref = H_element
FEATURE [App::DocumentObjectGroupPython] Cl_element028  label="Cl_element : 014"  # scripted group (container) (typed FeaturePython)
  n = 3
  ref = Cl_element
FEATURE [App::DocumentObjectGroupPython] G4_TRICHLOROETHYLENE  # scripted group (container) (typed FeaturePython)
  Dunit = g/cm3
  Dvalue = 1.46
  Group = -> [C_element115,H_element105,Cl_element028]
  conduct = 2
  density = 1
  expand = 3
  formula = G4_TRICHLOROETHYLENE
  name = G4_TRICHLOROETHYLENE
  specific = 4
FEATURE [App::DocumentObjectGroupPython] C_element116  label="C_element : 063"  # scripted group (container) (typed FeaturePython)
  n = 6
  ref = C_element
FEATURE [App::DocumentObjectGroupPython] H_element106  label="H_element : 15"  # scripted group (container) (typed FeaturePython)
  n = 15
  ref = H_element
FEATURE [App::DocumentObjectGroupPython] O_element099  label="O_element : 053"  # scripted group (container) (typed FeaturePython)
  n = 4
  ref = O_element
FEATURE [App::DocumentObjectGroupPython] P_element012  label="P_element : 1"  # scripted group (container) (typed FeaturePython)
  n = 1
  ref = P_element
FEATURE [App::DocumentObjectGroupPython] G4_TRIETHYL_PHOSPHATE  # scripted group (container) (typed FeaturePython)
  Dunit = g/cm3
  Dvalue = 1.07
  Group = -> [C_element116,H_element106,O_element099,P_element012]
  conduct = 2
  density = 1
  expand = 3
  formula = G4_TRIETHYL_PHOSPHATE
  name = G4_TRIETHYL_PHOSPHATE
  specific = 4
FEATURE [App::DocumentObjectGroupPython] W_element003  label="W_element : 003"  # scripted group (container) (typed FeaturePython)
  n = 1
  ref = W_element
FEATURE [App::DocumentObjectGroupPython] F_element017  label="F_element : 6"  # scripted group (container) (typed FeaturePython)
  n = 6
  ref = F_element
FEATURE [App::DocumentObjectGroupPython] G4_TUNGSTEN_HEXAFLUORIDE  # scripted group (container) (typed FeaturePython)
  Dunit = g/cm3
  Dvalue = 2.4
  Group = -> [W_element003,F_element017]
  conduct = 2
  density = 1
  expand = 3
  formula = G4_TUNGSTEN_HEXAFLUORIDE
  name = G4_TUNGSTEN_HEXAFLUORIDE
  specific = 4
FEATURE [App::DocumentObjectGroupPython] U_element001  label="U_element : 1"  # scripted group (container) (typed FeaturePython)
  n = 1
  ref = U_element
FEATURE [App::DocumentObjectGroupPython] C_element117  label="C_element : 064"  # scripted group (container) (typed FeaturePython)
  n = 2
  ref = C_element
FEATURE [App::DocumentObjectGroupPython] G4_URANIUM_DICARBIDE  # scripted group (container) (typed FeaturePython)
  Dunit = g/cm3
  Dvalue = 11.28
  Group = -> [U_element001,C_element117]
  conduct = 2
  density = 1
  expand = 3
  formula = G4_URANIUM_DICARBIDE
  name = G4_URANIUM_DICARBIDE
  specific = 4
FEATURE [App::DocumentObjectGroupPython] U_element002  label="U_element : 002"  # scripted group (container) (typed FeaturePython)
  n = 1
  ref = U_element
FEATURE [App::DocumentObjectGroupPython] C_element118  label="C_element : 065"  # scripted group (container) (typed FeaturePython)
  n = 1
  ref = C_element
FEATURE [App::DocumentObjectGroupPython] G4_URANIUM_MONOCARBIDE  # scripted group (container) (typed FeaturePython)
  Dunit = g/cm3
  Dvalue = 13.63
  Group = -> [U_element002,C_element118]
  conduct = 2
  density = 1
  expand = 3
  formula = G4_URANIUM_MONOCARBIDE
  name = G4_URANIUM_MONOCARBIDE
  specific = 4
FEATURE [App::DocumentObjectGroupPython] U_element003  label="U_element : 003"  # scripted group (container) (typed FeaturePython)
  n = 1
  ref = U_element
FEATURE [App::DocumentObjectGroupPython] O_element100  label="O_element : 054"  # scripted group (container) (typed FeaturePython)
  n = 2
  ref = O_element
FEATURE [App::DocumentObjectGroupPython] G4_URANIUM_OXIDE  # scripted group (container) (typed FeaturePython)
  Dunit = g/cm3
  Dvalue = 10.96
  Group = -> [U_element003,O_element100]
  conduct = 2
  density = 1
  expand = 3
  formula = G4_URANIUM_OXIDE
  name = G4_URANIUM_OXIDE
  specific = 4
FEATURE [App::DocumentObjectGroupPython] C_element119  label="C_element : 066"  # scripted group (container) (typed FeaturePython)
  n = 1
  ref = C_element
FEATURE [App::DocumentObjectGroupPython] H_element107  label="H_element : 057"  # scripted group (container) (typed FeaturePython)
  n = 4
  ref = H_element
FEATURE [App::DocumentObjectGroupPython] N_element046  label="N_element : 019"  # scripted group (container) (typed FeaturePython)
  n = 2
  ref = N_element
FEATURE [App::DocumentObjectGroupPython] O_element101  label="O_element : 055"  # scripted group (container) (typed FeaturePython)
  n = 1
  ref = O_element
FEATURE [App::DocumentObjectGroupPython] G4_UREA  # scripted group (container) (typed FeaturePython)
  Dunit = g/cm3
  Dvalue = 1.323
  Group = -> [C_element119,H_element107,N_element046,O_element101]
  conduct = 2
  density = 1
  expand = 3
  formula = G4_UREA
  name = G4_UREA
  specific = 4
FEATURE [App::DocumentObjectGroupPython] C_element120  label="C_element : 067"  # scripted group (container) (typed FeaturePython)
  n = 5
  ref = C_element
FEATURE [App::DocumentObjectGroupPython] H_element108  label="H_element : 058"  # scripted group (container) (typed FeaturePython)
  n = 11
  ref = H_element
FEATURE [App::DocumentObjectGroupPython] N_element047  label="N_element : 020"  # scripted group (container) (typed FeaturePython)
  n = 1
  ref = N_element
FEATURE [App::DocumentObjectGroupPython] O_element102  label="O_element : 056"  # scripted group (container) (typed FeaturePython)
  n = 2
  ref = O_element
FEATURE [App::DocumentObjectGroupPython] G4_VALINE  # scripted group (container) (typed FeaturePython)
  Dunit = g/cm3
  Dvalue = 1.23
  Group = -> [C_element120,H_element108,N_element047,O_element102]
  conduct = 2
  density = 1
  expand = 3
  formula = G4_VALINE
  name = G4_VALINE
  specific = 4
FEATURE [App::DocumentObjectGroupPython] H_element109  label="H_element : 0.009"  # scripted group (container) (typed FeaturePython)
  n = 0.009417
FEATURE [App::DocumentObjectGroupPython] C_element121  label="C_element : 0.281"  # scripted group (container) (typed FeaturePython)
  n = 0.280555
FEATURE [App::DocumentObjectGroupPython] F_element018  label="F_element : 0.710"  # scripted group (container) (typed FeaturePython)
  n = 0.710028
FEATURE [App::DocumentObjectGroupPython] G4_VITON  # scripted group (container) (typed FeaturePython)
  Dunit = g/cm3
  Dvalue = 1.8
  Group = -> [H_element109,C_element121,F_element018]
  conduct = 2
  density = 1
  expand = 3
  formula = G4_VITON
  name = G4_VITON
  specific = 4
FEATURE [App::DocumentObjectGroupPython] H_element110  label="H_element : 059"  # scripted group (container) (typed FeaturePython)
  n = 2
  ref = H_element
FEATURE [App::DocumentObjectGroupPython] O_element103  label="O_element : 057"  # scripted group (container) (typed FeaturePython)
  n = 1
  ref = O_element
FEATURE [App::DocumentObjectGroupPython] G4_WATER  # scripted group (container) (typed FeaturePython)
  Dunit = g/cm3
  Dvalue = 1
  Group = -> [H_element110,O_element103]
  conduct = 2
  density = 1
  expand = 3
  formula = G4_WATER
  name = G4_WATER
  specific = 4
FEATURE [App::DocumentObjectGroupPython] H_element111  label="H_element : 060"  # scripted group (container) (typed FeaturePython)
  n = 2
  ref = H_element
FEATURE [App::DocumentObjectGroupPython] O_element104  label="O_element : 058"  # scripted group (container) (typed FeaturePython)
  n = 1
  ref = O_element
FEATURE [App::DocumentObjectGroupPython] G4_WATER_VAPOR  # scripted group (container) (typed FeaturePython)
  Dunit = g/cm3
  Dvalue = 0.000756182
  Group = -> [H_element111,O_element104]
  conduct = 2
  density = 1
  expand = 3
  formula = G4_WATER_VAPOR
  name = G4_WATER_VAPOR
  specific = 4
FEATURE [App::DocumentObjectGroupPython] C_element122  label="C_element : 068"  # scripted group (container) (typed FeaturePython)
  n = 8
  ref = C_element
FEATURE [App::DocumentObjectGroupPython] H_element112  label="H_element : 061"  # scripted group (container) (typed FeaturePython)
  n = 10
  ref = H_element
FEATURE [App::DocumentObjectGroupPython] G4_XYLENE  # scripted group (container) (typed FeaturePython)
  Dunit = g/cm3
  Dvalue = 0.87
  Group = -> [C_element122,H_element112]
  conduct = 2
  density = 1
  expand = 3
  formula = G4_XYLENE
  name = G4_XYLENE
  specific = 4
FEATURE [App::DocumentObjectGroupPython] C_element123  label="C_element : 069"  # scripted group (container) (typed FeaturePython)
  n = 1
  ref = C_element
FEATURE [App::DocumentObjectGroupPython] G4_GRAPHITE  # scripted group (container) (typed FeaturePython)
  Dunit = g/cm3
  Dvalue = 2.21
  Group = -> [C_element123]
  conduct = 2
  density = 1
  expand = 3
  formula = G4_GRAPHITE
  name = G4_GRAPHITE
  specific = 4
FEATURE [App::DocumentObjectGroupPython] NIST  # scripted group (container) (typed FeaturePython)
  Group = -> [G4_A_150_TISSUE,G4_ACETONE,G4_ACETYLENE,G4_ADENINE,G4_ADIPOSE_TISSUE_ICRP,G4_AIR,G4_ALANINE,G4_ALUMINUM_OXIDE,G4_AMBER,G4_AMMONIA,G4_ANILINE,G4_ANTHRACENE,G4_B_100_BONE,G4_BAKELITE,G4_BARIUM_FLUORIDE,G4_BARIUM_SULFATE,G4_BENZENE,G4_BERYLLIUM_OXIDE,G4_BGO,G4_BLOOD_ICRP,G4_BONE_COMPACT_ICRU,G4_BONE_CORTICAL_ICRP,G4_BORON_CARBIDE,G4_BORON_OXIDE,G4_BRAIN_ICRP,G4_BUTANE,G4_N_BUTYL_ALCOHOL,G4_C_552,+152 more]
FEATURE [App::DocumentObjectGroupPython] H_element113  label="H_element : 062"  # scripted group (container) (typed FeaturePython)
  n = 1
  ref = H_element
FEATURE [App::DocumentObjectGroupPython] G4_H  # scripted group (container) (typed FeaturePython)
  Dunit = g/cm3
  Dvalue = 8.3748e-05
  Group = -> [H_element113]
  conduct = 2
  density = 1
  expand = 3
  formula = H
  name = G4_H
  specific = 4
FEATURE [App::DocumentObjectGroupPython] He_element001  label="He_element : 1"  # scripted group (container) (typed FeaturePython)
  n = 1
  ref = He_element
FEATURE [App::DocumentObjectGroupPython] G4_He  # scripted group (container) (typed FeaturePython)
  Dunit = g/cm3
  Dvalue = 0.000166322
  Group = -> [He_element001]
  conduct = 2
  density = 1
  expand = 3
  formula = He
  name = G4_He
  specific = 4
FEATURE [App::DocumentObjectGroupPython] Li_element008  label="Li_element : 008"  # scripted group (container) (typed FeaturePython)
  n = 1
  ref = Li_element
FEATURE [App::DocumentObjectGroupPython] G4_Li  # scripted group (container) (typed FeaturePython)
  Dunit = g/cm3
  Dvalue = 0.534
  Group = -> [Li_element008]
  conduct = 2
  density = 1
  expand = 3
  formula = Li
  name = G4_Li
  specific = 4
FEATURE [App::DocumentObjectGroupPython] Be_element002  label="Be_element : 002"  # scripted group (container) (typed FeaturePython)
  n = 1
  ref = Be_element
FEATURE [App::DocumentObjectGroupPython] G4_Be  # scripted group (container) (typed FeaturePython)
  Dunit = g/cm3
  Dvalue = 1.848
  Group = -> [Be_element002]
  conduct = 2
  density = 1
  expand = 3
  formula = Be
  name = G4_Be
  specific = 4
FEATURE [App::DocumentObjectGroupPython] B_element007  label="B_element : 007"  # scripted group (container) (typed FeaturePython)
  n = 1
  ref = B_element
FEATURE [App::DocumentObjectGroupPython] G4_B  # scripted group (container) (typed FeaturePython)
  Dunit = g/cm3
  Dvalue = 2.37
  Group = -> [B_element007]
  conduct = 2
  density = 1
  expand = 3
  formula = B
  name = G4_B
  specific = 4
FEATURE [App::DocumentObjectGroupPython] C_element124  label="C_element : 070"  # scripted group (container) (typed FeaturePython)
  n = 1
  ref = C_element
FEATURE [App::DocumentObjectGroupPython] G4_C  # scripted group (container) (typed FeaturePython)
  Dunit = g/cm3
  Dvalue = 2
  Group = -> [C_element124]
  conduct = 2
  density = 1
  expand = 3
  formula = C
  name = G4_C
  specific = 4
FEATURE [App::DocumentObjectGroupPython] N_element048  label="N_element : 021"  # scripted group (container) (typed FeaturePython)
  n = 1
  ref = N_element
FEATURE [App::DocumentObjectGroupPython] G4_N  # scripted group (container) (typed FeaturePython)
  Dunit = g/cm3
  Dvalue = 0.0011652
  Group = -> [N_element048]
  conduct = 2
  density = 1
  expand = 3
  formula = N
  name = G4_N
  specific = 4
FEATURE [App::DocumentObjectGroupPython] O_element105  label="O_element : 059"  # scripted group (container) (typed FeaturePython)
  n = 1
  ref = O_element
FEATURE [App::DocumentObjectGroupPython] G4_O  # scripted group (container) (typed FeaturePython)
  Dunit = g/cm3
  Dvalue = 0.00133151
  Group = -> [O_element105]
  conduct = 2
  density = 1
  expand = 3
  formula = O
  name = G4_O
  specific = 4
FEATURE [App::DocumentObjectGroupPython] F_element019  label="F_element : 008"  # scripted group (container) (typed FeaturePython)
  n = 1
  ref = F_element
FEATURE [App::DocumentObjectGroupPython] G4_F  # scripted group (container) (typed FeaturePython)
  Dunit = g/cm3
  Dvalue = 0.00158029
  Group = -> [F_element019]
  conduct = 2
  density = 1
  expand = 3
  formula = F
  name = G4_F
  specific = 4
FEATURE [App::DocumentObjectGroupPython] Ne_element001  label="Ne_element : 1"  # scripted group (container) (typed FeaturePython)
  n = 1
  ref = Ne_element
FEATURE [App::DocumentObjectGroupPython] G4_Ne  # scripted group (container) (typed FeaturePython)
  Dunit = g/cm3
  Dvalue = 0.000838505
  Group = -> [Ne_element001]
  conduct = 2
  density = 1
  expand = 3
  formula = Ne
  name = G4_Ne
  specific = 4
FEATURE [App::DocumentObjectGroupPython] Na_element020  label="Na_element : 005"  # scripted group (container) (typed FeaturePython)
  n = 1
  ref = Na_element
FEATURE [App::DocumentObjectGroupPython] G4_Na  # scripted group (container) (typed FeaturePython)
  Dunit = g/cm3
  Dvalue = 0.971
  Group = -> [Na_element020]
  conduct = 2
  density = 1
  expand = 3
  formula = Na
  name = G4_Na
  specific = 4
FEATURE [App::DocumentObjectGroupPython] Mg_element011  label="Mg_element : 005"  # scripted group (container) (typed FeaturePython)
  n = 1
  ref = Mg_element
FEATURE [App::DocumentObjectGroupPython] G4_Mg  # scripted group (container) (typed FeaturePython)
  Dunit = g/cm3
  Dvalue = 1.74
  Group = -> [Mg_element011]
  conduct = 2
  density = 1
  expand = 3
  formula = Mg
  name = G4_Mg
  specific = 4
FEATURE [App::DocumentObjectGroupPython] Al_element004  label="Al_element : 1"  # scripted group (container) (typed FeaturePython)
  n = 1
  ref = Al_element
FEATURE [App::DocumentObjectGroupPython] G4_Al  # scripted group (container) (typed FeaturePython)
  Dunit = g/cm3
  Dvalue = 2.699
  Group = -> [Al_element004]
  conduct = 2
  density = 1
  expand = 3
  formula = Al
  name = G4_Al
  specific = 4
FEATURE [App::DocumentObjectGroupPython] Si_element007  label="Si_element : 002"  # scripted group (container) (typed FeaturePython)
  n = 1
  ref = Si_element
FEATURE [App::DocumentObjectGroupPython] G4_Si  # scripted group (container) (typed FeaturePython)
  Dunit = g/cm3
  Dvalue = 2.33
  Group = -> [Si_element007]
  conduct = 2
  density = 1
  expand = 3
  formula = Si
  name = G4_Si
  specific = 4
FEATURE [App::DocumentObjectGroupPython] P_element013  label="P_element : 002"  # scripted group (container) (typed FeaturePython)
  n = 1
  ref = P_element
FEATURE [App::DocumentObjectGroupPython] G4_P  # scripted group (container) (typed FeaturePython)
  Dunit = g/cm3
  Dvalue = 2.2
  Group = -> [P_element013]
  conduct = 2
  density = 1
  expand = 3
  formula = P
  name = G4_P
  specific = 4
FEATURE [App::DocumentObjectGroupPython] S_element023  label="S_element : 007"  # scripted group (container) (typed FeaturePython)
  n = 1
  ref = S_element
FEATURE [App::DocumentObjectGroupPython] G4_S  # scripted group (container) (typed FeaturePython)
  Dunit = g/cm3
  Dvalue = 2
  Group = -> [S_element023]
  conduct = 2
  density = 1
  expand = 3
  formula = S
  name = G4_S
  specific = 4
FEATURE [App::DocumentObjectGroupPython] Cl_element029  label="Cl_element : 015"  # scripted group (container) (typed FeaturePython)
  n = 1
  ref = Cl_element
FEATURE [App::DocumentObjectGroupPython] G4_Cl  # scripted group (container) (typed FeaturePython)
  Dunit = g/cm3
  Dvalue = 0.00299473
  Group = -> [Cl_element029]
  conduct = 2
  density = 1
  expand = 3
  formula = Cl
  name = G4_Cl
  specific = 4
FEATURE [App::DocumentObjectGroupPython] Ar_element002  label="Ar_element : 1"  # scripted group (container) (typed FeaturePython)
  n = 1
  ref = Ar_element
FEATURE [App::DocumentObjectGroupPython] G4_Ar  # scripted group (container) (typed FeaturePython)
  Dunit = g/cm3
  Dvalue = 0.00166201
  Group = -> [Ar_element002]
  conduct = 2
  density = 1
  expand = 3
  formula = Ar
  name = G4_Ar
  specific = 4
FEATURE [App::DocumentObjectGroupPython] K_element013  label="K_element : 003"  # scripted group (container) (typed FeaturePython)
  n = 1
  ref = K_element
FEATURE [App::DocumentObjectGroupPython] G4_K  # scripted group (container) (typed FeaturePython)
  Dunit = g/cm3
  Dvalue = 0.862
  Group = -> [K_element013]
  conduct = 2
  density = 1
  expand = 3
  formula = K
  name = G4_K
  specific = 4
FEATURE [App::DocumentObjectGroupPython] Ca_element014  label="Ca_element : 007"  # scripted group (container) (typed FeaturePython)
  n = 1
  ref = Ca_element
FEATURE [App::DocumentObjectGroupPython] G4_Ca  # scripted group (container) (typed FeaturePython)
  Dunit = g/cm3
  Dvalue = 1.55
  Group = -> [Ca_element014]
  conduct = 2
  density = 1
  expand = 3
  formula = Ca
  name = G4_Ca
  specific = 4
FEATURE [App::DocumentObjectGroupPython] Sc_element001  label="Sc_element : 1"  # scripted group (container) (typed FeaturePython)
  n = 1
  ref = Sc_element
FEATURE [App::DocumentObjectGroupPython] G4_Sc  # scripted group (container) (typed FeaturePython)
  Dunit = g/cm3
  Dvalue = 2.989
  Group = -> [Sc_element001]
  conduct = 2
  density = 1
  expand = 3
  formula = Sc
  name = G4_Sc
  specific = 4
FEATURE [App::DocumentObjectGroupPython] Ti_element004  label="Ti_element : 002"  # scripted group (container) (typed FeaturePython)
  n = 1
  ref = Ti_element
FEATURE [App::DocumentObjectGroupPython] G4_Ti  # scripted group (container) (typed FeaturePython)
  Dunit = g/cm3
  Dvalue = 4.54
  Group = -> [Ti_element004]
  conduct = 2
  density = 1
  expand = 3
  formula = Ti
  name = G4_Ti
  specific = 4
FEATURE [App::DocumentObjectGroupPython] V_element001  label="V_element : 1"  # scripted group (container) (typed FeaturePython)
  n = 1
  ref = V_element
FEATURE [App::DocumentObjectGroupPython] G4_V  # scripted group (container) (typed FeaturePython)
  Dunit = g/cm3
  Dvalue = 6.11
  Group = -> [V_element001]
  conduct = 2
  density = 1
  expand = 3
  formula = V
  name = G4_V
  specific = 4
FEATURE [App::DocumentObjectGroupPython] Cr_element001  label="Cr_element : 1"  # scripted group (container) (typed FeaturePython)
  n = 1
  ref = Cr_element
FEATURE [App::DocumentObjectGroupPython] G4_Cr  # scripted group (container) (typed FeaturePython)
  Dunit = g/cm3
  Dvalue = 7.18
  Group = -> [Cr_element001]
  conduct = 2
  density = 1
  expand = 3
  formula = Cr
  name = G4_Cr
  specific = 4
FEATURE [App::DocumentObjectGroupPython] Mn_element001  label="Mn_element : 1"  # scripted group (container) (typed FeaturePython)
  n = 1
  ref = Mn_element
FEATURE [App::DocumentObjectGroupPython] G4_Mn  # scripted group (container) (typed FeaturePython)
  Dunit = g/cm3
  Dvalue = 7.44
  Group = -> [Mn_element001]
  conduct = 2
  density = 1
  expand = 3
  formula = Mn
  name = G4_Mn
  specific = 4
FEATURE [App::DocumentObjectGroupPython] Fe_element007  label="Fe_element : 004"  # scripted group (container) (typed FeaturePython)
  n = 1
  ref = Fe_element
FEATURE [App::DocumentObjectGroupPython] G4_Fe  # scripted group (container) (typed FeaturePython)
  Dunit = g/cm3
  Dvalue = 7.874
  Group = -> [Fe_element007]
  conduct = 2
  density = 1
  expand = 3
  formula = Fe
  name = G4_Fe
  specific = 4
FEATURE [App::DocumentObjectGroupPython] Co_element001  label="Co_element : 1"  # scripted group (container) (typed FeaturePython)
  n = 1
  ref = Co_element
FEATURE [App::DocumentObjectGroupPython] G4_Co  # scripted group (container) (typed FeaturePython)
  Dunit = g/cm3
  Dvalue = 8.9
  Group = -> [Co_element001]
  conduct = 2
  density = 1
  expand = 3
  formula = Co
  name = G4_Co
  specific = 4
FEATURE [App::DocumentObjectGroupPython] Ni_element001  label="Ni_element : 1"  # scripted group (container) (typed FeaturePython)
  n = 1
  ref = Ni_element
FEATURE [App::DocumentObjectGroupPython] G4_Ni  # scripted group (container) (typed FeaturePython)
  Dunit = g/cm3
  Dvalue = 8.902
  Group = -> [Ni_element001]
  conduct = 2
  density = 1
  expand = 3
  formula = Ni
  name = G4_Ni
  specific = 4
FEATURE [App::DocumentObjectGroupPython] Cu_element001  label="Cu_element : 1"  # scripted group (container) (typed FeaturePython)
  n = 1
  ref = Cu_element
FEATURE [App::DocumentObjectGroupPython] G4_Cu  # scripted group (container) (typed FeaturePython)
  Dunit = g/cm3
  Dvalue = 8.96
  Group = -> [Cu_element001]
  conduct = 2
  density = 1
  expand = 3
  formula = Cu
  name = G4_Cu
  specific = 4
FEATURE [App::DocumentObjectGroupPython] Zn_element001  label="Zn_element : 1"  # scripted group (container) (typed FeaturePython)
  n = 1
  ref = Zn_element
FEATURE [App::DocumentObjectGroupPython] G4_Zn  # scripted group (container) (typed FeaturePython)
  Dunit = g/cm3
  Dvalue = 7.133
  Group = -> [Zn_element001]
  conduct = 2
  density = 1
  expand = 3
  formula = Zn
  name = G4_Zn
  specific = 4
FEATURE [App::DocumentObjectGroupPython] Ga_element002  label="Ga_element : 002"  # scripted group (container) (typed FeaturePython)
  n = 1
  ref = Ga_element
FEATURE [App::DocumentObjectGroupPython] G4_Ga  # scripted group (container) (typed FeaturePython)
  Dunit = g/cm3
  Dvalue = 5.904
  Group = -> [Ga_element002]
  conduct = 2
  density = 1
  expand = 3
  formula = Ga
  name = G4_Ga
  specific = 4
FEATURE [App::DocumentObjectGroupPython] Ge_element002  label="Ge_element : 1"  # scripted group (container) (typed FeaturePython)
  n = 1
  ref = Ge_element
FEATURE [App::DocumentObjectGroupPython] G4_Ge  # scripted group (container) (typed FeaturePython)
  Dunit = g/cm3
  Dvalue = 5.323
  Group = -> [Ge_element002]
  conduct = 2
  density = 1
  expand = 3
  formula = Ge
  name = G4_Ge
  specific = 4
FEATURE [App::DocumentObjectGroupPython] As_element003  label="As_element : 002"  # scripted group (container) (typed FeaturePython)
  n = 1
  ref = As_element
FEATURE [App::DocumentObjectGroupPython] G4_As  # scripted group (container) (typed FeaturePython)
  Dunit = g/cm3
  Dvalue = 5.73
  Group = -> [As_element003]
  conduct = 2
  density = 1
  expand = 3
  formula = As
  name = G4_As
  specific = 4
FEATURE [App::DocumentObjectGroupPython] Se_element001  label="Se_element : 1"  # scripted group (container) (typed FeaturePython)
  n = 1
  ref = Se_element
FEATURE [App::DocumentObjectGroupPython] G4_Se  # scripted group (container) (typed FeaturePython)
  Dunit = g/cm3
  Dvalue = 4.5
  Group = -> [Se_element001]
  conduct = 2
  density = 1
  expand = 3
  formula = Se
  name = G4_Se
  specific = 4
FEATURE [App::DocumentObjectGroupPython] Br_element007  label="Br_element : 004"  # scripted group (container) (typed FeaturePython)
  n = 1
  ref = Br_element
FEATURE [App::DocumentObjectGroupPython] G4_Br  # scripted group (container) (typed FeaturePython)
  Dunit = g/cm3
  Dvalue = 0.0070721
  Group = -> [Br_element007]
  conduct = 2
  density = 1
  expand = 3
  formula = Br
  name = G4_Br
  specific = 4
FEATURE [App::DocumentObjectGroupPython] Kr_element001  label="Kr_element : 1"  # scripted group (container) (typed FeaturePython)
  n = 1
  ref = Kr_element
FEATURE [App::DocumentObjectGroupPython] G4_Kr  # scripted group (container) (typed FeaturePython)
  Dunit = g/cm3
  Dvalue = 0.00347832
  Group = -> [Kr_element001]
  conduct = 2
  density = 1
  expand = 3
  formula = Kr
  name = G4_Kr
  specific = 4
FEATURE [App::DocumentObjectGroupPython] Rb_element001  label="Rb_element : 1"  # scripted group (container) (typed FeaturePython)
  n = 1
  ref = Rb_element
FEATURE [App::DocumentObjectGroupPython] G4_Rb  # scripted group (container) (typed FeaturePython)
  Dunit = g/cm3
  Dvalue = 1.532
  Group = -> [Rb_element001]
  conduct = 2
  density = 1
  expand = 3
  formula = Rb
  name = G4_Rb
  specific = 4
FEATURE [App::DocumentObjectGroupPython] Sr_element001  label="Sr_element : 1"  # scripted group (container) (typed FeaturePython)
  n = 1
  ref = Sr_element
FEATURE [App::DocumentObjectGroupPython] G4_Sr  # scripted group (container) (typed FeaturePython)
  Dunit = g/cm3
  Dvalue = 2.54
  Group = -> [Sr_element001]
  conduct = 2
  density = 1
  expand = 3
  formula = Sr
  name = G4_Sr
  specific = 4
FEATURE [App::DocumentObjectGroupPython] Y_element001  label="Y_element : 1"  # scripted group (container) (typed FeaturePython)
  n = 1
  ref = Y_element
FEATURE [App::DocumentObjectGroupPython] G4_Y  # scripted group (container) (typed FeaturePython)
  Dunit = g/cm3
  Dvalue = 4.469
  Group = -> [Y_element001]
  conduct = 2
  density = 1
  expand = 3
  formula = Y
  name = G4_Y
  specific = 4
FEATURE [App::DocumentObjectGroupPython] Zr_element001  label="Zr_element : 1"  # scripted group (container) (typed FeaturePython)
  n = 1
  ref = Zr_element
FEATURE [App::DocumentObjectGroupPython] G4_Zr  # scripted group (container) (typed FeaturePython)
  Dunit = g/cm3
  Dvalue = 6.506
  Group = -> [Zr_element001]
  conduct = 2
  density = 1
  expand = 3
  formula = Zr
  name = G4_Zr
  specific = 4
FEATURE [App::DocumentObjectGroupPython] Nb_element001  label="Nb_element : 1"  # scripted group (container) (typed FeaturePython)
  n = 1
  ref = Nb_element
FEATURE [App::DocumentObjectGroupPython] G4_Nb  # scripted group (container) (typed FeaturePython)
  Dunit = g/cm3
  Dvalue = 8.57
  Group = -> [Nb_element001]
  conduct = 2
  density = 1
  expand = 3
  formula = Nb
  name = G4_Nb
  specific = 4
FEATURE [App::DocumentObjectGroupPython] Mo_element001  label="Mo_element : 1"  # scripted group (container) (typed FeaturePython)
  n = 1
  ref = Mo_element
FEATURE [App::DocumentObjectGroupPython] G4_Mo  # scripted group (container) (typed FeaturePython)
  Dunit = g/cm3
  Dvalue = 10.22
  Group = -> [Mo_element001]
  conduct = 2
  density = 1
  expand = 3
  formula = Mo
  name = G4_Mo
  specific = 4
FEATURE [App::DocumentObjectGroupPython] Tc_element001  label="Tc_element : 1"  # scripted group (container) (typed FeaturePython)
  n = 1
  ref = Tc_element
FEATURE [App::DocumentObjectGroupPython] G4_Tc  # scripted group (container) (typed FeaturePython)
  Dunit = g/cm3
  Dvalue = 11.5
  Group = -> [Tc_element001]
  conduct = 2
  density = 1
  expand = 3
  formula = Tc
  name = G4_Tc
  specific = 4
FEATURE [App::DocumentObjectGroupPython] Ru_element001  label="Ru_element : 1"  # scripted group (container) (typed FeaturePython)
  n = 1
  ref = Ru_element
FEATURE [App::DocumentObjectGroupPython] G4_Ru  # scripted group (container) (typed FeaturePython)
  Dunit = g/cm3
  Dvalue = 12.41
  Group = -> [Ru_element001]
  conduct = 2
  density = 1
  expand = 3
  formula = Ru
  name = G4_Ru
  specific = 4
FEATURE [App::DocumentObjectGroupPython] Rh_element001  label="Rh_element : 1"  # scripted group (container) (typed FeaturePython)
  n = 1
  ref = Rh_element
FEATURE [App::DocumentObjectGroupPython] G4_Rh  # scripted group (container) (typed FeaturePython)
  Dunit = g/cm3
  Dvalue = 12.41
  Group = -> [Rh_element001]
  conduct = 2
  density = 1
  expand = 3
  formula = Rh
  name = G4_Rh
  specific = 4
FEATURE [App::DocumentObjectGroupPython] Pd_element001  label="Pd_element : 1"  # scripted group (container) (typed FeaturePython)
  n = 1
  ref = Pd_element
FEATURE [App::DocumentObjectGroupPython] G4_Pd  # scripted group (container) (typed FeaturePython)
  Dunit = g/cm3
  Dvalue = 12.02
  Group = -> [Pd_element001]
  conduct = 2
  density = 1
  expand = 3
  formula = Pd
  name = G4_Pd
  specific = 4
FEATURE [App::DocumentObjectGroupPython] Ag_element006  label="Ag_element : 004"  # scripted group (container) (typed FeaturePython)
  n = 1
  ref = Ag_element
FEATURE [App::DocumentObjectGroupPython] G4_Ag  # scripted group (container) (typed FeaturePython)
  Dunit = g/cm3
  Dvalue = 10.5
  Group = -> [Ag_element006]
  conduct = 2
  density = 1
  expand = 3
  formula = Ag
  name = G4_Ag
  specific = 4
FEATURE [App::DocumentObjectGroupPython] Cd_element003  label="Cd_element : 003"  # scripted group (container) (typed FeaturePython)
  n = 1
  ref = Cd_element
FEATURE [App::DocumentObjectGroupPython] G4_Cd  # scripted group (container) (typed FeaturePython)
  Dunit = g/cm3
  Dvalue = 8.65
  Group = -> [Cd_element003]
  conduct = 2
  density = 1
  expand = 3
  formula = Cd
  name = G4_Cd
  specific = 4
FEATURE [App::DocumentObjectGroupPython] In_element001  label="In_element : 1"  # scripted group (container) (typed FeaturePython)
  n = 1
  ref = In_element
FEATURE [App::DocumentObjectGroupPython] G4_In  # scripted group (container) (typed FeaturePython)
  Dunit = g/cm3
  Dvalue = 7.31
  Group = -> [In_element001]
  conduct = 2
  density = 1
  expand = 3
  formula = In
  name = G4_In
  specific = 4
FEATURE [App::DocumentObjectGroupPython] Sn_element001  label="Sn_element : 1"  # scripted group (container) (typed FeaturePython)
  n = 1
  ref = Sn_element
FEATURE [App::DocumentObjectGroupPython] G4_Sn  # scripted group (container) (typed FeaturePython)
  Dunit = g/cm3
  Dvalue = 7.31
  Group = -> [Sn_element001]
  conduct = 2
  density = 1
  expand = 3
  formula = Sn
  name = G4_Sn
  specific = 4
FEATURE [App::DocumentObjectGroupPython] Sb_element001  label="Sb_element : 1"  # scripted group (container) (typed FeaturePython)
  n = 1
  ref = Sb_element
FEATURE [App::DocumentObjectGroupPython] G4_Sb  # scripted group (container) (typed FeaturePython)
  Dunit = g/cm3
  Dvalue = 6.691
  Group = -> [Sb_element001]
  conduct = 2
  density = 1
  expand = 3
  formula = Sb
  name = G4_Sb
  specific = 4
FEATURE [App::DocumentObjectGroupPython] Te_element002  label="Te_element : 002"  # scripted group (container) (typed FeaturePython)
  n = 1
  ref = Te_element
FEATURE [App::DocumentObjectGroupPython] G4_Te  # scripted group (container) (typed FeaturePython)
  Dunit = g/cm3
  Dvalue = 6.24
  Group = -> [Te_element002]
  conduct = 2
  density = 1
  expand = 3
  formula = Te
  name = G4_Te
  specific = 4
FEATURE [App::DocumentObjectGroupPython] I_element010  label="I_element : 006"  # scripted group (container) (typed FeaturePython)
  n = 1
  ref = I_element
FEATURE [App::DocumentObjectGroupPython] G4_I  # scripted group (container) (typed FeaturePython)
  Dunit = g/cm3
  Dvalue = 4.93
  Group = -> [I_element010]
  conduct = 2
  density = 1
  expand = 3
  formula = I
  name = G4_I
  specific = 4
FEATURE [App::DocumentObjectGroupPython] Xe_element001  label="Xe_element : 1"  # scripted group (container) (typed FeaturePython)
  n = 1
  ref = Xe_element
FEATURE [App::DocumentObjectGroupPython] G4_Xe  # scripted group (container) (typed FeaturePython)
  Dunit = g/cm3
  Dvalue = 0.00548536
  Group = -> [Xe_element001]
  conduct = 2
  density = 1
  expand = 3
  formula = Xe
  name = G4_Xe
  specific = 4
FEATURE [App::DocumentObjectGroupPython] Cs_element003  label="Cs_element : 003"  # scripted group (container) (typed FeaturePython)
  n = 1
  ref = Cs_element
FEATURE [App::DocumentObjectGroupPython] G4_Cs  # scripted group (container) (typed FeaturePython)
  Dunit = g/cm3
  Dvalue = 1.873
  Group = -> [Cs_element003]
  conduct = 2
  density = 1
  expand = 3
  formula = Cs
  name = G4_Cs
  specific = 4
FEATURE [App::DocumentObjectGroupPython] Ba_element003  label="Ba_element : 003"  # scripted group (container) (typed FeaturePython)
  n = 1
  ref = Ba_element
FEATURE [App::DocumentObjectGroupPython] G4_Ba  # scripted group (container) (typed FeaturePython)
  Dunit = g/cm3
  Dvalue = 3.5
  Group = -> [Ba_element003]
  conduct = 2
  density = 1
  expand = 3
  formula = Ba
  name = G4_Ba
  specific = 4
FEATURE [App::DocumentObjectGroupPython] La_element003  label="La_element : 003"  # scripted group (container) (typed FeaturePython)
  n = 1
  ref = La_element
FEATURE [App::DocumentObjectGroupPython] G4_La  # scripted group (container) (typed FeaturePython)
  Dunit = g/cm3
  Dvalue = 6.154
  Group = -> [La_element003]
  conduct = 2
  density = 1
  expand = 3
  formula = La
  name = G4_La
  specific = 4
FEATURE [App::DocumentObjectGroupPython] Ce_element002  label="Ce_element : 1"  # scripted group (container) (typed FeaturePython)
  n = 1
  ref = Ce_element
FEATURE [App::DocumentObjectGroupPython] G4_Ce  # scripted group (container) (typed FeaturePython)
  Dunit = g/cm3
  Dvalue = 6.657
  Group = -> [Ce_element002]
  conduct = 2
  density = 1
  expand = 3
  formula = Ce
  name = G4_Ce
  specific = 4
FEATURE [App::DocumentObjectGroupPython] Pr_element001  label="Pr_element : 1"  # scripted group (container) (typed FeaturePython)
  n = 1
  ref = Pr_element
FEATURE [App::DocumentObjectGroupPython] G4_Pr  # scripted group (container) (typed FeaturePython)
  Dunit = g/cm3
  Dvalue = 6.71
  Group = -> [Pr_element001]
  conduct = 2
  density = 1
  expand = 3
  formula = Pr
  name = G4_Pr
  specific = 4
FEATURE [App::DocumentObjectGroupPython] Nd_element001  label="Nd_element : 1"  # scripted group (container) (typed FeaturePython)
  n = 1
  ref = Nd_element
FEATURE [App::DocumentObjectGroupPython] G4_Nd  # scripted group (container) (typed FeaturePython)
  Dunit = g/cm3
  Dvalue = 6.9
  Group = -> [Nd_element001]
  conduct = 2
  density = 1
  expand = 3
  formula = Nd
  name = G4_Nd
  specific = 4
FEATURE [App::DocumentObjectGroupPython] Pm_element001  label="Pm_element : 1"  # scripted group (container) (typed FeaturePython)
  n = 1
  ref = Pm_element
FEATURE [App::DocumentObjectGroupPython] G4_Pm  # scripted group (container) (typed FeaturePython)
  Dunit = g/cm3
  Dvalue = 7.22
  Group = -> [Pm_element001]
  conduct = 2
  density = 1
  expand = 3
  formula = Pm
  name = G4_Pm
  specific = 4
FEATURE [App::DocumentObjectGroupPython] Sm_element001  label="Sm_element : 1"  # scripted group (container) (typed FeaturePython)
  n = 1
  ref = Sm_element
FEATURE [App::DocumentObjectGroupPython] G4_Sm  # scripted group (container) (typed FeaturePython)
  Dunit = g/cm3
  Dvalue = 7.46
  Group = -> [Sm_element001]
  conduct = 2
  density = 1
  expand = 3
  formula = Sm
  name = G4_Sm
  specific = 4
FEATURE [App::DocumentObjectGroupPython] Eu_element001  label="Eu_element : 1"  # scripted group (container) (typed FeaturePython)
  n = 1
  ref = Eu_element
FEATURE [App::DocumentObjectGroupPython] G4_Eu  # scripted group (container) (typed FeaturePython)
  Dunit = g/cm3
  Dvalue = 5.243
  Group = -> [Eu_element001]
  conduct = 2
  density = 1
  expand = 3
  formula = Eu
  name = G4_Eu
  specific = 4
FEATURE [App::DocumentObjectGroupPython] Gd_element002  label="Gd_element : 1"  # scripted group (container) (typed FeaturePython)
  n = 1
  ref = Gd_element
FEATURE [App::DocumentObjectGroupPython] G4_Gd  # scripted group (container) (typed FeaturePython)
  Dunit = g/cm3
  Dvalue = 7.9004
  Group = -> [Gd_element002]
  conduct = 2
  density = 1
  expand = 3
  formula = Gd
  name = G4_Gd
  specific = 4
FEATURE [App::DocumentObjectGroupPython] Tb_element001  label="Tb_element : 1"  # scripted group (container) (typed FeaturePython)
  n = 1
  ref = Tb_element
FEATURE [App::DocumentObjectGroupPython] G4_Tb  # scripted group (container) (typed FeaturePython)
  Dunit = g/cm3
  Dvalue = 8.229
  Group = -> [Tb_element001]
  conduct = 2
  density = 1
  expand = 3
  formula = Tb
  name = G4_Tb
  specific = 4
FEATURE [App::DocumentObjectGroupPython] Dy_element001  label="Dy_element : 1"  # scripted group (container) (typed FeaturePython)
  n = 1
  ref = Dy_element
FEATURE [App::DocumentObjectGroupPython] G4_Dy  # scripted group (container) (typed FeaturePython)
  Dunit = g/cm3
  Dvalue = 8.55
  Group = -> [Dy_element001]
  conduct = 2
  density = 1
  expand = 3
  formula = Dy
  name = G4_Dy
  specific = 4
FEATURE [App::DocumentObjectGroupPython] Ho_element001  label="Ho_element : 1"  # scripted group (container) (typed FeaturePython)
  n = 1
  ref = Ho_element
FEATURE [App::DocumentObjectGroupPython] G4_Ho  # scripted group (container) (typed FeaturePython)
  Dunit = g/cm3
  Dvalue = 8.795
  Group = -> [Ho_element001]
  conduct = 2
  density = 1
  expand = 3
  formula = Ho
  name = G4_Ho
  specific = 4
FEATURE [App::DocumentObjectGroupPython] Er_element001  label="Er_element : 1"  # scripted group (container) (typed FeaturePython)
  n = 1
  ref = Er_element
FEATURE [App::DocumentObjectGroupPython] G4_Er  # scripted group (container) (typed FeaturePython)
  Dunit = g/cm3
  Dvalue = 9.066
  Group = -> [Er_element001]
  conduct = 2
  density = 1
  expand = 3
  formula = Er
  name = G4_Er
  specific = 4
FEATURE [App::DocumentObjectGroupPython] Tm_element001  label="Tm_element : 1"  # scripted group (container) (typed FeaturePython)
  n = 1
  ref = Tm_element
FEATURE [App::DocumentObjectGroupPython] G4_Tm  # scripted group (container) (typed FeaturePython)
  Dunit = g/cm3
  Dvalue = 9.321
  Group = -> [Tm_element001]
  conduct = 2
  density = 1
  expand = 3
  formula = Tm
  name = G4_Tm
  specific = 4
FEATURE [App::DocumentObjectGroupPython] Yb_element001  label="Yb_element : 1"  # scripted group (container) (typed FeaturePython)
  n = 1
  ref = Yb_element
FEATURE [App::DocumentObjectGroupPython] G4_Yb  # scripted group (container) (typed FeaturePython)
  Dunit = g/cm3
  Dvalue = 6.73
  Group = -> [Yb_element001]
  conduct = 2
  density = 1
  expand = 3
  formula = Yb
  name = G4_Yb
  specific = 4
FEATURE [App::DocumentObjectGroupPython] Lu_element001  label="Lu_element : 1"  # scripted group (container) (typed FeaturePython)
  n = 1
  ref = Lu_element
FEATURE [App::DocumentObjectGroupPython] G4_Lu  # scripted group (container) (typed FeaturePython)
  Dunit = g/cm3
  Dvalue = 9.84
  Group = -> [Lu_element001]
  conduct = 2
  density = 1
  expand = 3
  formula = Lu
  name = G4_Lu
  specific = 4
FEATURE [App::DocumentObjectGroupPython] Hf_element001  label="Hf_element : 1"  # scripted group (container) (typed FeaturePython)
  n = 1
  ref = Hf_element
FEATURE [App::DocumentObjectGroupPython] G4_Hf  # scripted group (container) (typed FeaturePython)
  Dunit = g/cm3
  Dvalue = 13.31
  Group = -> [Hf_element001]
  conduct = 2
  density = 1
  expand = 3
  formula = Hf
  name = G4_Hf
  specific = 4
FEATURE [App::DocumentObjectGroupPython] Ta_element001  label="Ta_element : 1"  # scripted group (container) (typed FeaturePython)
  n = 1
  ref = Ta_element
FEATURE [App::DocumentObjectGroupPython] G4_Ta  # scripted group (container) (typed FeaturePython)
  Dunit = g/cm3
  Dvalue = 16.654
  Group = -> [Ta_element001]
  conduct = 2
  density = 1
  expand = 3
  formula = Ta
  name = G4_Ta
  specific = 4
FEATURE [App::DocumentObjectGroupPython] W_element004  label="W_element : 004"  # scripted group (container) (typed FeaturePython)
  n = 1
  ref = W_element
FEATURE [App::DocumentObjectGroupPython] G4_W  # scripted group (container) (typed FeaturePython)
  Dunit = g/cm3
  Dvalue = 19.3
  Group = -> [W_element004]
  conduct = 2
  density = 1
  expand = 3
  formula = W
  name = G4_W
  specific = 4
FEATURE [App::DocumentObjectGroupPython] Re_element001  label="Re_element : 1"  # scripted group (container) (typed FeaturePython)
  n = 1
  ref = Re_element
FEATURE [App::DocumentObjectGroupPython] G4_Re  # scripted group (container) (typed FeaturePython)
  Dunit = g/cm3
  Dvalue = 21.02
  Group = -> [Re_element001]
  conduct = 2
  density = 1
  expand = 3
  formula = Re
  name = G4_Re
  specific = 4
FEATURE [App::DocumentObjectGroupPython] Os_element001  label="Os_element : 1"  # scripted group (container) (typed FeaturePython)
  n = 1
  ref = Os_element
FEATURE [App::DocumentObjectGroupPython] G4_Os  # scripted group (container) (typed FeaturePython)
  Dunit = g/cm3
  Dvalue = 22.57
  Group = -> [Os_element001]
  conduct = 2
  density = 1
  expand = 3
  formula = Os
  name = G4_Os
  specific = 4
FEATURE [App::DocumentObjectGroupPython] Ir_element001  label="Ir_element : 1"  # scripted group (container) (typed FeaturePython)
  n = 1
  ref = Ir_element
FEATURE [App::DocumentObjectGroupPython] G4_Ir  # scripted group (container) (typed FeaturePython)
  Dunit = g/cm3
  Dvalue = 22.42
  Group = -> [Ir_element001]
  conduct = 2
  density = 1
  expand = 3
  formula = Ir
  name = G4_Ir
  specific = 4
FEATURE [App::DocumentObjectGroupPython] Pt_element001  label="Pt_element : 1"  # scripted group (container) (typed FeaturePython)
  n = 1
  ref = Pt_element
FEATURE [App::DocumentObjectGroupPython] G4_Pt  # scripted group (container) (typed FeaturePython)
  Dunit = g/cm3
  Dvalue = 21.45
  Group = -> [Pt_element001]
  conduct = 2
  density = 1
  expand = 3
  formula = Pt
  name = G4_Pt
  specific = 4
FEATURE [App::DocumentObjectGroupPython] Au_element001  label="Au_element : 1"  # scripted group (container) (typed FeaturePython)
  n = 1
  ref = Au_element
FEATURE [App::DocumentObjectGroupPython] G4_Au  # scripted group (container) (typed FeaturePython)
  Dunit = g/cm3
  Dvalue = 19.32
  Group = -> [Au_element001]
  conduct = 2
  density = 1
  expand = 3
  formula = Au
  name = G4_Au
  specific = 4
FEATURE [App::DocumentObjectGroupPython] Hg_element002  label="Hg_element : 002"  # scripted group (container) (typed FeaturePython)
  n = 1
  ref = Hg_element
FEATURE [App::DocumentObjectGroupPython] G4_Hg  # scripted group (container) (typed FeaturePython)
  Dunit = g/cm3
  Dvalue = 13.546
  Group = -> [Hg_element002]
  conduct = 2
  density = 1
  expand = 3
  formula = Hg
  name = G4_Hg
  specific = 4
FEATURE [App::DocumentObjectGroupPython] Tl_element002  label="Tl_element : 002"  # scripted group (container) (typed FeaturePython)
  n = 1
  ref = Tl_element
FEATURE [App::DocumentObjectGroupPython] G4_Tl  # scripted group (container) (typed FeaturePython)
  Dunit = g/cm3
  Dvalue = 11.72
  Group = -> [Tl_element002]
  conduct = 2
  density = 1
  expand = 3
  formula = Tl
  name = G4_Tl
  specific = 4
FEATURE [App::DocumentObjectGroupPython] Pb_element003  label="Pb_element : 1"  # scripted group (container) (typed FeaturePython)
  n = 1
  ref = Pb_element
FEATURE [App::DocumentObjectGroupPython] G4_Pb  # scripted group (container) (typed FeaturePython)
  Dunit = g/cm3
  Dvalue = 11.35
  Group = -> [Pb_element003]
  conduct = 2
  density = 1
  expand = 3
  formula = Pb
  name = G4_Pb
  specific = 4
FEATURE [App::DocumentObjectGroupPython] Bi_element002  label="Bi_element : 1"  # scripted group (container) (typed FeaturePython)
  n = 1
  ref = Bi_element
FEATURE [App::DocumentObjectGroupPython] G4_Bi  # scripted group (container) (typed FeaturePython)
  Dunit = g/cm3
  Dvalue = 9.747
  Group = -> [Bi_element002]
  conduct = 2
  density = 1
  expand = 3
  formula = Bi
  name = G4_Bi
  specific = 4
FEATURE [App::DocumentObjectGroupPython] Po_element001  label="Po_element : 1"  # scripted group (container) (typed FeaturePython)
  n = 1
  ref = Po_element
FEATURE [App::DocumentObjectGroupPython] G4_Po  # scripted group (container) (typed FeaturePython)
  Dunit = g/cm3
  Dvalue = 9.32
  Group = -> [Po_element001]
  conduct = 2
  density = 1
  expand = 3
  formula = Po
  name = G4_Po
  specific = 4
FEATURE [App::DocumentObjectGroupPython] At_element001  label="At_element : 1"  # scripted group (container) (typed FeaturePython)
  n = 1
  ref = At_element
FEATURE [App::DocumentObjectGroupPython] G4_At  # scripted group (container) (typed FeaturePython)
  Dunit = g/cm3
  Dvalue = 9.32
  Group = -> [At_element001]
  conduct = 2
  density = 1
  expand = 3
  formula = At
  name = G4_At
  specific = 4
FEATURE [App::DocumentObjectGroupPython] Rn_element001  label="Rn_element : 1"  # scripted group (container) (typed FeaturePython)
  n = 1
  ref = Rn_element
FEATURE [App::DocumentObjectGroupPython] G4_Rn  # scripted group (container) (typed FeaturePython)
  Dunit = g/cm3
  Dvalue = 0.00900662
  Group = -> [Rn_element001]
  conduct = 2
  density = 1
  expand = 3
  formula = Rn
  name = G4_Rn
  specific = 4
FEATURE [App::DocumentObjectGroupPython] Fr_element001  label="Fr_element : 1"  # scripted group (container) (typed FeaturePython)
  n = 1
  ref = Fr_element
FEATURE [App::DocumentObjectGroupPython] G4_Fr  # scripted group (container) (typed FeaturePython)
  Dunit = g/cm3
  Dvalue = 1
  Group = -> [Fr_element001]
  conduct = 2
  density = 1
  expand = 3
  formula = Fr
  name = G4_Fr
  specific = 4
FEATURE [App::DocumentObjectGroupPython] Ra_element001  label="Ra_element : 1"  # scripted group (container) (typed FeaturePython)
  n = 1
  ref = Ra_element
FEATURE [App::DocumentObjectGroupPython] G4_Ra  # scripted group (container) (typed FeaturePython)
  Dunit = g/cm3
  Dvalue = 5
  Group = -> [Ra_element001]
  conduct = 2
  density = 1
  expand = 3
  formula = Ra
  name = G4_Ra
  specific = 4
FEATURE [App::DocumentObjectGroupPython] Ac_element001  label="Ac_element : 1"  # scripted group (container) (typed FeaturePython)
  n = 1
  ref = Ac_element
FEATURE [App::DocumentObjectGroupPython] G4_Ac  # scripted group (container) (typed FeaturePython)
  Dunit = g/cm3
  Dvalue = 10.07
  Group = -> [Ac_element001]
  conduct = 2
  density = 1
  expand = 3
  formula = Ac
  name = G4_Ac
  specific = 4
FEATURE [App::DocumentObjectGroupPython] Th_element001  label="Th_element : 1"  # scripted group (container) (typed FeaturePython)
  n = 1
  ref = Th_element
FEATURE [App::DocumentObjectGroupPython] G4_Th  # scripted group (container) (typed FeaturePython)
  Dunit = g/cm3
  Dvalue = 11.72
  Group = -> [Th_element001]
  conduct = 2
  density = 1
  expand = 3
  formula = Th
  name = G4_Th
  specific = 4
FEATURE [App::DocumentObjectGroupPython] Pa_element001  label="Pa_element : 1"  # scripted group (container) (typed FeaturePython)
  n = 1
  ref = Pa_element
FEATURE [App::DocumentObjectGroupPython] G4_Pa  # scripted group (container) (typed FeaturePython)
  Dunit = g/cm3
  Dvalue = 15.37
  Group = -> [Pa_element001]
  conduct = 2
  density = 1
  expand = 3
  formula = Pa
  name = G4_Pa
  specific = 4
FEATURE [App::DocumentObjectGroupPython] U_element004  label="U_element : 004"  # scripted group (container) (typed FeaturePython)
  n = 1
  ref = U_element
FEATURE [App::DocumentObjectGroupPython] G4_U  # scripted group (container) (typed FeaturePython)
  Dunit = g/cm3
  Dvalue = 18.95
  Group = -> [U_element004]
  conduct = 2
  density = 1
  expand = 3
  formula = U
  name = G4_U
  specific = 4
FEATURE [App::DocumentObjectGroupPython] Np_element001  label="Np_element : 1"  # scripted group (container) (typed FeaturePython)
  n = 1
  ref = Np_element
FEATURE [App::DocumentObjectGroupPython] G4_Np  # scripted group (container) (typed FeaturePython)
  Dunit = g/cm3
  Dvalue = 20.25
  Group = -> [Np_element001]
  conduct = 2
  density = 1
  expand = 3
  formula = Np
  name = G4_Np
  specific = 4
FEATURE [App::DocumentObjectGroupPython] Pu_element002  label="Pu_element : 002"  # scripted group (container) (typed FeaturePython)
  n = 1
  ref = Pu_element
FEATURE [App::DocumentObjectGroupPython] G4_Pu  # scripted group (container) (typed FeaturePython)
  Dunit = g/cm3
  Dvalue = 19.84
  Group = -> [Pu_element002]
  conduct = 2
  density = 1
  expand = 3
  formula = Pu
  name = G4_Pu
  specific = 4
FEATURE [App::DocumentObjectGroupPython] Am_element001  label="Am_element : 1"  # scripted group (container) (typed FeaturePython)
  n = 1
  ref = Am_element
FEATURE [App::DocumentObjectGroupPython] G4_Am  # scripted group (container) (typed FeaturePython)
  Dunit = g/cm3
  Dvalue = 13.67
  Group = -> [Am_element001]
  conduct = 2
  density = 1
  expand = 3
  formula = Am
  name = G4_Am
  specific = 4
FEATURE [App::DocumentObjectGroupPython] Cm_element001  label="Cm_element : 1"  # scripted group (container) (typed FeaturePython)
  n = 1
  ref = Cm_element
FEATURE [App::DocumentObjectGroupPython] G4_Cm  # scripted group (container) (typed FeaturePython)
  Dunit = g/cm3
  Dvalue = 13.51
  Group = -> [Cm_element001]
  conduct = 2
  density = 1
  expand = 3
  formula = Cm
  name = G4_Cm
  specific = 4
FEATURE [App::DocumentObjectGroupPython] Bk_element001  label="Bk_element : 1"  # scripted group (container) (typed FeaturePython)
  n = 1
  ref = Bk_element
FEATURE [App::DocumentObjectGroupPython] G4_Bk  # scripted group (container) (typed FeaturePython)
  Dunit = g/cm3
  Dvalue = 14
  Group = -> [Bk_element001]
  conduct = 2
  density = 1
  expand = 3
  formula = Bk
  name = G4_Bk
  specific = 4
FEATURE [App::DocumentObjectGroupPython] Cf_element001  label="Cf_element : 1"  # scripted group (container) (typed FeaturePython)
  n = 1
  ref = Cf_element
FEATURE [App::DocumentObjectGroupPython] G4_Cf  # scripted group (container) (typed FeaturePython)
  Dunit = g/cm3
  Dvalue = 10
  Group = -> [Cf_element001]
  conduct = 2
  density = 1
  expand = 3
  formula = Cf
  name = G4_Cf
  specific = 4
FEATURE [App::DocumentObjectGroupPython] Element  # scripted group (container) (typed FeaturePython)
  Group = -> [G4_H,G4_He,G4_Li,G4_Be,G4_B,G4_C,G4_N,G4_O,G4_F,G4_Ne,G4_Na,G4_Mg,G4_Al,G4_Si,G4_P,G4_S,G4_Cl,G4_Ar,G4_K,G4_Ca,G4_Sc,G4_Ti,G4_V,G4_Cr,G4_Mn,G4_Fe,G4_Co,G4_Ni,G4_Cu,G4_Zn,G4_Ga,G4_Ge,G4_As,G4_Se,G4_Br,G4_Kr,G4_Rb,G4_Sr,G4_Y,G4_Zr,G4_Nb,G4_Mo,G4_Tc,G4_Ru,G4_Rh,G4_Pd,G4_Ag,G4_Cd,G4_In,G4_Sn,G4_Sb,G4_Te,G4_I,G4_Xe,G4_Cs,G4_Ba,G4_La,G4_Ce,G4_Pr,G4_Nd,G4_Pm,G4_Sm,G4_Eu,G4_Gd,G4_Tb,G4_Dy,G4_Ho,G4_Er,+30 more]
FEATURE [App::DocumentObjectGroupPython] H_element114  label="H_element : 063"  # scripted group (container) (typed FeaturePython)
  n = 2
  ref = H_element
FEATURE [App::DocumentObjectGroupPython] G4_lH2  # scripted group (container) (typed FeaturePython)
  Dunit = g/cm3
  Dvalue = 0.0708
  Group = -> [H_element114]
  conduct = 2
  density = 1
  expand = 3
  formula = G4_lH2
  name = G4_lH2
  specific = 4
FEATURE [App::DocumentObjectGroupPython] N_element049  label="N_element : 022"  # scripted group (container) (typed FeaturePython)
  n = 2
  ref = N_element
FEATURE [App::DocumentObjectGroupPython] G4_lN2  # scripted group (container) (typed FeaturePython)
  Dunit = g/cm3
  Dvalue = 0.807
  Group = -> [N_element049]
  conduct = 2
  density = 1
  expand = 3
  formula = G4_lN2
  name = G4_lN2
  specific = 4
FEATURE [App::DocumentObjectGroupPython] O_element106  label="O_element : 060"  # scripted group (container) (typed FeaturePython)
  n = 2
  ref = O_element
FEATURE [App::DocumentObjectGroupPython] G4_lO2  # scripted group (container) (typed FeaturePython)
  Dunit = g/cm3
  Dvalue = 1.141
  Group = -> [O_element106]
  conduct = 2
  density = 1
  expand = 3
  formula = G4_lO2
  name = G4_lO2
  specific = 4
FEATURE [App::DocumentObjectGroupPython] Ar  label="Ar : 1"  # scripted group (container) (typed FeaturePython)
  n = 1
  ref = Ar
FEATURE [App::DocumentObjectGroupPython] G4_lAr  # scripted group (container) (typed FeaturePython)
  Dunit = g/cm3
  Dvalue = 1.396
  Group = -> [Ar]
  conduct = 2
  density = 1
  expand = 3
  formula = G4_lAr
  name = G4_lAr
  specific = 4
FEATURE [App::DocumentObjectGroupPython] Br  label="Br : 1"  # scripted group (container) (typed FeaturePython)
  n = 1
  ref = Br
FEATURE [App::DocumentObjectGroupPython] G4_lBr  # scripted group (container) (typed FeaturePython)
  Dunit = g/cm3
  Dvalue = 3.1028
  Group = -> [Br]
  conduct = 2
  density = 1
  expand = 3
  formula = G4_lBr
  name = G4_lBr
  specific = 4
FEATURE [App::DocumentObjectGroupPython] Kr  label="Kr : 1"  # scripted group (container) (typed FeaturePython)
  n = 1
  ref = Kr
FEATURE [App::DocumentObjectGroupPython] G4_lKr  # scripted group (container) (typed FeaturePython)
  Dunit = g/cm3
  Dvalue = 2.418
  Group = -> [Kr]
  conduct = 2
  density = 1
  expand = 3
  formula = G4_lKr
  name = G4_lKr
  specific = 4
FEATURE [App::DocumentObjectGroupPython] Xe  label="Xe : 1"  # scripted group (container) (typed FeaturePython)
  n = 1
  ref = Xe
FEATURE [App::DocumentObjectGroupPython] G4_lXe  # scripted group (container) (typed FeaturePython)
  Dunit = g/cm3
  Dvalue = 2.953
  Group = -> [Xe]
  conduct = 2
  density = 1
  expand = 3
  formula = G4_lXe
  name = G4_lXe
  specific = 4
FEATURE [App::DocumentObjectGroupPython] O_element107  label="O_element : 061"  # scripted group (container) (typed FeaturePython)
  n = 4
  ref = O_element
FEATURE [App::DocumentObjectGroupPython] Pb_element004  label="Pb_element : 002"  # scripted group (container) (typed FeaturePython)
  n = 1
  ref = Pb_element
FEATURE [App::DocumentObjectGroupPython] W_element005  label="W_element : 005"  # scripted group (container) (typed FeaturePython)
  n = 1
  ref = W_element
FEATURE [App::DocumentObjectGroupPython] G4_PbWO4  # scripted group (container) (typed FeaturePython)
  Dunit = g/cm3
  Dvalue = 8.28
  Group = -> [O_element107,Pb_element004,W_element005]
  conduct = 2
  density = 1
  expand = 3
  formula = G4_PbWO4
  name = G4_PbWO4
  specific = 4
FEATURE [App::DocumentObjectGroupPython] alactic  label="alactic : 1"  # scripted group (container) (typed FeaturePython)
  n = 1
  ref = alactic
FEATURE [App::DocumentObjectGroupPython] G4_Galactic  # scripted group (container) (typed FeaturePython)
  Dunit = g/cm3
  Dvalue = 0
  Group = -> [alactic]
  conduct = 2
  density = 1
  expand = 3
  formula = G4_Galactic
  name = G4_Galactic
  specific = 4
FEATURE [App::DocumentObjectGroupPython] RAPHITE_POROUS  label="RAPHITE_POROUS : 1"  # scripted group (container) (typed FeaturePython)
  n = 1
  ref = RAPHITE_POROUS
FEATURE [App::DocumentObjectGroupPython] G4_GRAPHITE_POROUS  # scripted group (container) (typed FeaturePython)
  Dunit = g/cm3
  Dvalue = 1.7
  Group = -> [RAPHITE_POROUS]
  conduct = 2
  density = 1
  expand = 3
  formula = G4_GRAPHITE_POROUS
  name = G4_GRAPHITE_POROUS
  specific = 4
FEATURE [App::DocumentObjectGroupPython] H_element115  label="H_element : 0.150"  # scripted group (container) (typed FeaturePython)
  n = 0.080538
FEATURE [App::DocumentObjectGroupPython] C_element125  label="C_element : 0.600"  # scripted group (container) (typed FeaturePython)
  n = 0.599848
FEATURE [App::DocumentObjectGroupPython] O_element108  label="O_element : 0.320"  # scripted group (container) (typed FeaturePython)
  n = 0.319614
FEATURE [App::DocumentObjectGroupPython] G4_LUCITE  # scripted group (container) (typed FeaturePython)
  Dunit = g/cm3
  Dvalue = 1.19
  Group = -> [H_element115,C_element125,O_element108]
  conduct = 2
  density = 1
  expand = 3
  formula = G4_LUCITE
  name = G4_LUCITE
  specific = 4
FEATURE [App::DocumentObjectGroupPython] Cu_element002  label="Cu_element : 62"  # scripted group (container) (typed FeaturePython)
  n = 62
  ref = Cu_element
FEATURE [App::DocumentObjectGroupPython] Zn_element002  label="Zn_element : 35"  # scripted group (container) (typed FeaturePython)
  n = 35
  ref = Zn_element
FEATURE [App::DocumentObjectGroupPython] Pb_element005  label="Pb_element : 3"  # scripted group (container) (typed FeaturePython)
  n = 3
  ref = Pb_element
FEATURE [App::DocumentObjectGroupPython] G4_BRASS  # scripted group (container) (typed FeaturePython)
  Dunit = g/cm3
  Dvalue = 8.52
  Group = -> [Cu_element002,Zn_element002,Pb_element005]
  conduct = 2
  density = 1
  expand = 3
  formula = G4_BRASS
  name = G4_BRASS
  specific = 4
FEATURE [App::DocumentObjectGroupPython] Cu_element003  label="Cu_element : 89"  # scripted group (container) (typed FeaturePython)
  n = 89
  ref = Cu_element
FEATURE [App::DocumentObjectGroupPython] Zn_element003  label="Zn_element : 9"  # scripted group (container) (typed FeaturePython)
  n = 9
  ref = Zn_element
FEATURE [App::DocumentObjectGroupPython] Pb_element006  label="Pb_element : 2"  # scripted group (container) (typed FeaturePython)
  n = 2
  ref = Pb_element
FEATURE [App::DocumentObjectGroupPython] G4_BRONZE  # scripted group (container) (typed FeaturePython)
  Dunit = g/cm3
  Dvalue = 8.82
  Group = -> [Cu_element003,Zn_element003,Pb_element006]
  conduct = 2
  density = 1
  expand = 3
  formula = G4_BRONZE
  name = G4_BRONZE
  specific = 4
FEATURE [App::DocumentObjectGroupPython] Fe_element008  label="Fe_element : 74"  # scripted group (container) (typed FeaturePython)
  n = 74
  ref = Fe_element
FEATURE [App::DocumentObjectGroupPython] Cr_element002  label="Cr_element : 18"  # scripted group (container) (typed FeaturePython)
  n = 18
  ref = Cr_element
FEATURE [App::DocumentObjectGroupPython] Ni_element002  label="Ni_element : 8"  # scripted group (container) (typed FeaturePython)
  n = 8
  ref = Ni_element
FEATURE [App::DocumentObjectGroupPython] G4_STAINLESS_STEEL  label="G4_STAINLESS-STEEL"  # scripted group (container) (typed FeaturePython)
  Dunit = g/cm3
  Dvalue = 8
  Group = -> [Fe_element008,Cr_element002,Ni_element002]
  conduct = 2
  density = 1
  expand = 3
  formula = G4_STAINLESS-STEEL
  name = G4_STAINLESS-STEEL
  specific = 4
FEATURE [App::DocumentObjectGroupPython] H_element116  label="H_element : 064"  # scripted group (container) (typed FeaturePython)
  n = 18
  ref = H_element
FEATURE [App::DocumentObjectGroupPython] C_element126  label="C_element : 071"  # scripted group (container) (typed FeaturePython)
  n = 12
  ref = C_element
FEATURE [App::DocumentObjectGroupPython] O_element109  label="O_element : 062"  # scripted group (container) (typed FeaturePython)
  n = 7
  ref = O_element
FEATURE [App::DocumentObjectGroupPython] G4_CR39  # scripted group (container) (typed FeaturePython)
  Dunit = g/cm3
  Dvalue = 1.32
  Group = -> [H_element116,C_element126,O_element109]
  conduct = 2
  density = 1
  expand = 3
  formula = G4_CR39
  name = G4_CR39
  specific = 4
FEATURE [App::DocumentObjectGroupPython] H_element117  label="H_element : 38"  # scripted group (container) (typed FeaturePython)
  n = 38
  ref = H_element
FEATURE [App::DocumentObjectGroupPython] C_element127  label="C_element : 072"  # scripted group (container) (typed FeaturePython)
  n = 18
  ref = C_element
FEATURE [App::DocumentObjectGroupPython] O_element110  label="O_element : 063"  # scripted group (container) (typed FeaturePython)
  n = 1
  ref = O_element
FEATURE [App::DocumentObjectGroupPython] G4_OCTADECANOL  # scripted group (container) (typed FeaturePython)
  Dunit = g/cm3
  Dvalue = 0.812
  Group = -> [H_element117,C_element127,O_element110]
  conduct = 2
  density = 1
  expand = 3
  formula = G4_OCTADECANOL
  name = G4_OCTADECANOL
  specific = 4
FEATURE [App::DocumentObjectGroupPython] HEP  # scripted group (container) (typed FeaturePython)
  Group = -> [G4_lH2,G4_lN2,G4_lO2,G4_lAr,G4_lBr,G4_lKr,G4_lXe,G4_PbWO4,G4_Galactic,G4_GRAPHITE_POROUS,G4_LUCITE,G4_BRASS,G4_BRONZE,G4_STAINLESS_STEEL,G4_CR39,G4_OCTADECANOL]
FEATURE [App::DocumentObjectGroupPython] C_element128  label="C_element : 073"  # scripted group (container) (typed FeaturePython)
  n = 14
  ref = C_element
FEATURE [App::DocumentObjectGroupPython] H_element118  label="H_element : 065"  # scripted group (container) (typed FeaturePython)
  n = 10
  ref = H_element
FEATURE [App::DocumentObjectGroupPython] O_element111  label="O_element : 064"  # scripted group (container) (typed FeaturePython)
  n = 2
  ref = O_element
FEATURE [App::DocumentObjectGroupPython] N_element050  label="N_element : 023"  # scripted group (container) (typed FeaturePython)
  n = 2
  ref = N_element
FEATURE [App::DocumentObjectGroupPython] G4_KEVLAR  # scripted group (container) (typed FeaturePython)
  Dunit = g/cm3
  Dvalue = 1.44
  Group = -> [C_element128,H_element118,O_element111,N_element050]
  conduct = 2
  density = 1
  expand = 3
  formula = G4_KEVLAR
  name = G4_KEVLAR
  specific = 4
FEATURE [App::DocumentObjectGroupPython] C_element129  label="C_element : 074"  # scripted group (container) (typed FeaturePython)
  n = 10
  ref = C_element
FEATURE [App::DocumentObjectGroupPython] H_element119  label="H_element : 066"  # scripted group (container) (typed FeaturePython)
  n = 8
  ref = H_element
FEATURE [App::DocumentObjectGroupPython] O_element112  label="O_element : 065"  # scripted group (container) (typed FeaturePython)
  n = 4
  ref = O_element
FEATURE [App::DocumentObjectGroupPython] G4_DACRON  # scripted group (container) (typed FeaturePython)
  Dunit = g/cm3
  Dvalue = 1.4
  Group = -> [C_element129,H_element119,O_element112]
  conduct = 2
  density = 1
  expand = 3
  formula = G4_DACRON
  name = G4_DACRON
  specific = 4
FEATURE [App::DocumentObjectGroupPython] C_element130  label="C_element : 075"  # scripted group (container) (typed FeaturePython)
  n = 4
  ref = C_element
FEATURE [App::DocumentObjectGroupPython] H_element120  label="H_element : 067"  # scripted group (container) (typed FeaturePython)
  n = 5
  ref = H_element
FEATURE [App::DocumentObjectGroupPython] Cl_element030  label="Cl_element : 016"  # scripted group (container) (typed FeaturePython)
  n = 1
  ref = Cl_element
FEATURE [App::DocumentObjectGroupPython] G4_NEOPRENE  # scripted group (container) (typed FeaturePython)
  Dunit = g/cm3
  Dvalue = 1.23
  Group = -> [C_element130,H_element120,Cl_element030]
  conduct = 2
  density = 1
  expand = 3
  formula = G4_NEOPRENE
  name = G4_NEOPRENE
  specific = 4
FEATURE [App::DocumentObjectGroupPython] Space  # scripted group (container) (typed FeaturePython)
  Group = -> [G4_KEVLAR,G4_DACRON,G4_NEOPRENE]
FEATURE [App::DocumentObjectGroupPython] H_element121  label="H_element : 068"  # scripted group (container) (typed FeaturePython)
  n = 5
  ref = H_element
FEATURE [App::DocumentObjectGroupPython] C_element131  label="C_element : 076"  # scripted group (container) (typed FeaturePython)
  n = 4
  ref = C_element
FEATURE [App::DocumentObjectGroupPython] N_element051  label="N_element : 3"  # scripted group (container) (typed FeaturePython)
  n = 3
  ref = N_element
FEATURE [App::DocumentObjectGroupPython] O_element113  label="O_element : 066"  # scripted group (container) (typed FeaturePython)
  n = 1
  ref = O_element
FEATURE [App::DocumentObjectGroupPython] G4_CYTOSINE  # scripted group (container) (typed FeaturePython)
  Dunit = g/cm3
  Dvalue = 1.55
  Group = -> [H_element121,C_element131,N_element051,O_element113]
  conduct = 2
  density = 1
  expand = 3
  formula = G4_CYTOSINE
  name = G4_CYTOSINE
  specific = 4
FEATURE [App::DocumentObjectGroupPython] H_element122  label="H_element : 069"  # scripted group (container) (typed FeaturePython)
  n = 6
  ref = H_element
FEATURE [App::DocumentObjectGroupPython] C_element132  label="C_element : 077"  # scripted group (container) (typed FeaturePython)
  n = 5
  ref = C_element
FEATURE [App::DocumentObjectGroupPython] N_element052  label="N_element : 024"  # scripted group (container) (typed FeaturePython)
  n = 2
  ref = N_element
FEATURE [App::DocumentObjectGroupPython] O_element114  label="O_element : 067"  # scripted group (container) (typed FeaturePython)
  n = 2
  ref = O_element
FEATURE [App::DocumentObjectGroupPython] G4_THYMINE  # scripted group (container) (typed FeaturePython)
  Dunit = g/cm3
  Dvalue = 1.23
  Group = -> [H_element122,C_element132,N_element052,O_element114]
  conduct = 2
  density = 1
  expand = 3
  formula = G4_THYMINE
  name = G4_THYMINE
  specific = 4
FEATURE [App::DocumentObjectGroupPython] H_element123  label="H_element : 070"  # scripted group (container) (typed FeaturePython)
  n = 4
  ref = H_element
FEATURE [App::DocumentObjectGroupPython] C_element133  label="C_element : 078"  # scripted group (container) (typed FeaturePython)
  n = 4
  ref = C_element
FEATURE [App::DocumentObjectGroupPython] N_element053  label="N_element : 025"  # scripted group (container) (typed FeaturePython)
  n = 2
  ref = N_element
FEATURE [App::DocumentObjectGroupPython] O_element115  label="O_element : 068"  # scripted group (container) (typed FeaturePython)
  n = 2
  ref = O_element
FEATURE [App::DocumentObjectGroupPython] G4_URACIL  # scripted group (container) (typed FeaturePython)
  Dunit = g/cm3
  Dvalue = 1.32
  Group = -> [H_element123,C_element133,N_element053,O_element115]
  conduct = 2
  density = 1
  expand = 3
  formula = G4_URACIL
  name = G4_URACIL
  specific = 4
FEATURE [App::DocumentObjectGroupPython] H_element124  label="H_element : 071"  # scripted group (container) (typed FeaturePython)
  n = 4
  ref = H_element
FEATURE [App::DocumentObjectGroupPython] C_element134  label="C_element : 079"  # scripted group (container) (typed FeaturePython)
  n = 5
  ref = C_element
FEATURE [App::DocumentObjectGroupPython] N_element054  label="N_element : 026"  # scripted group (container) (typed FeaturePython)
  n = 5
  ref = N_element
FEATURE [App::DocumentObjectGroupPython] G4_DNA_ADENINE  # scripted group (container) (typed FeaturePython)
  Dunit = g/cm3
  Dvalue = 1
  Group = -> [H_element124,C_element134,N_element054]
  conduct = 2
  density = 1
  expand = 3
  formula = G4_DNA_ADENINE
  name = G4_DNA_ADENINE
  specific = 4
FEATURE [App::DocumentObjectGroupPython] H_element125  label="H_element : 072"  # scripted group (container) (typed FeaturePython)
  n = 4
  ref = H_element
FEATURE [App::DocumentObjectGroupPython] C_element135  label="C_element : 080"  # scripted group (container) (typed FeaturePython)
  n = 5
  ref = C_element
FEATURE [App::DocumentObjectGroupPython] N_element055  label="N_element : 027"  # scripted group (container) (typed FeaturePython)
  n = 5
  ref = N_element
FEATURE [App::DocumentObjectGroupPython] O_element116  label="O_element : 069"  # scripted group (container) (typed FeaturePython)
  n = 1
  ref = O_element
FEATURE [App::DocumentObjectGroupPython] G4_DNA_GUANINE  # scripted group (container) (typed FeaturePython)
  Dunit = g/cm3
  Dvalue = 1
  Group = -> [H_element125,C_element135,N_element055,O_element116]
  conduct = 2
  density = 1
  expand = 3
  formula = G4_DNA_GUANINE
  name = G4_DNA_GUANINE
  specific = 4
FEATURE [App::DocumentObjectGroupPython] H_element126  label="H_element : 073"  # scripted group (container) (typed FeaturePython)
  n = 4
  ref = H_element
FEATURE [App::DocumentObjectGroupPython] C_element136  label="C_element : 081"  # scripted group (container) (typed FeaturePython)
  n = 4
  ref = C_element
FEATURE [App::DocumentObjectGroupPython] N_element056  label="N_element : 028"  # scripted group (container) (typed FeaturePython)
  n = 3
  ref = N_element
FEATURE [App::DocumentObjectGroupPython] O_element117  label="O_element : 070"  # scripted group (container) (typed FeaturePython)
  n = 1
  ref = O_element
FEATURE [App::DocumentObjectGroupPython] G4_DNA_CYTOSINE  # scripted group (container) (typed FeaturePython)
  Dunit = g/cm3
  Dvalue = 1
  Group = -> [H_element126,C_element136,N_element056,O_element117]
  conduct = 2
  density = 1
  expand = 3
  formula = G4_DNA_CYTOSINE
  name = G4_DNA_CYTOSINE
  specific = 4
FEATURE [App::DocumentObjectGroupPython] H_element127  label="H_element : 074"  # scripted group (container) (typed FeaturePython)
  n = 5
  ref = H_element
FEATURE [App::DocumentObjectGroupPython] C_element137  label="C_element : 082"  # scripted group (container) (typed FeaturePython)
  n = 5
  ref = C_element
FEATURE [App::DocumentObjectGroupPython] N_element057  label="N_element : 029"  # scripted group (container) (typed FeaturePython)
  n = 2
  ref = N_element
FEATURE [App::DocumentObjectGroupPython] O_element118  label="O_element : 071"  # scripted group (container) (typed FeaturePython)
  n = 2
  ref = O_element
FEATURE [App::DocumentObjectGroupPython] G4_DNA_THYMINE  # scripted group (container) (typed FeaturePython)
  Dunit = g/cm3
  Dvalue = 1
  Group = -> [H_element127,C_element137,N_element057,O_element118]
  conduct = 2
  density = 1
  expand = 3
  formula = G4_DNA_THYMINE
  name = G4_DNA_THYMINE
  specific = 4
FEATURE [App::DocumentObjectGroupPython] H_element128  label="H_element : 075"  # scripted group (container) (typed FeaturePython)
  n = 3
  ref = H_element
FEATURE [App::DocumentObjectGroupPython] C_element138  label="C_element : 083"  # scripted group (container) (typed FeaturePython)
  n = 4
  ref = C_element
FEATURE [App::DocumentObjectGroupPython] N_element058  label="N_element : 030"  # scripted group (container) (typed FeaturePython)
  n = 2
  ref = N_element
FEATURE [App::DocumentObjectGroupPython] O_element119  label="O_element : 072"  # scripted group (container) (typed FeaturePython)
  n = 2
  ref = O_element
FEATURE [App::DocumentObjectGroupPython] G4_DNA_URACIL  # scripted group (container) (typed FeaturePython)
  Dunit = g/cm3
  Dvalue = 1
  Group = -> [H_element128,C_element138,N_element058,O_element119]
  conduct = 2
  density = 1
  expand = 3
  formula = G4_DNA_URACIL
  name = G4_DNA_URACIL
  specific = 4
FEATURE [App::DocumentObjectGroupPython] H_element129  label="H_element : 076"  # scripted group (container) (typed FeaturePython)
  n = 10
  ref = H_element
FEATURE [App::DocumentObjectGroupPython] C_element139  label="C_element : 084"  # scripted group (container) (typed FeaturePython)
  n = 10
  ref = C_element
FEATURE [App::DocumentObjectGroupPython] N_element059  label="N_element : 031"  # scripted group (container) (typed FeaturePython)
  n = 5
  ref = N_element
FEATURE [App::DocumentObjectGroupPython] O_element120  label="O_element : 073"  # scripted group (container) (typed FeaturePython)
  n = 4
  ref = O_element
FEATURE [App::DocumentObjectGroupPython] G4_DNA_ADENOSINE  # scripted group (container) (typed FeaturePython)
  Dunit = g/cm3
  Dvalue = 1
  Group = -> [H_element129,C_element139,N_element059,O_element120]
  conduct = 2
  density = 1
  expand = 3
  formula = G4_DNA_ADENOSINE
  name = G4_DNA_ADENOSINE
  specific = 4
FEATURE [App::DocumentObjectGroupPython] H_element130  label="H_element : 077"  # scripted group (container) (typed FeaturePython)
  n = 10
  ref = H_element
FEATURE [App::DocumentObjectGroupPython] C_element140  label="C_element : 085"  # scripted group (container) (typed FeaturePython)
  n = 10
  ref = C_element
FEATURE [App::DocumentObjectGroupPython] N_element060  label="N_element : 032"  # scripted group (container) (typed FeaturePython)
  n = 5
  ref = N_element
FEATURE [App::DocumentObjectGroupPython] O_element121  label="O_element : 074"  # scripted group (container) (typed FeaturePython)
  n = 5
  ref = O_element
FEATURE [App::DocumentObjectGroupPython] G4_DNA_GUANOSINE  # scripted group (container) (typed FeaturePython)
  Dunit = g/cm3
  Dvalue = 1
  Group = -> [H_element130,C_element140,N_element060,O_element121]
  conduct = 2
  density = 1
  expand = 3
  formula = G4_DNA_GUANOSINE
  name = G4_DNA_GUANOSINE
  specific = 4
FEATURE [App::DocumentObjectGroupPython] H_element131  label="H_element : 078"  # scripted group (container) (typed FeaturePython)
  n = 10
  ref = H_element
FEATURE [App::DocumentObjectGroupPython] C_element141  label="C_element : 086"  # scripted group (container) (typed FeaturePython)
  n = 9
  ref = C_element
FEATURE [App::DocumentObjectGroupPython] N_element061  label="N_element : 033"  # scripted group (container) (typed FeaturePython)
  n = 3
  ref = N_element
FEATURE [App::DocumentObjectGroupPython] O_element122  label="O_element : 075"  # scripted group (container) (typed FeaturePython)
  n = 5
  ref = O_element
FEATURE [App::DocumentObjectGroupPython] G4_DNA_CYTIDINE  # scripted group (container) (typed FeaturePython)
  Dunit = g/cm3
  Dvalue = 1
  Group = -> [H_element131,C_element141,N_element061,O_element122]
  conduct = 2
  density = 1
  expand = 3
  formula = G4_DNA_CYTIDINE
  name = G4_DNA_CYTIDINE
  specific = 4
FEATURE [App::DocumentObjectGroupPython] H_element132  label="H_element : 079"  # scripted group (container) (typed FeaturePython)
  n = 9
  ref = H_element
FEATURE [App::DocumentObjectGroupPython] C_element142  label="C_element : 087"  # scripted group (container) (typed FeaturePython)
  n = 9
  ref = C_element
FEATURE [App::DocumentObjectGroupPython] N_element062  label="N_element : 034"  # scripted group (container) (typed FeaturePython)
  n = 2
  ref = N_element
FEATURE [App::DocumentObjectGroupPython] O_element123  label="O_element : 076"  # scripted group (container) (typed FeaturePython)
  n = 6
  ref = O_element
FEATURE [App::DocumentObjectGroupPython] G4_DNA_URIDINE  # scripted group (container) (typed FeaturePython)
  Dunit = g/cm3
  Dvalue = 1
  Group = -> [H_element132,C_element142,N_element062,O_element123]
  conduct = 2
  density = 1
  expand = 3
  formula = G4_DNA_URIDINE
  name = G4_DNA_URIDINE
  specific = 4
FEATURE [App::DocumentObjectGroupPython] H_element133  label="H_element : 080"  # scripted group (container) (typed FeaturePython)
  n = 11
  ref = H_element
FEATURE [App::DocumentObjectGroupPython] C_element143  label="C_element : 088"  # scripted group (container) (typed FeaturePython)
  n = 10
  ref = C_element
FEATURE [App::DocumentObjectGroupPython] N_element063  label="N_element : 035"  # scripted group (container) (typed FeaturePython)
  n = 2
  ref = N_element
FEATURE [App::DocumentObjectGroupPython] O_element124  label="O_element : 077"  # scripted group (container) (typed FeaturePython)
  n = 6
  ref = O_element
FEATURE [App::DocumentObjectGroupPython] G4_DNA_METHYLURIDINE  # scripted group (container) (typed FeaturePython)
  Dunit = g/cm3
  Dvalue = 1
  Group = -> [H_element133,C_element143,N_element063,O_element124]
  conduct = 2
  density = 1
  expand = 3
  formula = G4_DNA_METHYLURIDINE
  name = G4_DNA_METHYLURIDINE
  specific = 4
FEATURE [App::DocumentObjectGroupPython] P_element014  label="P_element : 003"  # scripted group (container) (typed FeaturePython)
  n = 1
  ref = P_element
FEATURE [App::DocumentObjectGroupPython] O_element125  label="O_element : 078"  # scripted group (container) (typed FeaturePython)
  n = 3
  ref = O_element
FEATURE [App::DocumentObjectGroupPython] G4_DNA_MONOPHOSPHATE  # scripted group (container) (typed FeaturePython)
  Dunit = g/cm3
  Dvalue = 1
  Group = -> [P_element014,O_element125]
  conduct = 2
  density = 1
  expand = 3
  formula = G4_DNA_MONOPHOSPHATE
  name = G4_DNA_MONOPHOSPHATE
  specific = 4
FEATURE [App::DocumentObjectGroupPython] H_element134  label="H_element : 081"  # scripted group (container) (typed FeaturePython)
  n = 10
  ref = H_element
FEATURE [App::DocumentObjectGroupPython] C_element144  label="C_element : 089"  # scripted group (container) (typed FeaturePython)
  n = 10
  ref = C_element
FEATURE [App::DocumentObjectGroupPython] N_element064  label="N_element : 036"  # scripted group (container) (typed FeaturePython)
  n = 5
  ref = N_element
FEATURE [App::DocumentObjectGroupPython] O_element126  label="O_element : 079"  # scripted group (container) (typed FeaturePython)
  n = 7
  ref = O_element
FEATURE [App::DocumentObjectGroupPython] P_element015  label="P_element : 004"  # scripted group (container) (typed FeaturePython)
  n = 1
  ref = P_element
FEATURE [App::DocumentObjectGroupPython] G4_DNA_A  # scripted group (container) (typed FeaturePython)
  Dunit = g/cm3
  Dvalue = 1
  Group = -> [H_element134,C_element144,N_element064,O_element126,P_element015]
  conduct = 2
  density = 1
  expand = 3
  formula = G4_DNA_A
  name = G4_DNA_A
  specific = 4
FEATURE [App::DocumentObjectGroupPython] H_element135  label="H_element : 082"  # scripted group (container) (typed FeaturePython)
  n = 10
  ref = H_element
FEATURE [App::DocumentObjectGroupPython] C_element145  label="C_element : 090"  # scripted group (container) (typed FeaturePython)
  n = 10
  ref = C_element
FEATURE [App::DocumentObjectGroupPython] N_element065  label="N_element : 037"  # scripted group (container) (typed FeaturePython)
  n = 5
  ref = N_element
FEATURE [App::DocumentObjectGroupPython] O_element127  label="O_element : 8"  # scripted group (container) (typed FeaturePython)
  n = 8
  ref = O_element
FEATURE [App::DocumentObjectGroupPython] P_element016  label="P_element : 005"  # scripted group (container) (typed FeaturePython)
  n = 1
  ref = P_element
FEATURE [App::DocumentObjectGroupPython] G4_DNA_G  # scripted group (container) (typed FeaturePython)
  Dunit = g/cm3
  Dvalue = 1
  Group = -> [H_element135,C_element145,N_element065,O_element127,P_element016]
  conduct = 2
  density = 1
  expand = 3
  formula = G4_DNA_G
  name = G4_DNA_G
  specific = 4
FEATURE [App::DocumentObjectGroupPython] H_element136  label="H_element : 083"  # scripted group (container) (typed FeaturePython)
  n = 10
  ref = H_element
FEATURE [App::DocumentObjectGroupPython] C_element146  label="C_element : 091"  # scripted group (container) (typed FeaturePython)
  n = 9
  ref = C_element
FEATURE [App::DocumentObjectGroupPython] N_element066  label="N_element : 038"  # scripted group (container) (typed FeaturePython)
  n = 3
  ref = N_element
FEATURE [App::DocumentObjectGroupPython] O_element128  label="O_element : 080"  # scripted group (container) (typed FeaturePython)
  n = 8
  ref = O_element
FEATURE [App::DocumentObjectGroupPython] P_element017  label="P_element : 006"  # scripted group (container) (typed FeaturePython)
  n = 1
  ref = P_element
FEATURE [App::DocumentObjectGroupPython] G4_DNA_C  # scripted group (container) (typed FeaturePython)
  Dunit = g/cm3
  Dvalue = 1
  Group = -> [H_element136,C_element146,N_element066,O_element128,P_element017]
  conduct = 2
  density = 1
  expand = 3
  formula = G4_DNA_C
  name = G4_DNA_C
  specific = 4
FEATURE [App::DocumentObjectGroupPython] H_element137  label="H_element : 084"  # scripted group (container) (typed FeaturePython)
  n = 9
  ref = H_element
FEATURE [App::DocumentObjectGroupPython] C_element147  label="C_element : 092"  # scripted group (container) (typed FeaturePython)
  n = 9
  ref = C_element
FEATURE [App::DocumentObjectGroupPython] N_element067  label="N_element : 039"  # scripted group (container) (typed FeaturePython)
  n = 2
  ref = N_element
FEATURE [App::DocumentObjectGroupPython] O_element129  label="O_element : 9"  # scripted group (container) (typed FeaturePython)
  n = 9
  ref = O_element
FEATURE [App::DocumentObjectGroupPython] P_element018  label="P_element : 007"  # scripted group (container) (typed FeaturePython)
  n = 1
  ref = P_element
FEATURE [App::DocumentObjectGroupPython] G4_DNA_U  # scripted group (container) (typed FeaturePython)
  Dunit = g/cm3
  Dvalue = 1
  Group = -> [H_element137,C_element147,N_element067,O_element129,P_element018]
  conduct = 2
  density = 1
  expand = 3
  formula = G4_DNA_U
  name = G4_DNA_U
  specific = 4
FEATURE [App::DocumentObjectGroupPython] H_element138  label="H_element : 085"  # scripted group (container) (typed FeaturePython)
  n = 11
  ref = H_element
FEATURE [App::DocumentObjectGroupPython] C_element148  label="C_element : 093"  # scripted group (container) (typed FeaturePython)
  n = 10
  ref = C_element
FEATURE [App::DocumentObjectGroupPython] N_element068  label="N_element : 040"  # scripted group (container) (typed FeaturePython)
  n = 2
  ref = N_element
FEATURE [App::DocumentObjectGroupPython] O_element130  label="O_element : 081"  # scripted group (container) (typed FeaturePython)
  n = 9
  ref = O_element
FEATURE [App::DocumentObjectGroupPython] P_element019  label="P_element : 008"  # scripted group (container) (typed FeaturePython)
  n = 1
  ref = P_element
FEATURE [App::DocumentObjectGroupPython] G4_DNA_MU  # scripted group (container) (typed FeaturePython)
  Dunit = g/cm3
  Dvalue = 1
  Group = -> [H_element138,C_element148,N_element068,O_element130,P_element019]
  conduct = 2
  density = 1
  expand = 3
  formula = G4_DNA_MU
  name = G4_DNA_MU
  specific = 4
FEATURE [App::DocumentObjectGroupPython] BioChemical  # scripted group (container) (typed FeaturePython)
  Group = -> [G4_CYTOSINE,G4_THYMINE,G4_URACIL,G4_DNA_ADENINE,G4_DNA_GUANINE,G4_DNA_CYTOSINE,G4_DNA_THYMINE,G4_DNA_URACIL,G4_DNA_ADENOSINE,G4_DNA_GUANOSINE,G4_DNA_CYTIDINE,G4_DNA_URIDINE,G4_DNA_METHYLURIDINE,G4_DNA_MONOPHOSPHATE,G4_DNA_A,G4_DNA_G,G4_DNA_C,G4_DNA_U,G4_DNA_MU]
FEATURE [App::DocumentObjectGroupPython] G4Materials  # scripted group (container) (typed FeaturePython)
  Group = -> [NIST,Element,HEP,Space,BioChemical]
  version = 1
FEATURE [App::DocumentObjectGroupPython] Geant4  # scripted group (container) (typed FeaturePython)
  Group = -> [G4Isotopes,G4Elements,G4Materials]
FEATURE [App::DocumentObjectGroupPython] Materials  # scripted group (container) (typed FeaturePython)
  Group = -> [Geant4]
FEATURE [Part::FeaturePython] GDMLBox_WorldBox  # WARN: FeaturePython — macro-defined, semantics opaque (R4)
  lunit = 2
  material = 5
  x = 468
  y = 364
  z = 13
FEATURE [Part::FeaturePython] GDMLBox_Box002  # WARN: FeaturePython — macro-defined, semantics opaque (R4)
  Placement = pos=(20,0,0) rot=(0,0,1;0rad)
  lunit = 2
  material = 0
  x = 20
  y = 20
  z = 10
FEATURE [Part::FeaturePython] GDMLSphere001  # WARN: FeaturePython — macro-defined, semantics opaque (R4)
  aunit = 1
  deltaphi = 360
  deltatheta = 180
  lunit = 2
  material = 0
  rmax = 2
  rmin = 0
  startphi = 0
  starttheta = 0
FEATURE [Part::FeaturePython] GDMLTube001  # WARN: FeaturePython — macro-defined, semantics opaque (R4)
  Placement = pos=(17,-4,0) rot=(0,0,1;0rad)
  aunit = 1
  deltaphi = 90
  lunit = 2
  material = 0
  rmax = 7
  rmin = 5
  startphi = 0
  z = 7
FEATURE [App::Part] LV_Sphere001
  Group = -> [GDMLSphere001]
  Origin = -> Origin008
  Placement = pos=(15,-5,0) rot=(0,0,1;0rad)
  SkinSurface = 0
FEATURE [App::Part] LV_Tube001
  Group = -> [GDMLTube001]
  Origin = -> Origin007
  SkinSurface = 0
FEATURE [App::Part] LV_Box002
  Group = -> [GDMLBox_Box002,LV_Tube001,LV_Sphere001]
  Origin = -> Origin006
  Placement = pos=(20,0,0) rot=(1,0,0;1.5708rad)
FEATURE [Part::FeaturePython] Array  # Draft array (typed FeaturePython)
  AlwaysSyncPlacement = false
  Angle = 360
  ArrayType = 0
  Axis = (0,0,1)
  Base = -> LV_Box002
  Center = (0,0,0)
  Count = 4
  ExpandArray = false
  Fuse = true
  IntervalAxis = (0,0,0)
  IntervalX = (100,0,0)
  IntervalY = (0,100,0)
  IntervalZ = (0,0,100)
  NumberCircles = 3
  NumberPolar = 5
  NumberX = 2
  NumberY = 2
  NumberZ = 1
  Placement = pos=(-7,-15,0) rot=(0,0,1;0.523599rad)
  PlacementList = 4 placements: [(20,0,0),(20,100,0),(120,0,0),(120,100,0)]
  RadialDistance = 50
  ScaleList = (4) [(1,1,1),(1,1,1),(1,1,1),(1,1,1)]
  Symmetry = 1
  TangentialDistance = 25
FEATURE [App::Part] Part  label="experiment"
  Group = -> [LV_Box002,Array]
  Origin = -> Origin001
  Placement = pos=(30,30,0) rot=(0,0,1;0rad)
FEATURE [Part::Sphere] Sphere
  Angle1 = -90
  Angle2 = 90
  Angle3 = 360
  AttacherType = Attacher::AttachEngine3D
  Placement = pos=(53,14,0) rot=(0,0,1;0rad)
  Radius = 5
FEATURE [App::Part] LV_Box001  label="LV_Sphere"
  Group = -> [Sphere]
  Origin = -> Origin005
FEATURE [App::Part] worldVOL
  Group = -> [GDMLBox_WorldBox,Part,LV_Box001]
  Origin = -> Origin
